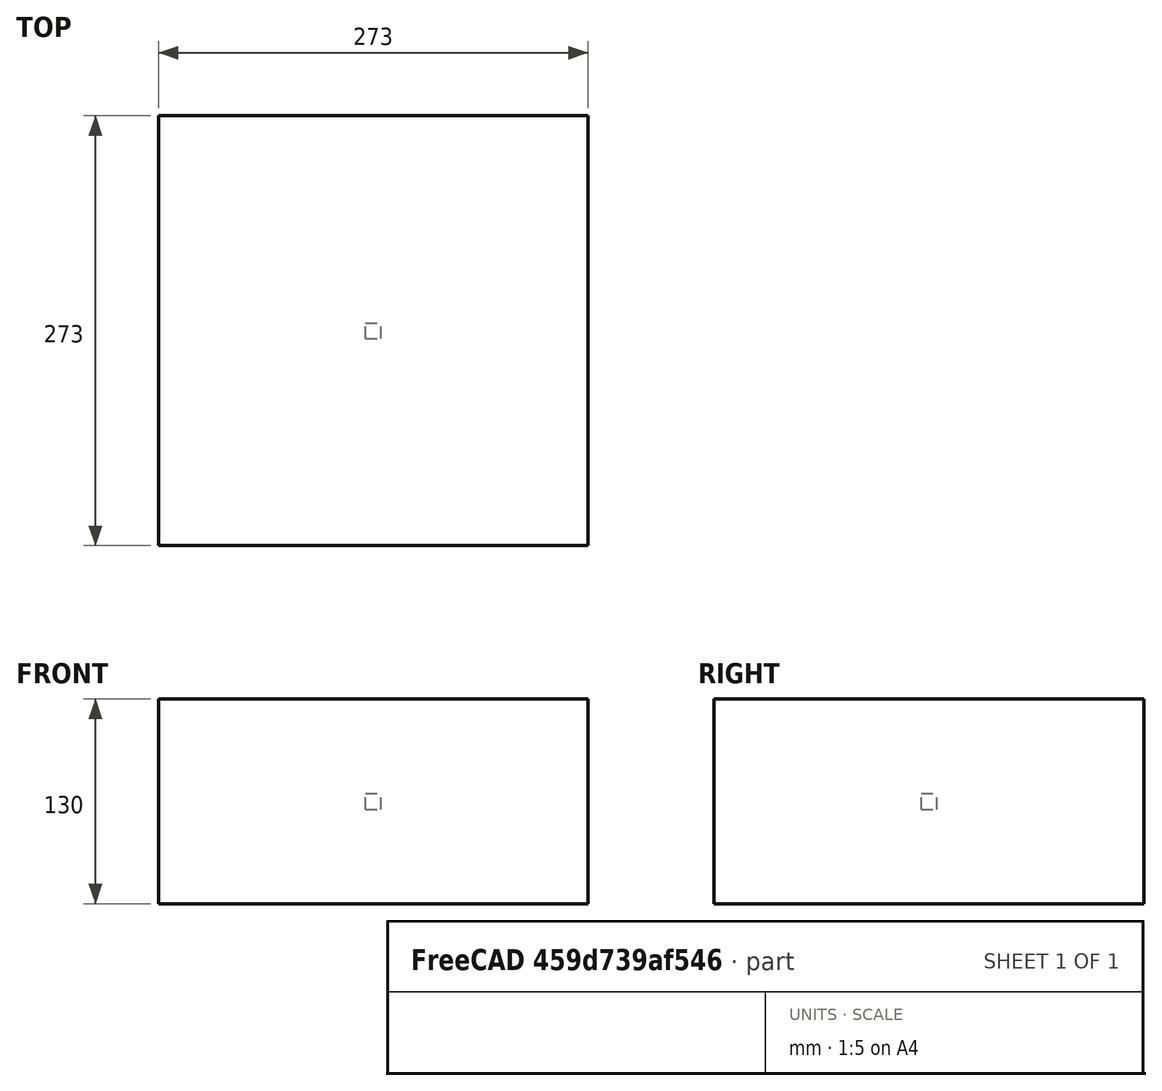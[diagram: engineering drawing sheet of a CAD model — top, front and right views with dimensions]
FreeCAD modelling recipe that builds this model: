
FCSTD DOCUMENT  (FreeCAD 0.20RUnknown)
Label: polarArray-2
License: All rights reserved
LicenseURL: http://en.wikipedia.org/wiki/All_rights_reserved
objects: App::DocumentObjectGroupPython×1251, Part::FeaturePython×3, App::Part×3
note: 2 computed .brp shape members not serialized (recipe doc carries the construction recipe); baked Part::Feature solids carry a one-line shape summary decoded from their .brp

FEATURE [App::DocumentObjectGroupPython] HALFPI  # scripted group (container) (typed FeaturePython)
  name = HALFPI
  value = pi/2.
FEATURE [App::DocumentObjectGroupPython] PI  # scripted group (container) (typed FeaturePython)
  name = PI
  value = 1.*pi
FEATURE [App::DocumentObjectGroupPython] TWOPI  # scripted group (container) (typed FeaturePython)
  name = TWOPI
  value = 2.*pi
FEATURE [App::DocumentObjectGroupPython] Constants  # scripted group (container) (typed FeaturePython)
  Group = -> [HALFPI,PI,TWOPI]
FEATURE [App::DocumentObjectGroupPython] Variables  # scripted group (container) (typed FeaturePython)
FEATURE [App::DocumentObjectGroupPython] Quantities  # scripted group (container) (typed FeaturePython)
FEATURE [App::DocumentObjectGroupPython] Isotopes  # scripted group (container) (typed FeaturePython)
FEATURE [App::DocumentObjectGroupPython] Elements  # scripted group (container) (typed FeaturePython)
FEATURE [App::DocumentObjectGroupPython] Matrix  # scripted group (container) (typed FeaturePython)
FEATURE [App::DocumentObjectGroupPython] Surfaces  # scripted group (container) (typed FeaturePython)
FEATURE [App::DocumentObjectGroupPython] Opticals  # scripted group (container) (typed FeaturePython)
  Group = -> [Matrix,Surfaces]
FEATURE [App::DocumentObjectGroupPython] G4Isotopes  # scripted group (container) (typed FeaturePython)
FEATURE [App::DocumentObjectGroupPython] H_element  # scripted group (container) (typed FeaturePython)
  Z = 1
  atom_value = 1.008
  formula = H
  name = H_element
FEATURE [App::DocumentObjectGroupPython] He_element  # scripted group (container) (typed FeaturePython)
  Z = 2
  atom_value = 4.0026
  formula = He
  name = He_element
FEATURE [App::DocumentObjectGroupPython] Li_element  # scripted group (container) (typed FeaturePython)
  Z = 3
  atom_value = 6.94
  formula = Li
  name = Li_element
FEATURE [App::DocumentObjectGroupPython] Be_element  # scripted group (container) (typed FeaturePython)
  Z = 4
  atom_value = 9.01218
  formula = Be
  name = Be_element
FEATURE [App::DocumentObjectGroupPython] B_element  # scripted group (container) (typed FeaturePython)
  Z = 5
  atom_value = 10.81
  formula = B
  name = B_element
FEATURE [App::DocumentObjectGroupPython] C_element  # scripted group (container) (typed FeaturePython)
  Z = 6
  atom_value = 12.011
  formula = C
  name = C_element
FEATURE [App::DocumentObjectGroupPython] N_element  # scripted group (container) (typed FeaturePython)
  Z = 7
  atom_value = 14.007
  formula = N
  name = N_element
FEATURE [App::DocumentObjectGroupPython] O_element  # scripted group (container) (typed FeaturePython)
  Z = 8
  atom_value = 15.999
  formula = O
  name = O_element
FEATURE [App::DocumentObjectGroupPython] F_element  # scripted group (container) (typed FeaturePython)
  Z = 9
  atom_value = 18.9984
  formula = F
  name = F_element
FEATURE [App::DocumentObjectGroupPython] Ne_element  # scripted group (container) (typed FeaturePython)
  Z = 10
  atom_value = 20.1797
  formula = Ne
  name = Ne_element
FEATURE [App::DocumentObjectGroupPython] Na_element  # scripted group (container) (typed FeaturePython)
  Z = 11
  atom_value = 22.9898
  formula = Na
  name = Na_element
FEATURE [App::DocumentObjectGroupPython] Mg_element  # scripted group (container) (typed FeaturePython)
  Z = 12
  atom_value = 24.305
  formula = Mg
  name = Mg_element
FEATURE [App::DocumentObjectGroupPython] Al_element  # scripted group (container) (typed FeaturePython)
  Z = 13
  atom_value = 26.9815
  formula = Al
  name = Al_element
FEATURE [App::DocumentObjectGroupPython] Si_element  # scripted group (container) (typed FeaturePython)
  Z = 14
  atom_value = 28.085
  formula = Si
  name = Si_element
FEATURE [App::DocumentObjectGroupPython] P_element  # scripted group (container) (typed FeaturePython)
  Z = 15
  atom_value = 30.9738
  formula = P
  name = P_element
FEATURE [App::DocumentObjectGroupPython] S_element  # scripted group (container) (typed FeaturePython)
  Z = 16
  atom_value = 32.06
  formula = S
  name = S_element
FEATURE [App::DocumentObjectGroupPython] Cl_element  # scripted group (container) (typed FeaturePython)
  Z = 17
  atom_value = 35.45
  formula = Cl
  name = Cl_element
FEATURE [App::DocumentObjectGroupPython] Ar_element  # scripted group (container) (typed FeaturePython)
  Z = 18
  atom_value = 39.95
  formula = Ar
  name = Ar_element
FEATURE [App::DocumentObjectGroupPython] K_element  # scripted group (container) (typed FeaturePython)
  Z = 19
  atom_value = 39.0983
  formula = K
  name = K_element
FEATURE [App::DocumentObjectGroupPython] Ca_element  # scripted group (container) (typed FeaturePython)
  Z = 20
  atom_value = 40.078
  formula = Ca
  name = Ca_element
FEATURE [App::DocumentObjectGroupPython] Sc_element  # scripted group (container) (typed FeaturePython)
  Z = 21
  atom_value = 44.9559
  formula = Sc
  name = Sc_element
FEATURE [App::DocumentObjectGroupPython] Ti_element  # scripted group (container) (typed FeaturePython)
  Z = 22
  atom_value = 47.867
  formula = Ti
  name = Ti_element
FEATURE [App::DocumentObjectGroupPython] V_element  # scripted group (container) (typed FeaturePython)
  Z = 23
  atom_value = 50.9415
  formula = V
  name = V_element
FEATURE [App::DocumentObjectGroupPython] Cr_element  # scripted group (container) (typed FeaturePython)
  Z = 24
  atom_value = 51.9961
  formula = Cr
  name = Cr_element
FEATURE [App::DocumentObjectGroupPython] Mn_element  # scripted group (container) (typed FeaturePython)
  Z = 25
  atom_value = 54.938
  formula = Mn
  name = Mn_element
FEATURE [App::DocumentObjectGroupPython] Fe_element  # scripted group (container) (typed FeaturePython)
  Z = 26
  atom_value = 55.845
  formula = Fe
  name = Fe_element
FEATURE [App::DocumentObjectGroupPython] Co_element  # scripted group (container) (typed FeaturePython)
  Z = 27
  atom_value = 58.9332
  formula = Co
  name = Co_element
FEATURE [App::DocumentObjectGroupPython] Ni_element  # scripted group (container) (typed FeaturePython)
  Z = 28
  atom_value = 58.6934
  formula = Ni
  name = Ni_element
FEATURE [App::DocumentObjectGroupPython] Cu_element  # scripted group (container) (typed FeaturePython)
  Z = 29
  atom_value = 63.546
  formula = Cu
  name = Cu_element
FEATURE [App::DocumentObjectGroupPython] Zn_element  # scripted group (container) (typed FeaturePython)
  Z = 30
  atom_value = 65.38
  formula = Zn
  name = Zn_element
FEATURE [App::DocumentObjectGroupPython] Ga_element  # scripted group (container) (typed FeaturePython)
  Z = 31
  atom_value = 69.723
  formula = Ga
  name = Ga_element
FEATURE [App::DocumentObjectGroupPython] Ge_element  # scripted group (container) (typed FeaturePython)
  Z = 32
  atom_value = 72.63
  formula = Ge
  name = Ge_element
FEATURE [App::DocumentObjectGroupPython] As_element  # scripted group (container) (typed FeaturePython)
  Z = 33
  atom_value = 74.9216
  formula = As
  name = As_element
FEATURE [App::DocumentObjectGroupPython] Se_element  # scripted group (container) (typed FeaturePython)
  Z = 34
  atom_value = 78.971
  formula = Se
  name = Se_element
FEATURE [App::DocumentObjectGroupPython] Br_element  # scripted group (container) (typed FeaturePython)
  Z = 35
  atom_value = 79.904
  formula = Br
  name = Br_element
FEATURE [App::DocumentObjectGroupPython] Kr_element  # scripted group (container) (typed FeaturePython)
  Z = 36
  atom_value = 83.798
  formula = Kr
  name = Kr_element
FEATURE [App::DocumentObjectGroupPython] Rb_element  # scripted group (container) (typed FeaturePython)
  Z = 37
  atom_value = 85.4678
  formula = Rb
  name = Rb_element
FEATURE [App::DocumentObjectGroupPython] Sr_element  # scripted group (container) (typed FeaturePython)
  Z = 38
  atom_value = 87.62
  formula = Sr
  name = Sr_element
FEATURE [App::DocumentObjectGroupPython] Y_element  # scripted group (container) (typed FeaturePython)
  Z = 39
  atom_value = 88.9058
  formula = Y
  name = Y_element
FEATURE [App::DocumentObjectGroupPython] Zr_element  # scripted group (container) (typed FeaturePython)
  Z = 40
  atom_value = 91.224
  formula = Zr
  name = Zr_element
FEATURE [App::DocumentObjectGroupPython] Nb_element  # scripted group (container) (typed FeaturePython)
  Z = 41
  atom_value = 92.9064
  formula = Nb
  name = Nb_element
FEATURE [App::DocumentObjectGroupPython] Mo_element  # scripted group (container) (typed FeaturePython)
  Z = 42
  atom_value = 95.95
  formula = Mo
  name = Mo_element
FEATURE [App::DocumentObjectGroupPython] Tc_element  # scripted group (container) (typed FeaturePython)
  Z = 43
  atom_value = 97
  formula = Tc
  name = Tc_element
FEATURE [App::DocumentObjectGroupPython] Ru_element  # scripted group (container) (typed FeaturePython)
  Z = 44
  atom_value = 101.07
  formula = Ru
  name = Ru_element
FEATURE [App::DocumentObjectGroupPython] Rh_element  # scripted group (container) (typed FeaturePython)
  Z = 45
  atom_value = 102.905
  formula = Rh
  name = Rh_element
FEATURE [App::DocumentObjectGroupPython] Pd_element  # scripted group (container) (typed FeaturePython)
  Z = 46
  atom_value = 106.42
  formula = Pd
  name = Pd_element
FEATURE [App::DocumentObjectGroupPython] Ag_element  # scripted group (container) (typed FeaturePython)
  Z = 47
  atom_value = 107.868
  formula = Ag
  name = Ag_element
FEATURE [App::DocumentObjectGroupPython] Cd_element  # scripted group (container) (typed FeaturePython)
  Z = 48
  atom_value = 112.414
  formula = Cd
  name = Cd_element
FEATURE [App::DocumentObjectGroupPython] In_element  # scripted group (container) (typed FeaturePython)
  Z = 49
  atom_value = 114.818
  formula = In
  name = In_element
FEATURE [App::DocumentObjectGroupPython] Sn_element  # scripted group (container) (typed FeaturePython)
  Z = 50
  atom_value = 118.71
  formula = Sn
  name = Sn_element
FEATURE [App::DocumentObjectGroupPython] Sb_element  # scripted group (container) (typed FeaturePython)
  Z = 51
  atom_value = 121.76
  formula = Sb
  name = Sb_element
FEATURE [App::DocumentObjectGroupPython] Te_element  # scripted group (container) (typed FeaturePython)
  Z = 52
  atom_value = 127.6
  formula = Te
  name = Te_element
FEATURE [App::DocumentObjectGroupPython] I_element  # scripted group (container) (typed FeaturePython)
  Z = 53
  atom_value = 126.904
  formula = I
  name = I_element
FEATURE [App::DocumentObjectGroupPython] Xe_element  # scripted group (container) (typed FeaturePython)
  Z = 54
  atom_value = 131.293
  formula = Xe
  name = Xe_element
FEATURE [App::DocumentObjectGroupPython] Cs_element  # scripted group (container) (typed FeaturePython)
  Z = 55
  atom_value = 132.905
  formula = Cs
  name = Cs_element
FEATURE [App::DocumentObjectGroupPython] Ba_element  # scripted group (container) (typed FeaturePython)
  Z = 56
  atom_value = 137.327
  formula = Ba
  name = Ba_element
FEATURE [App::DocumentObjectGroupPython] La_element  # scripted group (container) (typed FeaturePython)
  Z = 57
  atom_value = 138.905
  formula = La
  name = La_element
FEATURE [App::DocumentObjectGroupPython] Ce_element  # scripted group (container) (typed FeaturePython)
  Z = 58
  atom_value = 140.116
  formula = Ce
  name = Ce_element
FEATURE [App::DocumentObjectGroupPython] Pr_element  # scripted group (container) (typed FeaturePython)
  Z = 59
  atom_value = 140.908
  formula = Pr
  name = Pr_element
FEATURE [App::DocumentObjectGroupPython] Nd_element  # scripted group (container) (typed FeaturePython)
  Z = 60
  atom_value = 144.242
  formula = Nd
  name = Nd_element
FEATURE [App::DocumentObjectGroupPython] Pm_element  # scripted group (container) (typed FeaturePython)
  Z = 61
  atom_value = 145
  formula = Pm
  name = Pm_element
FEATURE [App::DocumentObjectGroupPython] Sm_element  # scripted group (container) (typed FeaturePython)
  Z = 62
  atom_value = 150.36
  formula = Sm
  name = Sm_element
FEATURE [App::DocumentObjectGroupPython] Eu_element  # scripted group (container) (typed FeaturePython)
  Z = 63
  atom_value = 151.964
  formula = Eu
  name = Eu_element
FEATURE [App::DocumentObjectGroupPython] Gd_element  # scripted group (container) (typed FeaturePython)
  Z = 64
  atom_value = 157.25
  formula = Gd
  name = Gd_element
FEATURE [App::DocumentObjectGroupPython] Tb_element  # scripted group (container) (typed FeaturePython)
  Z = 65
  atom_value = 158.925
  formula = Tb
  name = Tb_element
FEATURE [App::DocumentObjectGroupPython] Dy_element  # scripted group (container) (typed FeaturePython)
  Z = 66
  atom_value = 162.5
  formula = Dy
  name = Dy_element
FEATURE [App::DocumentObjectGroupPython] Ho_element  # scripted group (container) (typed FeaturePython)
  Z = 67
  atom_value = 164.93
  formula = Ho
  name = Ho_element
FEATURE [App::DocumentObjectGroupPython] Er_element  # scripted group (container) (typed FeaturePython)
  Z = 68
  atom_value = 167.259
  formula = Er
  name = Er_element
FEATURE [App::DocumentObjectGroupPython] Tm_element  # scripted group (container) (typed FeaturePython)
  Z = 69
  atom_value = 168.934
  formula = Tm
  name = Tm_element
FEATURE [App::DocumentObjectGroupPython] Yb_element  # scripted group (container) (typed FeaturePython)
  Z = 70
  atom_value = 173.045
  formula = Yb
  name = Yb_element
FEATURE [App::DocumentObjectGroupPython] Lu_element  # scripted group (container) (typed FeaturePython)
  Z = 71
  atom_value = 174.967
  formula = Lu
  name = Lu_element
FEATURE [App::DocumentObjectGroupPython] Hf_element  # scripted group (container) (typed FeaturePython)
  Z = 72
  atom_value = 178.49
  formula = Hf
  name = Hf_element
FEATURE [App::DocumentObjectGroupPython] Ta_element  # scripted group (container) (typed FeaturePython)
  Z = 73
  atom_value = 180.948
  formula = Ta
  name = Ta_element
FEATURE [App::DocumentObjectGroupPython] W_element  # scripted group (container) (typed FeaturePython)
  Z = 74
  atom_value = 183.84
  formula = W
  name = W_element
FEATURE [App::DocumentObjectGroupPython] Re_element  # scripted group (container) (typed FeaturePython)
  Z = 75
  atom_value = 186.207
  formula = Re
  name = Re_element
FEATURE [App::DocumentObjectGroupPython] Os_element  # scripted group (container) (typed FeaturePython)
  Z = 76
  atom_value = 190.23
  formula = Os
  name = Os_element
FEATURE [App::DocumentObjectGroupPython] Ir_element  # scripted group (container) (typed FeaturePython)
  Z = 77
  atom_value = 192.217
  formula = Ir
  name = Ir_element
FEATURE [App::DocumentObjectGroupPython] Pt_element  # scripted group (container) (typed FeaturePython)
  Z = 78
  atom_value = 195.084
  formula = Pt
  name = Pt_element
FEATURE [App::DocumentObjectGroupPython] Au_element  # scripted group (container) (typed FeaturePython)
  Z = 79
  atom_value = 196.967
  formula = Au
  name = Au_element
FEATURE [App::DocumentObjectGroupPython] Hg_element  # scripted group (container) (typed FeaturePython)
  Z = 80
  atom_value = 200.592
  formula = Hg
  name = Hg_element
FEATURE [App::DocumentObjectGroupPython] Tl_element  # scripted group (container) (typed FeaturePython)
  Z = 81
  atom_value = 204.38
  formula = Tl
  name = Tl_element
FEATURE [App::DocumentObjectGroupPython] Pb_element  # scripted group (container) (typed FeaturePython)
  Z = 82
  atom_value = 207.2
  formula = Pb
  name = Pb_element
FEATURE [App::DocumentObjectGroupPython] Bi_element  # scripted group (container) (typed FeaturePython)
  Z = 83
  atom_value = 208.98
  formula = Bi
  name = Bi_element
FEATURE [App::DocumentObjectGroupPython] Po_element  # scripted group (container) (typed FeaturePython)
  Z = 84
  atom_value = 209
  formula = Po
  name = Po_element
FEATURE [App::DocumentObjectGroupPython] At_element  # scripted group (container) (typed FeaturePython)
  Z = 85
  atom_value = 210
  formula = At
  name = At_element
FEATURE [App::DocumentObjectGroupPython] Rn_element  # scripted group (container) (typed FeaturePython)
  Z = 86
  atom_value = 222
  formula = Rn
  name = Rn_element
FEATURE [App::DocumentObjectGroupPython] Fr_element  # scripted group (container) (typed FeaturePython)
  Z = 87
  atom_value = 223
  formula = Fr
  name = Fr_element
FEATURE [App::DocumentObjectGroupPython] Ra_element  # scripted group (container) (typed FeaturePython)
  Z = 88
  atom_value = 226
  formula = Ra
  name = Ra_element
FEATURE [App::DocumentObjectGroupPython] Ac_element  # scripted group (container) (typed FeaturePython)
  Z = 89
  atom_value = 227
  formula = Ac
  name = Ac_element
FEATURE [App::DocumentObjectGroupPython] Th_element  # scripted group (container) (typed FeaturePython)
  Z = 90
  atom_value = 232.038
  formula = Th
  name = Th_element
FEATURE [App::DocumentObjectGroupPython] Pa_element  # scripted group (container) (typed FeaturePython)
  Z = 91
  atom_value = 231.036
  formula = Pa
  name = Pa_element
FEATURE [App::DocumentObjectGroupPython] U_element  # scripted group (container) (typed FeaturePython)
  Z = 92
  atom_value = 238.029
  formula = U
  name = U_element
FEATURE [App::DocumentObjectGroupPython] Np_element  # scripted group (container) (typed FeaturePython)
  Z = 93
  atom_value = 237
  formula = Np
  name = Np_element
FEATURE [App::DocumentObjectGroupPython] Pu_element  # scripted group (container) (typed FeaturePython)
  Z = 94
  atom_value = 244
  formula = Pu
  name = Pu_element
FEATURE [App::DocumentObjectGroupPython] Am_element  # scripted group (container) (typed FeaturePython)
  Z = 95
  atom_value = 243
  formula = Am
  name = Am_element
FEATURE [App::DocumentObjectGroupPython] Cm_element  # scripted group (container) (typed FeaturePython)
  Z = 96
  atom_value = 247
  formula = Cm
  name = Cm_element
FEATURE [App::DocumentObjectGroupPython] Bk_element  # scripted group (container) (typed FeaturePython)
  Z = 97
  atom_value = 247
  formula = Bk
  name = Bk_element
FEATURE [App::DocumentObjectGroupPython] Cf_element  # scripted group (container) (typed FeaturePython)
  Z = 98
  atom_value = 251
  formula = Cf
  name = Cf_element
FEATURE [App::DocumentObjectGroupPython] G4Elements  # scripted group (container) (typed FeaturePython)
  Group = -> [H_element,He_element,Li_element,Be_element,B_element,C_element,N_element,O_element,F_element,Ne_element,Na_element,Mg_element,Al_element,Si_element,P_element,S_element,Cl_element,Ar_element,K_element,Ca_element,Sc_element,Ti_element,V_element,Cr_element,Mn_element,Fe_element,Co_element,Ni_element,Cu_element,Zn_element,Ga_element,Ge_element,As_element,Se_element,Br_element,Kr_element,Rb_element,+61 more]
FEATURE [App::DocumentObjectGroupPython] H_element001  label="H_element : 0.101"  # scripted group (container) (typed FeaturePython)
  n = 0.101327
FEATURE [App::DocumentObjectGroupPython] C_element001  label="C_element : 0.775"  # scripted group (container) (typed FeaturePython)
  n = 0.7755
FEATURE [App::DocumentObjectGroupPython] N_element001  label="N_element : 0.035"  # scripted group (container) (typed FeaturePython)
  n = 0.035057
FEATURE [App::DocumentObjectGroupPython] O_element001  label="O_element : 0.052"  # scripted group (container) (typed FeaturePython)
  n = 0.0523159
FEATURE [App::DocumentObjectGroupPython] F_element001  label="F_element : 0.017"  # scripted group (container) (typed FeaturePython)
  n = 0.017422
FEATURE [App::DocumentObjectGroupPython] Ca_element001  label="Ca_element : 0.018"  # scripted group (container) (typed FeaturePython)
  n = 0.018378
FEATURE [App::DocumentObjectGroupPython] G4_A_150_TISSUE  label="G4_A-150_TISSUE"  # scripted group (container) (typed FeaturePython)
  Dunit = g/cm3
  Dvalue = 1.127
  Group = -> [H_element001,C_element001,N_element001,O_element001,F_element001,Ca_element001]
  conduct = 2
  density = 1
  expand = 3
  formula = G4_A-150_TISSUE
  name = G4_A-150_TISSUE
  specific = 4
FEATURE [App::DocumentObjectGroupPython] C_element002  label="C_element : 3"  # scripted group (container) (typed FeaturePython)
  n = 3
  ref = C_element
FEATURE [App::DocumentObjectGroupPython] H_element002  label="H_element : 6"  # scripted group (container) (typed FeaturePython)
  n = 6
  ref = H_element
FEATURE [App::DocumentObjectGroupPython] O_element002  label="O_element : 1"  # scripted group (container) (typed FeaturePython)
  n = 1
  ref = O_element
FEATURE [App::DocumentObjectGroupPython] G4_ACETONE  # scripted group (container) (typed FeaturePython)
  Dunit = g/cm3
  Dvalue = 0.7899
  Group = -> [C_element002,H_element002,O_element002]
  conduct = 2
  density = 1
  expand = 3
  formula = G4_ACETONE
  name = G4_ACETONE
  specific = 4
FEATURE [App::DocumentObjectGroupPython] C_element003  label="C_element : 2"  # scripted group (container) (typed FeaturePython)
  n = 2
  ref = C_element
FEATURE [App::DocumentObjectGroupPython] H_element003  label="H_element : 2"  # scripted group (container) (typed FeaturePython)
  n = 2
  ref = H_element
FEATURE [App::DocumentObjectGroupPython] G4_ACETYLENE  # scripted group (container) (typed FeaturePython)
  Dunit = g/cm3
  Dvalue = 0.0010967
  Group = -> [C_element003,H_element003]
  conduct = 2
  density = 1
  expand = 3
  formula = G4_ACETYLENE
  name = G4_ACETYLENE
  specific = 4
FEATURE [App::DocumentObjectGroupPython] C_element004  label="C_element : 5"  # scripted group (container) (typed FeaturePython)
  n = 5
  ref = C_element
FEATURE [App::DocumentObjectGroupPython] H_element004  label="H_element : 5"  # scripted group (container) (typed FeaturePython)
  n = 5
  ref = H_element
FEATURE [App::DocumentObjectGroupPython] N_element002  label="N_element : 5"  # scripted group (container) (typed FeaturePython)
  n = 5
  ref = N_element
FEATURE [App::DocumentObjectGroupPython] G4_ADENINE  # scripted group (container) (typed FeaturePython)
  Dunit = g/cm3
  Dvalue = 1.6
  Group = -> [C_element004,H_element004,N_element002]
  conduct = 2
  density = 1
  expand = 3
  formula = G4_ADENINE
  name = G4_ADENINE
  specific = 4
FEATURE [App::DocumentObjectGroupPython] H_element005  label="H_element : 0.114"  # scripted group (container) (typed FeaturePython)
  n = 0.114
FEATURE [App::DocumentObjectGroupPython] C_element005  label="C_element : 0.598"  # scripted group (container) (typed FeaturePython)
  n = 0.598
FEATURE [App::DocumentObjectGroupPython] N_element003  label="N_element : 0.007"  # scripted group (container) (typed FeaturePython)
  n = 0.007
FEATURE [App::DocumentObjectGroupPython] O_element003  label="O_element : 0.278"  # scripted group (container) (typed FeaturePython)
  n = 0.278
FEATURE [App::DocumentObjectGroupPython] Na_element001  label="Na_element : 0.001"  # scripted group (container) (typed FeaturePython)
  n = 0.001
FEATURE [App::DocumentObjectGroupPython] S_element001  label="S_element : 0.001"  # scripted group (container) (typed FeaturePython)
  n = 0.001
FEATURE [App::DocumentObjectGroupPython] Cl_element001  label="Cl_element : 0.001"  # scripted group (container) (typed FeaturePython)
  n = 0.001
FEATURE [App::DocumentObjectGroupPython] G4_ADIPOSE_TISSUE_ICRP  # scripted group (container) (typed FeaturePython)
  Dunit = g/cm3
  Dvalue = 0.95
  Group = -> [H_element005,C_element005,N_element003,O_element003,Na_element001,S_element001,Cl_element001]
  conduct = 2
  density = 1
  expand = 3
  formula = G4_ADIPOSE_TISSUE_ICRP
  name = G4_ADIPOSE_TISSUE_ICRP
  specific = 4
FEATURE [App::DocumentObjectGroupPython] C_element006  label="C_element : 0.000"  # scripted group (container) (typed FeaturePython)
  n = 0.000124
FEATURE [App::DocumentObjectGroupPython] N_element004  label="N_element : 0.755"  # scripted group (container) (typed FeaturePython)
  n = 0.755268
FEATURE [App::DocumentObjectGroupPython] O_element004  label="O_element : 0.232"  # scripted group (container) (typed FeaturePython)
  n = 0.231781
FEATURE [App::DocumentObjectGroupPython] Ar_element001  label="Ar_element : 0.013"  # scripted group (container) (typed FeaturePython)
  n = 0.012827
FEATURE [App::DocumentObjectGroupPython] G4_AIR  # scripted group (container) (typed FeaturePython)
  Dunit = g/cm3
  Dvalue = 0.00120479
  Group = -> [C_element006,N_element004,O_element004,Ar_element001]
  conduct = 2
  density = 1
  expand = 3
  formula = G4_AIR
  name = G4_AIR
  specific = 4
FEATURE [App::DocumentObjectGroupPython] C_element007  label="C_element : 006"  # scripted group (container) (typed FeaturePython)
  n = 3
  ref = C_element
FEATURE [App::DocumentObjectGroupPython] H_element006  label="H_element : 7"  # scripted group (container) (typed FeaturePython)
  n = 7
  ref = H_element
FEATURE [App::DocumentObjectGroupPython] N_element005  label="N_element : 1"  # scripted group (container) (typed FeaturePython)
  n = 1
  ref = N_element
FEATURE [App::DocumentObjectGroupPython] O_element005  label="O_element : 2"  # scripted group (container) (typed FeaturePython)
  n = 2
  ref = O_element
FEATURE [App::DocumentObjectGroupPython] G4_ALANINE  # scripted group (container) (typed FeaturePython)
  Dunit = g/cm3
  Dvalue = 1.42
  Group = -> [C_element007,H_element006,N_element005,O_element005]
  conduct = 2
  density = 1
  expand = 3
  formula = G4_ALANINE
  name = G4_ALANINE
  specific = 4
FEATURE [App::DocumentObjectGroupPython] Al_element001  label="Al_element : 2"  # scripted group (container) (typed FeaturePython)
  n = 2
  ref = Al_element
FEATURE [App::DocumentObjectGroupPython] O_element006  label="O_element : 3"  # scripted group (container) (typed FeaturePython)
  n = 3
  ref = O_element
FEATURE [App::DocumentObjectGroupPython] G4_ALUMINUM_OXIDE  # scripted group (container) (typed FeaturePython)
  Dunit = g/cm3
  Dvalue = 3.97
  Group = -> [Al_element001,O_element006]
  conduct = 2
  density = 1
  expand = 3
  formula = G4_ALUMINUM_OXIDE
  name = G4_ALUMINUM_OXIDE
  specific = 4
FEATURE [App::DocumentObjectGroupPython] H_element007  label="H_element : 0.106"  # scripted group (container) (typed FeaturePython)
  n = 0.10593
FEATURE [App::DocumentObjectGroupPython] C_element008  label="C_element : 0.789"  # scripted group (container) (typed FeaturePython)
  n = 0.788974
FEATURE [App::DocumentObjectGroupPython] O_element007  label="O_element : 0.105"  # scripted group (container) (typed FeaturePython)
  n = 0.105096
FEATURE [App::DocumentObjectGroupPython] G4_AMBER  # scripted group (container) (typed FeaturePython)
  Dunit = g/cm3
  Dvalue = 1.1
  Group = -> [H_element007,C_element008,O_element007]
  conduct = 2
  density = 1
  expand = 3
  formula = G4_AMBER
  name = G4_AMBER
  specific = 4
FEATURE [App::DocumentObjectGroupPython] N_element006  label="N_element : 006"  # scripted group (container) (typed FeaturePython)
  n = 1
  ref = N_element
FEATURE [App::DocumentObjectGroupPython] H_element008  label="H_element : 3"  # scripted group (container) (typed FeaturePython)
  n = 3
  ref = H_element
FEATURE [App::DocumentObjectGroupPython] G4_AMMONIA  # scripted group (container) (typed FeaturePython)
  Dunit = g/cm3
  Dvalue = 0.000826019
  Group = -> [N_element006,H_element008]
  conduct = 2
  density = 1
  expand = 3
  formula = G4_AMMONIA
  name = G4_AMMONIA
  specific = 4
FEATURE [App::DocumentObjectGroupPython] C_element009  label="C_element : 6"  # scripted group (container) (typed FeaturePython)
  n = 6
  ref = C_element
FEATURE [App::DocumentObjectGroupPython] H_element009  label="H_element : 008"  # scripted group (container) (typed FeaturePython)
  n = 7
  ref = H_element
FEATURE [App::DocumentObjectGroupPython] N_element007  label="N_element : 007"  # scripted group (container) (typed FeaturePython)
  n = 1
  ref = N_element
FEATURE [App::DocumentObjectGroupPython] G4_ANILINE  # scripted group (container) (typed FeaturePython)
  Dunit = g/cm3
  Dvalue = 1.0235
  Group = -> [C_element009,H_element009,N_element007]
  conduct = 2
  density = 1
  expand = 3
  formula = G4_ANILINE
  name = G4_ANILINE
  specific = 4
FEATURE [App::DocumentObjectGroupPython] C_element010  label="C_element : 14"  # scripted group (container) (typed FeaturePython)
  n = 14
  ref = C_element
FEATURE [App::DocumentObjectGroupPython] H_element010  label="H_element : 10"  # scripted group (container) (typed FeaturePython)
  n = 10
  ref = H_element
FEATURE [App::DocumentObjectGroupPython] G4_ANTHRACENE  # scripted group (container) (typed FeaturePython)
  Dunit = g/cm3
  Dvalue = 1.283
  Group = -> [C_element010,H_element010]
  conduct = 2
  density = 1
  expand = 3
  formula = G4_ANTHRACENE
  name = G4_ANTHRACENE
  specific = 4
FEATURE [App::DocumentObjectGroupPython] H_element011  label="H_element : 0.065"  # scripted group (container) (typed FeaturePython)
  n = 0.0654709
FEATURE [App::DocumentObjectGroupPython] C_element011  label="C_element : 0.537"  # scripted group (container) (typed FeaturePython)
  n = 0.536944
FEATURE [App::DocumentObjectGroupPython] N_element008  label="N_element : 0.021"  # scripted group (container) (typed FeaturePython)
  n = 0.0215
FEATURE [App::DocumentObjectGroupPython] O_element008  label="O_element : 0.032"  # scripted group (container) (typed FeaturePython)
  n = 0.032085
FEATURE [App::DocumentObjectGroupPython] F_element002  label="F_element : 0.167"  # scripted group (container) (typed FeaturePython)
  n = 0.167411
FEATURE [App::DocumentObjectGroupPython] Ca_element002  label="Ca_element : 0.177"  # scripted group (container) (typed FeaturePython)
  n = 0.176589
FEATURE [App::DocumentObjectGroupPython] G4_B_100_BONE  label="G4_B-100_BONE"  # scripted group (container) (typed FeaturePython)
  Dunit = g/cm3
  Dvalue = 1.45
  Group = -> [H_element011,C_element011,N_element008,O_element008,F_element002,Ca_element002]
  conduct = 2
  density = 1
  expand = 3
  formula = G4_B-100_BONE
  name = G4_B-100_BONE
  specific = 4
FEATURE [App::DocumentObjectGroupPython] H_element012  label="H_element : 0.057"  # scripted group (container) (typed FeaturePython)
  n = 0.057441
FEATURE [App::DocumentObjectGroupPython] C_element012  label="C_element : 0.790"  # scripted group (container) (typed FeaturePython)
  n = 0.774591
FEATURE [App::DocumentObjectGroupPython] O_element009  label="O_element : 0.168"  # scripted group (container) (typed FeaturePython)
  n = 0.167968
FEATURE [App::DocumentObjectGroupPython] G4_BAKELITE  # scripted group (container) (typed FeaturePython)
  Dunit = g/cm3
  Dvalue = 1.25
  Group = -> [H_element012,C_element012,O_element009]
  conduct = 2
  density = 1
  expand = 3
  formula = G4_BAKELITE
  name = G4_BAKELITE
  specific = 4
FEATURE [App::DocumentObjectGroupPython] Ba_element001  label="Ba_element : 1"  # scripted group (container) (typed FeaturePython)
  n = 1
  ref = Ba_element
FEATURE [App::DocumentObjectGroupPython] F_element003  label="F_element : 2"  # scripted group (container) (typed FeaturePython)
  n = 2
  ref = F_element
FEATURE [App::DocumentObjectGroupPython] G4_BARIUM_FLUORIDE  # scripted group (container) (typed FeaturePython)
  Dunit = g/cm3
  Dvalue = 4.89
  Group = -> [Ba_element001,F_element003]
  conduct = 2
  density = 1
  expand = 3
  formula = G4_BARIUM_FLUORIDE
  name = G4_BARIUM_FLUORIDE
  specific = 4
FEATURE [App::DocumentObjectGroupPython] Ba_element002  label="Ba_element : 002"  # scripted group (container) (typed FeaturePython)
  n = 1
  ref = Ba_element
FEATURE [App::DocumentObjectGroupPython] S_element002  label="S_element : 1"  # scripted group (container) (typed FeaturePython)
  n = 1
  ref = S_element
FEATURE [App::DocumentObjectGroupPython] O_element010  label="O_element : 4"  # scripted group (container) (typed FeaturePython)
  n = 4
  ref = O_element
FEATURE [App::DocumentObjectGroupPython] G4_BARIUM_SULFATE  # scripted group (container) (typed FeaturePython)
  Dunit = g/cm3
  Dvalue = 4.5
  Group = -> [Ba_element002,S_element002,O_element010]
  conduct = 2
  density = 1
  expand = 3
  formula = G4_BARIUM_SULFATE
  name = G4_BARIUM_SULFATE
  specific = 4
FEATURE [App::DocumentObjectGroupPython] C_element013  label="C_element : 007"  # scripted group (container) (typed FeaturePython)
  n = 6
  ref = C_element
FEATURE [App::DocumentObjectGroupPython] H_element013  label="H_element : 009"  # scripted group (container) (typed FeaturePython)
  n = 6
  ref = H_element
FEATURE [App::DocumentObjectGroupPython] G4_BENZENE  # scripted group (container) (typed FeaturePython)
  Dunit = g/cm3
  Dvalue = 0.87865
  Group = -> [C_element013,H_element013]
  conduct = 2
  density = 1
  expand = 3
  formula = G4_BENZENE
  name = G4_BENZENE
  specific = 4
FEATURE [App::DocumentObjectGroupPython] Be_element001  label="Be_element : 1"  # scripted group (container) (typed FeaturePython)
  n = 1
  ref = Be_element
FEATURE [App::DocumentObjectGroupPython] O_element011  label="O_element : 005"  # scripted group (container) (typed FeaturePython)
  n = 1
  ref = O_element
FEATURE [App::DocumentObjectGroupPython] G4_BERYLLIUM_OXIDE  # scripted group (container) (typed FeaturePython)
  Dunit = g/cm3
  Dvalue = 3.01
  Group = -> [Be_element001,O_element011]
  conduct = 2
  density = 1
  expand = 3
  formula = G4_BERYLLIUM_OXIDE
  name = G4_BERYLLIUM_OXIDE
  specific = 4
FEATURE [App::DocumentObjectGroupPython] Bi_element001  label="Bi_element : 4"  # scripted group (container) (typed FeaturePython)
  n = 4
  ref = Bi_element
FEATURE [App::DocumentObjectGroupPython] Ge_element001  label="Ge_element : 3"  # scripted group (container) (typed FeaturePython)
  n = 3
  ref = Ge_element
FEATURE [App::DocumentObjectGroupPython] O_element012  label="O_element : 12"  # scripted group (container) (typed FeaturePython)
  n = 12
  ref = O_element
FEATURE [App::DocumentObjectGroupPython] G4_BGO  # scripted group (container) (typed FeaturePython)
  Dunit = g/cm3
  Dvalue = 7.13
  Group = -> [Bi_element001,Ge_element001,O_element012]
  conduct = 2
  density = 1
  expand = 3
  formula = G4_BGO
  name = G4_BGO
  specific = 4
FEATURE [App::DocumentObjectGroupPython] H_element014  label="H_element : 0.102"  # scripted group (container) (typed FeaturePython)
  n = 0.102
FEATURE [App::DocumentObjectGroupPython] C_element014  label="C_element : 0.110"  # scripted group (container) (typed FeaturePython)
  n = 0.11
FEATURE [App::DocumentObjectGroupPython] N_element009  label="N_element : 0.033"  # scripted group (container) (typed FeaturePython)
  n = 0.033
FEATURE [App::DocumentObjectGroupPython] O_element013  label="O_element : 0.745"  # scripted group (container) (typed FeaturePython)
  n = 0.745
FEATURE [App::DocumentObjectGroupPython] Na_element002  label="Na_element : 0.002"  # scripted group (container) (typed FeaturePython)
  n = 0.001
FEATURE [App::DocumentObjectGroupPython] P_element001  label="P_element : 0.001"  # scripted group (container) (typed FeaturePython)
  n = 0.001
FEATURE [App::DocumentObjectGroupPython] S_element003  label="S_element : 0.002"  # scripted group (container) (typed FeaturePython)
  n = 0.002
FEATURE [App::DocumentObjectGroupPython] Cl_element002  label="Cl_element : 0.003"  # scripted group (container) (typed FeaturePython)
  n = 0.003
FEATURE [App::DocumentObjectGroupPython] K_element001  label="K_element : 0.002"  # scripted group (container) (typed FeaturePython)
  n = 0.002
FEATURE [App::DocumentObjectGroupPython] Fe_element001  label="Fe_element : 0.001"  # scripted group (container) (typed FeaturePython)
  n = 0.001
FEATURE [App::DocumentObjectGroupPython] G4_BLOOD_ICRP  # scripted group (container) (typed FeaturePython)
  Dunit = g/cm3
  Dvalue = 1.06
  Group = -> [H_element014,C_element014,N_element009,O_element013,Na_element002,P_element001,S_element003,Cl_element002,K_element001,Fe_element001]
  conduct = 2
  density = 1
  expand = 3
  formula = G4_BLOOD_ICRP
  name = G4_BLOOD_ICRP
  specific = 4
FEATURE [App::DocumentObjectGroupPython] H_element015  label="H_element : 0.064"  # scripted group (container) (typed FeaturePython)
  n = 0.064
FEATURE [App::DocumentObjectGroupPython] C_element015  label="C_element : 0.278"  # scripted group (container) (typed FeaturePython)
  n = 0.278
FEATURE [App::DocumentObjectGroupPython] N_element010  label="N_element : 0.027"  # scripted group (container) (typed FeaturePython)
  n = 0.027
FEATURE [App::DocumentObjectGroupPython] O_element014  label="O_element : 0.410"  # scripted group (container) (typed FeaturePython)
  n = 0.41
FEATURE [App::DocumentObjectGroupPython] Mg_element001  label="Mg_element : 0.002"  # scripted group (container) (typed FeaturePython)
  n = 0.002
FEATURE [App::DocumentObjectGroupPython] P_element002  label="P_element : 0.070"  # scripted group (container) (typed FeaturePython)
  n = 0.07
FEATURE [App::DocumentObjectGroupPython] S_element004  label="S_element : 0.003"  # scripted group (container) (typed FeaturePython)
  n = 0.002
FEATURE [App::DocumentObjectGroupPython] Ca_element003  label="Ca_element : 0.147"  # scripted group (container) (typed FeaturePython)
  n = 0.147
FEATURE [App::DocumentObjectGroupPython] G4_BONE_COMPACT_ICRU  # scripted group (container) (typed FeaturePython)
  Dunit = g/cm3
  Dvalue = 1.85
  Group = -> [H_element015,C_element015,N_element010,O_element014,Mg_element001,P_element002,S_element004,Ca_element003]
  conduct = 2
  density = 1
  expand = 3
  formula = G4_BONE_COMPACT_ICRU
  name = G4_BONE_COMPACT_ICRU
  specific = 4
FEATURE [App::DocumentObjectGroupPython] H_element016  label="H_element : 0.034"  # scripted group (container) (typed FeaturePython)
  n = 0.034
FEATURE [App::DocumentObjectGroupPython] C_element016  label="C_element : 0.155"  # scripted group (container) (typed FeaturePython)
  n = 0.155
FEATURE [App::DocumentObjectGroupPython] N_element011  label="N_element : 0.042"  # scripted group (container) (typed FeaturePython)
  n = 0.042
FEATURE [App::DocumentObjectGroupPython] O_element015  label="O_element : 0.435"  # scripted group (container) (typed FeaturePython)
  n = 0.435
FEATURE [App::DocumentObjectGroupPython] Na_element003  label="Na_element : 0.003"  # scripted group (container) (typed FeaturePython)
  n = 0.001
FEATURE [App::DocumentObjectGroupPython] Mg_element002  label="Mg_element : 0.003"  # scripted group (container) (typed FeaturePython)
  n = 0.002
FEATURE [App::DocumentObjectGroupPython] P_element003  label="P_element : 0.103"  # scripted group (container) (typed FeaturePython)
  n = 0.103
FEATURE [App::DocumentObjectGroupPython] S_element005  label="S_element : 0.004"  # scripted group (container) (typed FeaturePython)
  n = 0.003
FEATURE [App::DocumentObjectGroupPython] Ca_element004  label="Ca_element : 0.225"  # scripted group (container) (typed FeaturePython)
  n = 0.225
FEATURE [App::DocumentObjectGroupPython] G4_BONE_CORTICAL_ICRP  # scripted group (container) (typed FeaturePython)
  Dunit = g/cm3
  Dvalue = 1.92
  Group = -> [H_element016,C_element016,N_element011,O_element015,Na_element003,Mg_element002,P_element003,S_element005,Ca_element004]
  conduct = 2
  density = 1
  expand = 3
  formula = G4_BONE_CORTICAL_ICRP
  name = G4_BONE_CORTICAL_ICRP
  specific = 4
FEATURE [App::DocumentObjectGroupPython] B_element001  label="B_element : 4"  # scripted group (container) (typed FeaturePython)
  n = 4
  ref = B_element
FEATURE [App::DocumentObjectGroupPython] C_element017  label="C_element : 1"  # scripted group (container) (typed FeaturePython)
  n = 1
  ref = C_element
FEATURE [App::DocumentObjectGroupPython] G4_BORON_CARBIDE  # scripted group (container) (typed FeaturePython)
  Dunit = g/cm3
  Dvalue = 2.52
  Group = -> [B_element001,C_element017]
  conduct = 2
  density = 1
  expand = 3
  formula = G4_BORON_CARBIDE
  name = G4_BORON_CARBIDE
  specific = 4
FEATURE [App::DocumentObjectGroupPython] B_element002  label="B_element : 2"  # scripted group (container) (typed FeaturePython)
  n = 2
  ref = B_element
FEATURE [App::DocumentObjectGroupPython] O_element016  label="O_element : 006"  # scripted group (container) (typed FeaturePython)
  n = 3
  ref = O_element
FEATURE [App::DocumentObjectGroupPython] G4_BORON_OXIDE  # scripted group (container) (typed FeaturePython)
  Dunit = g/cm3
  Dvalue = 1.812
  Group = -> [B_element002,O_element016]
  conduct = 2
  density = 1
  expand = 3
  formula = G4_BORON_OXIDE
  name = G4_BORON_OXIDE
  specific = 4
FEATURE [App::DocumentObjectGroupPython] H_element017  label="H_element : 0.107"  # scripted group (container) (typed FeaturePython)
  n = 0.107
FEATURE [App::DocumentObjectGroupPython] C_element018  label="C_element : 0.145"  # scripted group (container) (typed FeaturePython)
  n = 0.145
FEATURE [App::DocumentObjectGroupPython] N_element012  label="N_element : 0.022"  # scripted group (container) (typed FeaturePython)
  n = 0.022
FEATURE [App::DocumentObjectGroupPython] O_element017  label="O_element : 0.712"  # scripted group (container) (typed FeaturePython)
  n = 0.712
FEATURE [App::DocumentObjectGroupPython] Na_element004  label="Na_element : 0.004"  # scripted group (container) (typed FeaturePython)
  n = 0.002
FEATURE [App::DocumentObjectGroupPython] P_element004  label="P_element : 0.004"  # scripted group (container) (typed FeaturePython)
  n = 0.004
FEATURE [App::DocumentObjectGroupPython] S_element006  label="S_element : 0.005"  # scripted group (container) (typed FeaturePython)
  n = 0.002
FEATURE [App::DocumentObjectGroupPython] Cl_element003  label="Cl_element : 0.004"  # scripted group (container) (typed FeaturePython)
  n = 0.003
FEATURE [App::DocumentObjectGroupPython] K_element002  label="K_element : 0.003"  # scripted group (container) (typed FeaturePython)
  n = 0.003
FEATURE [App::DocumentObjectGroupPython] G4_BRAIN_ICRP  # scripted group (container) (typed FeaturePython)
  Dunit = g/cm3
  Dvalue = 1.04
  Group = -> [H_element017,C_element018,N_element012,O_element017,Na_element004,P_element004,S_element006,Cl_element003,K_element002]
  conduct = 2
  density = 1
  expand = 3
  formula = G4_BRAIN_ICRP
  name = G4_BRAIN_ICRP
  specific = 4
FEATURE [App::DocumentObjectGroupPython] C_element019  label="C_element : 4"  # scripted group (container) (typed FeaturePython)
  n = 4
  ref = C_element
FEATURE [App::DocumentObjectGroupPython] H_element018  label="H_element : 010"  # scripted group (container) (typed FeaturePython)
  n = 10
  ref = H_element
FEATURE [App::DocumentObjectGroupPython] G4_BUTANE  # scripted group (container) (typed FeaturePython)
  Dunit = g/cm3
  Dvalue = 0.00249343
  Group = -> [C_element019,H_element018]
  conduct = 2
  density = 1
  expand = 3
  formula = G4_BUTANE
  name = G4_BUTANE
  specific = 4
FEATURE [App::DocumentObjectGroupPython] C_element020  label="C_element : 008"  # scripted group (container) (typed FeaturePython)
  n = 4
  ref = C_element
FEATURE [App::DocumentObjectGroupPython] H_element019  label="H_element : 011"  # scripted group (container) (typed FeaturePython)
  n = 10
  ref = H_element
FEATURE [App::DocumentObjectGroupPython] O_element018  label="O_element : 007"  # scripted group (container) (typed FeaturePython)
  n = 1
  ref = O_element
FEATURE [App::DocumentObjectGroupPython] G4_N_BUTYL_ALCOHOL  label="G4_N-BUTYL_ALCOHOL"  # scripted group (container) (typed FeaturePython)
  Dunit = g/cm3
  Dvalue = 0.8098
  Group = -> [C_element020,H_element019,O_element018]
  conduct = 2
  density = 1
  expand = 3
  formula = G4_N-BUTYL_ALCOHOL
  name = G4_N-BUTYL_ALCOHOL
  specific = 4
FEATURE [App::DocumentObjectGroupPython] H_element020  label="H_element : 0.025"  # scripted group (container) (typed FeaturePython)
  n = 0.02468
FEATURE [App::DocumentObjectGroupPython] C_element021  label="C_element : 0.502"  # scripted group (container) (typed FeaturePython)
  n = 0.501611
FEATURE [App::DocumentObjectGroupPython] O_element019  label="O_element : 0.005"  # scripted group (container) (typed FeaturePython)
  n = 0.004527
FEATURE [App::DocumentObjectGroupPython] F_element004  label="F_element : 0.465"  # scripted group (container) (typed FeaturePython)
  n = 0.465209
FEATURE [App::DocumentObjectGroupPython] Si_element001  label="Si_element : 0.004"  # scripted group (container) (typed FeaturePython)
  n = 0.003973
FEATURE [App::DocumentObjectGroupPython] G4_C_552  label="G4_C-552"  # scripted group (container) (typed FeaturePython)
  Dunit = g/cm3
  Dvalue = 1.76
  Group = -> [H_element020,C_element021,O_element019,F_element004,Si_element001]
  conduct = 2
  density = 1
  expand = 3
  formula = G4_C-552
  name = G4_C-552
  specific = 4
FEATURE [App::DocumentObjectGroupPython] Cd_element001  label="Cd_element : 1"  # scripted group (container) (typed FeaturePython)
  n = 1
  ref = Cd_element
FEATURE [App::DocumentObjectGroupPython] Te_element001  label="Te_element : 1"  # scripted group (container) (typed FeaturePython)
  n = 1
  ref = Te_element
FEATURE [App::DocumentObjectGroupPython] G4_CADMIUM_TELLURIDE  # scripted group (container) (typed FeaturePython)
  Dunit = g/cm3
  Dvalue = 6.2
  Group = -> [Cd_element001,Te_element001]
  conduct = 2
  density = 1
  expand = 3
  formula = G4_CADMIUM_TELLURIDE
  name = G4_CADMIUM_TELLURIDE
  specific = 4
FEATURE [App::DocumentObjectGroupPython] Cd_element002  label="Cd_element : 002"  # scripted group (container) (typed FeaturePython)
  n = 1
  ref = Cd_element
FEATURE [App::DocumentObjectGroupPython] W_element001  label="W_element : 1"  # scripted group (container) (typed FeaturePython)
  n = 1
  ref = W_element
FEATURE [App::DocumentObjectGroupPython] O_element020  label="O_element : 008"  # scripted group (container) (typed FeaturePython)
  n = 4
  ref = O_element
FEATURE [App::DocumentObjectGroupPython] G4_CADMIUM_TUNGSTATE  # scripted group (container) (typed FeaturePython)
  Dunit = g/cm3
  Dvalue = 7.9
  Group = -> [Cd_element002,W_element001,O_element020]
  conduct = 2
  density = 1
  expand = 3
  formula = G4_CADMIUM_TUNGSTATE
  name = G4_CADMIUM_TUNGSTATE
  specific = 4
FEATURE [App::DocumentObjectGroupPython] Ca_element005  label="Ca_element : 1"  # scripted group (container) (typed FeaturePython)
  n = 1
  ref = Ca_element
FEATURE [App::DocumentObjectGroupPython] C_element022  label="C_element : 009"  # scripted group (container) (typed FeaturePython)
  n = 1
  ref = C_element
FEATURE [App::DocumentObjectGroupPython] O_element021  label="O_element : 009"  # scripted group (container) (typed FeaturePython)
  n = 3
  ref = O_element
FEATURE [App::DocumentObjectGroupPython] G4_CALCIUM_CARBONATE  # scripted group (container) (typed FeaturePython)
  Dunit = g/cm3
  Dvalue = 2.8
  Group = -> [Ca_element005,C_element022,O_element021]
  conduct = 2
  density = 1
  expand = 3
  formula = G4_CALCIUM_CARBONATE
  name = G4_CALCIUM_CARBONATE
  specific = 4
FEATURE [App::DocumentObjectGroupPython] Ca_element006  label="Ca_element : 002"  # scripted group (container) (typed FeaturePython)
  n = 1
  ref = Ca_element
FEATURE [App::DocumentObjectGroupPython] F_element005  label="F_element : 003"  # scripted group (container) (typed FeaturePython)
  n = 2
  ref = F_element
FEATURE [App::DocumentObjectGroupPython] G4_CALCIUM_FLUORIDE  # scripted group (container) (typed FeaturePython)
  Dunit = g/cm3
  Dvalue = 3.18
  Group = -> [Ca_element006,F_element005]
  conduct = 2
  density = 1
  expand = 3
  formula = G4_CALCIUM_FLUORIDE
  name = G4_CALCIUM_FLUORIDE
  specific = 4
FEATURE [App::DocumentObjectGroupPython] Ca_element007  label="Ca_element : 003"  # scripted group (container) (typed FeaturePython)
  n = 1
  ref = Ca_element
FEATURE [App::DocumentObjectGroupPython] O_element022  label="O_element : 010"  # scripted group (container) (typed FeaturePython)
  n = 1
  ref = O_element
FEATURE [App::DocumentObjectGroupPython] G4_CALCIUM_OXIDE  # scripted group (container) (typed FeaturePython)
  Dunit = g/cm3
  Dvalue = 3.3
  Group = -> [Ca_element007,O_element022]
  conduct = 2
  density = 1
  expand = 3
  formula = G4_CALCIUM_OXIDE
  name = G4_CALCIUM_OXIDE
  specific = 4
FEATURE [App::DocumentObjectGroupPython] Ca_element008  label="Ca_element : 004"  # scripted group (container) (typed FeaturePython)
  n = 1
  ref = Ca_element
FEATURE [App::DocumentObjectGroupPython] S_element007  label="S_element : 002"  # scripted group (container) (typed FeaturePython)
  n = 1
  ref = S_element
FEATURE [App::DocumentObjectGroupPython] O_element023  label="O_element : 011"  # scripted group (container) (typed FeaturePython)
  n = 4
  ref = O_element
FEATURE [App::DocumentObjectGroupPython] G4_CALCIUM_SULFATE  # scripted group (container) (typed FeaturePython)
  Dunit = g/cm3
  Dvalue = 2.96
  Group = -> [Ca_element008,S_element007,O_element023]
  conduct = 2
  density = 1
  expand = 3
  formula = G4_CALCIUM_SULFATE
  name = G4_CALCIUM_SULFATE
  specific = 4
FEATURE [App::DocumentObjectGroupPython] Ca_element009  label="Ca_element : 005"  # scripted group (container) (typed FeaturePython)
  n = 1
  ref = Ca_element
FEATURE [App::DocumentObjectGroupPython] W_element002  label="W_element : 002"  # scripted group (container) (typed FeaturePython)
  n = 1
  ref = W_element
FEATURE [App::DocumentObjectGroupPython] O_element024  label="O_element : 012"  # scripted group (container) (typed FeaturePython)
  n = 4
  ref = O_element
FEATURE [App::DocumentObjectGroupPython] G4_CALCIUM_TUNGSTATE  # scripted group (container) (typed FeaturePython)
  Dunit = g/cm3
  Dvalue = 6.062
  Group = -> [Ca_element009,W_element002,O_element024]
  conduct = 2
  density = 1
  expand = 3
  formula = G4_CALCIUM_TUNGSTATE
  name = G4_CALCIUM_TUNGSTATE
  specific = 4
FEATURE [App::DocumentObjectGroupPython] C_element023  label="C_element : 010"  # scripted group (container) (typed FeaturePython)
  n = 1
  ref = C_element
FEATURE [App::DocumentObjectGroupPython] O_element025  label="O_element : 013"  # scripted group (container) (typed FeaturePython)
  n = 2
  ref = O_element
FEATURE [App::DocumentObjectGroupPython] G4_CARBON_DIOXIDE  # scripted group (container) (typed FeaturePython)
  Dunit = g/cm3
  Dvalue = 0.00184212
  Group = -> [C_element023,O_element025]
  conduct = 2
  density = 1
  expand = 3
  formula = G4_CARBON_DIOXIDE
  name = G4_CARBON_DIOXIDE
  specific = 4
FEATURE [App::DocumentObjectGroupPython] C_element024  label="C_element : 011"  # scripted group (container) (typed FeaturePython)
  n = 1
  ref = C_element
FEATURE [App::DocumentObjectGroupPython] Cl_element004  label="Cl_element : 4"  # scripted group (container) (typed FeaturePython)
  n = 4
  ref = Cl_element
FEATURE [App::DocumentObjectGroupPython] G4_CARBON_TETRACHLORIDE  # scripted group (container) (typed FeaturePython)
  Dunit = g/cm3
  Dvalue = 1.594
  Group = -> [C_element024,Cl_element004]
  conduct = 2
  density = 1
  expand = 3
  formula = G4_CARBON_TETRACHLORIDE
  name = G4_CARBON_TETRACHLORIDE
  specific = 4
FEATURE [App::DocumentObjectGroupPython] C_element025  label="C_element : 012"  # scripted group (container) (typed FeaturePython)
  n = 6
  ref = C_element
FEATURE [App::DocumentObjectGroupPython] H_element021  label="H_element : 012"  # scripted group (container) (typed FeaturePython)
  n = 10
  ref = H_element
FEATURE [App::DocumentObjectGroupPython] O_element026  label="O_element : 5"  # scripted group (container) (typed FeaturePython)
  n = 5
  ref = O_element
FEATURE [App::DocumentObjectGroupPython] G4_CELLULOSE_CELLOPHANE  # scripted group (container) (typed FeaturePython)
  Dunit = g/cm3
  Dvalue = 1.42
  Group = -> [C_element025,H_element021,O_element026]
  conduct = 2
  density = 1
  expand = 3
  formula = G4_CELLULOSE_CELLOPHANE
  name = G4_CELLULOSE_CELLOPHANE
  specific = 4
FEATURE [App::DocumentObjectGroupPython] H_element022  label="H_element : 0.067"  # scripted group (container) (typed FeaturePython)
  n = 0.067125
FEATURE [App::DocumentObjectGroupPython] C_element026  label="C_element : 0.545"  # scripted group (container) (typed FeaturePython)
  n = 0.545403
FEATURE [App::DocumentObjectGroupPython] O_element027  label="O_element : 0.387"  # scripted group (container) (typed FeaturePython)
  n = 0.387472
FEATURE [App::DocumentObjectGroupPython] G4_CELLULOSE_BUTYRATE  # scripted group (container) (typed FeaturePython)
  Dunit = g/cm3
  Dvalue = 1.2
  Group = -> [H_element022,C_element026,O_element027]
  conduct = 2
  density = 1
  expand = 3
  formula = G4_CELLULOSE_BUTYRATE
  name = G4_CELLULOSE_BUTYRATE
  specific = 4
FEATURE [App::DocumentObjectGroupPython] H_element023  label="H_element : 0.029"  # scripted group (container) (typed FeaturePython)
  n = 0.029216
FEATURE [App::DocumentObjectGroupPython] C_element027  label="C_element : 0.271"  # scripted group (container) (typed FeaturePython)
  n = 0.271296
FEATURE [App::DocumentObjectGroupPython] N_element013  label="N_element : 0.121"  # scripted group (container) (typed FeaturePython)
  n = 0.121276
FEATURE [App::DocumentObjectGroupPython] O_element028  label="O_element : 0.578"  # scripted group (container) (typed FeaturePython)
  n = 0.578212
FEATURE [App::DocumentObjectGroupPython] G4_CELLULOSE_NITRATE  # scripted group (container) (typed FeaturePython)
  Dunit = g/cm3
  Dvalue = 1.49
  Group = -> [H_element023,C_element027,N_element013,O_element028]
  conduct = 2
  density = 1
  expand = 3
  formula = G4_CELLULOSE_NITRATE
  name = G4_CELLULOSE_NITRATE
  specific = 4
FEATURE [App::DocumentObjectGroupPython] H_element024  label="H_element : 0.108"  # scripted group (container) (typed FeaturePython)
  n = 0.107596
FEATURE [App::DocumentObjectGroupPython] N_element014  label="N_element : 0.001"  # scripted group (container) (typed FeaturePython)
  n = 0.0008
FEATURE [App::DocumentObjectGroupPython] O_element029  label="O_element : 0.875"  # scripted group (container) (typed FeaturePython)
  n = 0.874976
FEATURE [App::DocumentObjectGroupPython] S_element008  label="S_element : 0.015"  # scripted group (container) (typed FeaturePython)
  n = 0.014627
FEATURE [App::DocumentObjectGroupPython] Ce_element001  label="Ce_element : 0.002"  # scripted group (container) (typed FeaturePython)
  n = 0.002001
FEATURE [App::DocumentObjectGroupPython] G4_CERIC_SULFATE  # scripted group (container) (typed FeaturePython)
  Dunit = g/cm3
  Dvalue = 1.03
  Group = -> [H_element024,N_element014,O_element029,S_element008,Ce_element001]
  conduct = 2
  density = 1
  expand = 3
  formula = G4_CERIC_SULFATE
  name = G4_CERIC_SULFATE
  specific = 4
FEATURE [App::DocumentObjectGroupPython] Cs_element001  label="Cs_element : 1"  # scripted group (container) (typed FeaturePython)
  n = 1
  ref = Cs_element
FEATURE [App::DocumentObjectGroupPython] F_element006  label="F_element : 1"  # scripted group (container) (typed FeaturePython)
  n = 1
  ref = F_element
FEATURE [App::DocumentObjectGroupPython] G4_CESIUM_FLUORIDE  # scripted group (container) (typed FeaturePython)
  Dunit = g/cm3
  Dvalue = 4.115
  Group = -> [Cs_element001,F_element006]
  conduct = 2
  density = 1
  expand = 3
  formula = G4_CESIUM_FLUORIDE
  name = G4_CESIUM_FLUORIDE
  specific = 4
FEATURE [App::DocumentObjectGroupPython] Cs_element002  label="Cs_element : 002"  # scripted group (container) (typed FeaturePython)
  n = 1
  ref = Cs_element
FEATURE [App::DocumentObjectGroupPython] I_element001  label="I_element : 1"  # scripted group (container) (typed FeaturePython)
  n = 1
  ref = I_element
FEATURE [App::DocumentObjectGroupPython] G4_CESIUM_IODIDE  # scripted group (container) (typed FeaturePython)
  Dunit = g/cm3
  Dvalue = 4.51
  Group = -> [Cs_element002,I_element001]
  conduct = 2
  density = 1
  expand = 3
  formula = G4_CESIUM_IODIDE
  name = G4_CESIUM_IODIDE
  specific = 4
FEATURE [App::DocumentObjectGroupPython] C_element028  label="C_element : 013"  # scripted group (container) (typed FeaturePython)
  n = 6
  ref = C_element
FEATURE [App::DocumentObjectGroupPython] H_element025  label="H_element : 013"  # scripted group (container) (typed FeaturePython)
  n = 5
  ref = H_element
FEATURE [App::DocumentObjectGroupPython] Cl_element005  label="Cl_element : 1"  # scripted group (container) (typed FeaturePython)
  n = 1
  ref = Cl_element
FEATURE [App::DocumentObjectGroupPython] G4_CHLOROBENZENE  # scripted group (container) (typed FeaturePython)
  Dunit = g/cm3
  Dvalue = 1.1058
  Group = -> [C_element028,H_element025,Cl_element005]
  conduct = 2
  density = 1
  expand = 3
  formula = G4_CHLOROBENZENE
  name = G4_CHLOROBENZENE
  specific = 4
FEATURE [App::DocumentObjectGroupPython] C_element029  label="C_element : 014"  # scripted group (container) (typed FeaturePython)
  n = 1
  ref = C_element
FEATURE [App::DocumentObjectGroupPython] H_element026  label="H_element : 1"  # scripted group (container) (typed FeaturePython)
  n = 1
  ref = H_element
FEATURE [App::DocumentObjectGroupPython] Cl_element006  label="Cl_element : 3"  # scripted group (container) (typed FeaturePython)
  n = 3
  ref = Cl_element
FEATURE [App::DocumentObjectGroupPython] G4_CHLOROFORM  # scripted group (container) (typed FeaturePython)
  Dunit = g/cm3
  Dvalue = 1.4832
  Group = -> [C_element029,H_element026,Cl_element006]
  conduct = 2
  density = 1
  expand = 3
  formula = G4_CHLOROFORM
  name = G4_CHLOROFORM
  specific = 4
FEATURE [App::DocumentObjectGroupPython] H_element027  label="H_element : 0.010"  # scripted group (container) (typed FeaturePython)
  n = 0.01
FEATURE [App::DocumentObjectGroupPython] C_element030  label="C_element : 0.001"  # scripted group (container) (typed FeaturePython)
  n = 0.001
FEATURE [App::DocumentObjectGroupPython] O_element030  label="O_element : 0.529"  # scripted group (container) (typed FeaturePython)
  n = 0.529107
FEATURE [App::DocumentObjectGroupPython] Na_element005  label="Na_element : 0.016"  # scripted group (container) (typed FeaturePython)
  n = 0.016
FEATURE [App::DocumentObjectGroupPython] Mg_element003  label="Mg_element : 0.004"  # scripted group (container) (typed FeaturePython)
  n = 0.002
FEATURE [App::DocumentObjectGroupPython] Al_element002  label="Al_element : 0.034"  # scripted group (container) (typed FeaturePython)
  n = 0.033872
FEATURE [App::DocumentObjectGroupPython] Si_element002  label="Si_element : 0.337"  # scripted group (container) (typed FeaturePython)
  n = 0.337021
FEATURE [App::DocumentObjectGroupPython] K_element003  label="K_element : 0.013"  # scripted group (container) (typed FeaturePython)
  n = 0.013
FEATURE [App::DocumentObjectGroupPython] Ca_element010  label="Ca_element : 0.044"  # scripted group (container) (typed FeaturePython)
  n = 0.044
FEATURE [App::DocumentObjectGroupPython] Fe_element002  label="Fe_element : 0.014"  # scripted group (container) (typed FeaturePython)
  n = 0.014
FEATURE [App::DocumentObjectGroupPython] G4_CONCRETE  # scripted group (container) (typed FeaturePython)
  Dunit = g/cm3
  Dvalue = 2.3
  Group = -> [H_element027,C_element030,O_element030,Na_element005,Mg_element003,Al_element002,Si_element002,K_element003,Ca_element010,Fe_element002]
  conduct = 2
  density = 1
  expand = 3
  formula = G4_CONCRETE
  name = G4_CONCRETE
  specific = 4
FEATURE [App::DocumentObjectGroupPython] C_element031  label="C_element : 015"  # scripted group (container) (typed FeaturePython)
  n = 6
  ref = C_element
FEATURE [App::DocumentObjectGroupPython] H_element028  label="H_element : 12"  # scripted group (container) (typed FeaturePython)
  n = 12
  ref = H_element
FEATURE [App::DocumentObjectGroupPython] G4_CYCLOHEXANE  # scripted group (container) (typed FeaturePython)
  Dunit = g/cm3
  Dvalue = 0.779
  Group = -> [C_element031,H_element028]
  conduct = 2
  density = 1
  expand = 3
  formula = G4_CYCLOHEXANE
  name = G4_CYCLOHEXANE
  specific = 4
FEATURE [App::DocumentObjectGroupPython] C_element032  label="C_element : 016"  # scripted group (container) (typed FeaturePython)
  n = 6
  ref = C_element
FEATURE [App::DocumentObjectGroupPython] H_element029  label="H_element : 4"  # scripted group (container) (typed FeaturePython)
  n = 4
  ref = H_element
FEATURE [App::DocumentObjectGroupPython] Cl_element007  label="Cl_element : 2"  # scripted group (container) (typed FeaturePython)
  n = 2
  ref = Cl_element
FEATURE [App::DocumentObjectGroupPython] G4_1_2_DICHLOROBENZENE  label="G4_1.2-DICHLOROBENZENE"  # scripted group (container) (typed FeaturePython)
  Dunit = g/cm3
  Dvalue = 1.3048
  Group = -> [C_element032,H_element029,Cl_element007]
  conduct = 2
  density = 1
  expand = 3
  formula = G4_1.2-DICHLOROBENZENE
  name = G4_1.2-DICHLOROBENZENE
  specific = 4
FEATURE [App::DocumentObjectGroupPython] C_element033  label="C_element : 017"  # scripted group (container) (typed FeaturePython)
  n = 4
  ref = C_element
FEATURE [App::DocumentObjectGroupPython] H_element030  label="H_element : 8"  # scripted group (container) (typed FeaturePython)
  n = 8
  ref = H_element
FEATURE [App::DocumentObjectGroupPython] O_element031  label="O_element : 014"  # scripted group (container) (typed FeaturePython)
  n = 1
  ref = O_element
FEATURE [App::DocumentObjectGroupPython] Cl_element008  label="Cl_element : 005"  # scripted group (container) (typed FeaturePython)
  n = 2
  ref = Cl_element
FEATURE [App::DocumentObjectGroupPython] G4_DICHLORODIETHYL_ETHER  # scripted group (container) (typed FeaturePython)
  Dunit = g/cm3
  Dvalue = 1.2199
  Group = -> [C_element033,H_element030,O_element031,Cl_element008]
  conduct = 2
  density = 1
  expand = 3
  formula = G4_DICHLORODIETHYL_ETHER
  name = G4_DICHLORODIETHYL_ETHER
  specific = 4
FEATURE [App::DocumentObjectGroupPython] C_element034  label="C_element : 018"  # scripted group (container) (typed FeaturePython)
  n = 2
  ref = C_element
FEATURE [App::DocumentObjectGroupPython] H_element031  label="H_element : 014"  # scripted group (container) (typed FeaturePython)
  n = 4
  ref = H_element
FEATURE [App::DocumentObjectGroupPython] Cl_element009  label="Cl_element : 006"  # scripted group (container) (typed FeaturePython)
  n = 2
  ref = Cl_element
FEATURE [App::DocumentObjectGroupPython] G4_1_2_DICHLOROETHANE  label="G4_1.2-DICHLOROETHANE"  # scripted group (container) (typed FeaturePython)
  Dunit = g/cm3
  Dvalue = 1.2351
  Group = -> [C_element034,H_element031,Cl_element009]
  conduct = 2
  density = 1
  expand = 3
  formula = G4_1.2-DICHLOROETHANE
  name = G4_1.2-DICHLOROETHANE
  specific = 4
FEATURE [App::DocumentObjectGroupPython] C_element035  label="C_element : 019"  # scripted group (container) (typed FeaturePython)
  n = 4
  ref = C_element
FEATURE [App::DocumentObjectGroupPython] H_element032  label="H_element : 015"  # scripted group (container) (typed FeaturePython)
  n = 10
  ref = H_element
FEATURE [App::DocumentObjectGroupPython] O_element032  label="O_element : 015"  # scripted group (container) (typed FeaturePython)
  n = 1
  ref = O_element
FEATURE [App::DocumentObjectGroupPython] G4_DIETHYL_ETHER  # scripted group (container) (typed FeaturePython)
  Dunit = g/cm3
  Dvalue = 0.71378
  Group = -> [C_element035,H_element032,O_element032]
  conduct = 2
  density = 1
  expand = 3
  formula = G4_DIETHYL_ETHER
  name = G4_DIETHYL_ETHER
  specific = 4
FEATURE [App::DocumentObjectGroupPython] C_element036  label="C_element : 020"  # scripted group (container) (typed FeaturePython)
  n = 3
  ref = C_element
FEATURE [App::DocumentObjectGroupPython] H_element033  label="H_element : 016"  # scripted group (container) (typed FeaturePython)
  n = 7
  ref = H_element
FEATURE [App::DocumentObjectGroupPython] N_element015  label="N_element : 008"  # scripted group (container) (typed FeaturePython)
  n = 1
  ref = N_element
FEATURE [App::DocumentObjectGroupPython] O_element033  label="O_element : 016"  # scripted group (container) (typed FeaturePython)
  n = 1
  ref = O_element
FEATURE [App::DocumentObjectGroupPython] G4_N_N_DIMETHYL_FORMAMIDE  label="G4_N.N-DIMETHYL_FORMAMIDE"  # scripted group (container) (typed FeaturePython)
  Dunit = g/cm3
  Dvalue = 0.9487
  Group = -> [C_element036,H_element033,N_element015,O_element033]
  conduct = 2
  density = 1
  expand = 3
  formula = G4_N.N-DIMETHYL_FORMAMIDE
  name = G4_N.N-DIMETHYL_FORMAMIDE
  specific = 4
FEATURE [App::DocumentObjectGroupPython] C_element037  label="C_element : 021"  # scripted group (container) (typed FeaturePython)
  n = 2
  ref = C_element
FEATURE [App::DocumentObjectGroupPython] H_element034  label="H_element : 017"  # scripted group (container) (typed FeaturePython)
  n = 6
  ref = H_element
FEATURE [App::DocumentObjectGroupPython] O_element034  label="O_element : 017"  # scripted group (container) (typed FeaturePython)
  n = 1
  ref = O_element
FEATURE [App::DocumentObjectGroupPython] S_element009  label="S_element : 003"  # scripted group (container) (typed FeaturePython)
  n = 1
  ref = S_element
FEATURE [App::DocumentObjectGroupPython] G4_DIMETHYL_SULFOXIDE  # scripted group (container) (typed FeaturePython)
  Dunit = g/cm3
  Dvalue = 1.1014
  Group = -> [C_element037,H_element034,O_element034,S_element009]
  conduct = 2
  density = 1
  expand = 3
  formula = G4_DIMETHYL_SULFOXIDE
  name = G4_DIMETHYL_SULFOXIDE
  specific = 4
FEATURE [App::DocumentObjectGroupPython] C_element038  label="C_element : 022"  # scripted group (container) (typed FeaturePython)
  n = 2
  ref = C_element
FEATURE [App::DocumentObjectGroupPython] H_element035  label="H_element : 018"  # scripted group (container) (typed FeaturePython)
  n = 6
  ref = H_element
FEATURE [App::DocumentObjectGroupPython] G4_ETHANE  # scripted group (container) (typed FeaturePython)
  Dunit = g/cm3
  Dvalue = 0.00125324
  Group = -> [C_element038,H_element035]
  conduct = 2
  density = 1
  expand = 3
  formula = G4_ETHANE
  name = G4_ETHANE
  specific = 4
FEATURE [App::DocumentObjectGroupPython] C_element039  label="C_element : 023"  # scripted group (container) (typed FeaturePython)
  n = 2
  ref = C_element
FEATURE [App::DocumentObjectGroupPython] H_element036  label="H_element : 019"  # scripted group (container) (typed FeaturePython)
  n = 6
  ref = H_element
FEATURE [App::DocumentObjectGroupPython] O_element035  label="O_element : 018"  # scripted group (container) (typed FeaturePython)
  n = 1
  ref = O_element
FEATURE [App::DocumentObjectGroupPython] G4_ETHYL_ALCOHOL  # scripted group (container) (typed FeaturePython)
  Dunit = g/cm3
  Dvalue = 0.7893
  Group = -> [C_element039,H_element036,O_element035]
  conduct = 2
  density = 1
  expand = 3
  formula = G4_ETHYL_ALCOHOL
  name = G4_ETHYL_ALCOHOL
  specific = 4
FEATURE [App::DocumentObjectGroupPython] H_element037  label="H_element : 0.090"  # scripted group (container) (typed FeaturePython)
  n = 0.090027
FEATURE [App::DocumentObjectGroupPython] C_element040  label="C_element : 0.585"  # scripted group (container) (typed FeaturePython)
  n = 0.585182
FEATURE [App::DocumentObjectGroupPython] O_element036  label="O_element : 0.325"  # scripted group (container) (typed FeaturePython)
  n = 0.324791
FEATURE [App::DocumentObjectGroupPython] G4_ETHYL_CELLULOSE  # scripted group (container) (typed FeaturePython)
  Dunit = g/cm3
  Dvalue = 1.13
  Group = -> [H_element037,C_element040,O_element036]
  conduct = 2
  density = 1
  expand = 3
  formula = G4_ETHYL_CELLULOSE
  name = G4_ETHYL_CELLULOSE
  specific = 4
FEATURE [App::DocumentObjectGroupPython] C_element041  label="C_element : 024"  # scripted group (container) (typed FeaturePython)
  n = 2
  ref = C_element
FEATURE [App::DocumentObjectGroupPython] H_element038  label="H_element : 020"  # scripted group (container) (typed FeaturePython)
  n = 4
  ref = H_element
FEATURE [App::DocumentObjectGroupPython] G4_ETHYLENE  # scripted group (container) (typed FeaturePython)
  Dunit = g/cm3
  Dvalue = 0.00117497
  Group = -> [C_element041,H_element038]
  conduct = 2
  density = 1
  expand = 3
  formula = G4_ETHYLENE
  name = G4_ETHYLENE
  specific = 4
FEATURE [App::DocumentObjectGroupPython] H_element039  label="H_element : 0.096"  # scripted group (container) (typed FeaturePython)
  n = 0.096
FEATURE [App::DocumentObjectGroupPython] C_element042  label="C_element : 0.195"  # scripted group (container) (typed FeaturePython)
  n = 0.195
FEATURE [App::DocumentObjectGroupPython] N_element016  label="N_element : 0.057"  # scripted group (container) (typed FeaturePython)
  n = 0.057
FEATURE [App::DocumentObjectGroupPython] O_element037  label="O_element : 0.646"  # scripted group (container) (typed FeaturePython)
  n = 0.646
FEATURE [App::DocumentObjectGroupPython] Na_element006  label="Na_element : 0.017"  # scripted group (container) (typed FeaturePython)
  n = 0.001
FEATURE [App::DocumentObjectGroupPython] P_element005  label="P_element : 0.104"  # scripted group (container) (typed FeaturePython)
  n = 0.001
FEATURE [App::DocumentObjectGroupPython] S_element010  label="S_element : 0.016"  # scripted group (container) (typed FeaturePython)
  n = 0.003
FEATURE [App::DocumentObjectGroupPython] Cl_element010  label="Cl_element : 0.005"  # scripted group (container) (typed FeaturePython)
  n = 0.001
FEATURE [App::DocumentObjectGroupPython] G4_EYE_LENS_ICRP  # scripted group (container) (typed FeaturePython)
  Dunit = g/cm3
  Dvalue = 1.07
  Group = -> [H_element039,C_element042,N_element016,O_element037,Na_element006,P_element005,S_element010,Cl_element010]
  conduct = 2
  density = 1
  expand = 3
  formula = G4_EYE_LENS_ICRP
  name = G4_EYE_LENS_ICRP
  specific = 4
FEATURE [App::DocumentObjectGroupPython] Fe_element003  label="Fe_element : 2"  # scripted group (container) (typed FeaturePython)
  n = 2
  ref = Fe_element
FEATURE [App::DocumentObjectGroupPython] O_element038  label="O_element : 019"  # scripted group (container) (typed FeaturePython)
  n = 3
  ref = O_element
FEATURE [App::DocumentObjectGroupPython] G4_FERRIC_OXIDE  # scripted group (container) (typed FeaturePython)
  Dunit = g/cm3
  Dvalue = 5.2
  Group = -> [Fe_element003,O_element038]
  conduct = 2
  density = 1
  expand = 3
  formula = G4_FERRIC_OXIDE
  name = G4_FERRIC_OXIDE
  specific = 4
FEATURE [App::DocumentObjectGroupPython] Fe_element004  label="Fe_element : 1"  # scripted group (container) (typed FeaturePython)
  n = 1
  ref = Fe_element
FEATURE [App::DocumentObjectGroupPython] B_element003  label="B_element : 1"  # scripted group (container) (typed FeaturePython)
  n = 1
  ref = B_element
FEATURE [App::DocumentObjectGroupPython] G4_FERROBORIDE  # scripted group (container) (typed FeaturePython)
  Dunit = g/cm3
  Dvalue = 7.15
  Group = -> [Fe_element004,B_element003]
  conduct = 2
  density = 1
  expand = 3
  formula = G4_FERROBORIDE
  name = G4_FERROBORIDE
  specific = 4
FEATURE [App::DocumentObjectGroupPython] Fe_element005  label="Fe_element : 003"  # scripted group (container) (typed FeaturePython)
  n = 1
  ref = Fe_element
FEATURE [App::DocumentObjectGroupPython] O_element039  label="O_element : 020"  # scripted group (container) (typed FeaturePython)
  n = 1
  ref = O_element
FEATURE [App::DocumentObjectGroupPython] G4_FERROUS_OXIDE  # scripted group (container) (typed FeaturePython)
  Dunit = g/cm3
  Dvalue = 5.7
  Group = -> [Fe_element005,O_element039]
  conduct = 2
  density = 1
  expand = 3
  formula = G4_FERROUS_OXIDE
  name = G4_FERROUS_OXIDE
  specific = 4
FEATURE [App::DocumentObjectGroupPython] H_element040  label="H_element : 0.115"  # scripted group (container) (typed FeaturePython)
  n = 0.108259
FEATURE [App::DocumentObjectGroupPython] N_element017  label="N_element : 0.000"  # scripted group (container) (typed FeaturePython)
  n = 2.7e-05
FEATURE [App::DocumentObjectGroupPython] O_element040  label="O_element : 0.879"  # scripted group (container) (typed FeaturePython)
  n = 0.878636
FEATURE [App::DocumentObjectGroupPython] Na_element007  label="Na_element : 0.000"  # scripted group (container) (typed FeaturePython)
  n = 2.2e-05
FEATURE [App::DocumentObjectGroupPython] S_element011  label="S_element : 0.013"  # scripted group (container) (typed FeaturePython)
  n = 0.012968
FEATURE [App::DocumentObjectGroupPython] Cl_element011  label="Cl_element : 0.000"  # scripted group (container) (typed FeaturePython)
  n = 3.4e-05
FEATURE [App::DocumentObjectGroupPython] Fe_element006  label="Fe_element : 0.000"  # scripted group (container) (typed FeaturePython)
  n = 5.4e-05
FEATURE [App::DocumentObjectGroupPython] G4_FERROUS_SULFATE  # scripted group (container) (typed FeaturePython)
  Dunit = g/cm3
  Dvalue = 1.024
  Group = -> [H_element040,N_element017,O_element040,Na_element007,S_element011,Cl_element011,Fe_element006]
  conduct = 2
  density = 1
  expand = 3
  formula = G4_FERROUS_SULFATE
  name = G4_FERROUS_SULFATE
  specific = 4
FEATURE [App::DocumentObjectGroupPython] C_element043  label="C_element : 0.099"  # scripted group (container) (typed FeaturePython)
  n = 0.099335
FEATURE [App::DocumentObjectGroupPython] F_element007  label="F_element : 0.314"  # scripted group (container) (typed FeaturePython)
  n = 0.314247
FEATURE [App::DocumentObjectGroupPython] Cl_element012  label="Cl_element : 0.586"  # scripted group (container) (typed FeaturePython)
  n = 0.586418
FEATURE [App::DocumentObjectGroupPython] G4_FREON_12  label="G4_FREON-12"  # scripted group (container) (typed FeaturePython)
  Dunit = g/cm3
  Dvalue = 1.12
  Group = -> [C_element043,F_element007,Cl_element012]
  conduct = 2
  density = 1
  expand = 3
  formula = G4_FREON-12
  name = G4_FREON-12
  specific = 4
FEATURE [App::DocumentObjectGroupPython] C_element044  label="C_element : 0.057"  # scripted group (container) (typed FeaturePython)
  n = 0.057245
FEATURE [App::DocumentObjectGroupPython] F_element008  label="F_element : 0.181"  # scripted group (container) (typed FeaturePython)
  n = 0.181096
FEATURE [App::DocumentObjectGroupPython] Br_element001  label="Br_element : 0.762"  # scripted group (container) (typed FeaturePython)
  n = 0.761659
FEATURE [App::DocumentObjectGroupPython] G4_FREON_12B2  label="G4_FREON-12B2"  # scripted group (container) (typed FeaturePython)
  Dunit = g/cm3
  Dvalue = 1.8
  Group = -> [C_element044,F_element008,Br_element001]
  conduct = 2
  density = 1
  expand = 3
  formula = G4_FREON-12B2
  name = G4_FREON-12B2
  specific = 4
FEATURE [App::DocumentObjectGroupPython] C_element045  label="C_element : 0.115"  # scripted group (container) (typed FeaturePython)
  n = 0.114983
FEATURE [App::DocumentObjectGroupPython] F_element009  label="F_element : 0.546"  # scripted group (container) (typed FeaturePython)
  n = 0.545621
FEATURE [App::DocumentObjectGroupPython] Cl_element013  label="Cl_element : 0.339"  # scripted group (container) (typed FeaturePython)
  n = 0.339396
FEATURE [App::DocumentObjectGroupPython] G4_FREON_13  label="G4_FREON-13"  # scripted group (container) (typed FeaturePython)
  Dunit = g/cm3
  Dvalue = 0.95
  Group = -> [C_element045,F_element009,Cl_element013]
  conduct = 2
  density = 1
  expand = 3
  formula = G4_FREON-13
  name = G4_FREON-13
  specific = 4
FEATURE [App::DocumentObjectGroupPython] C_element046  label="C_element : 025"  # scripted group (container) (typed FeaturePython)
  n = 1
  ref = C_element
FEATURE [App::DocumentObjectGroupPython] F_element010  label="F_element : 3"  # scripted group (container) (typed FeaturePython)
  n = 3
  ref = F_element
FEATURE [App::DocumentObjectGroupPython] Br_element002  label="Br_element : 1"  # scripted group (container) (typed FeaturePython)
  n = 1
  ref = Br_element
FEATURE [App::DocumentObjectGroupPython] G4_FREON_13B1  label="G4_FREON-13B1"  # scripted group (container) (typed FeaturePython)
  Dunit = g/cm3
  Dvalue = 1.5
  Group = -> [C_element046,F_element010,Br_element002]
  conduct = 2
  density = 1
  expand = 3
  formula = G4_FREON-13B1
  name = G4_FREON-13B1
  specific = 4
FEATURE [App::DocumentObjectGroupPython] C_element047  label="C_element : 0.061"  # scripted group (container) (typed FeaturePython)
  n = 0.061309
FEATURE [App::DocumentObjectGroupPython] F_element011  label="F_element : 0.291"  # scripted group (container) (typed FeaturePython)
  n = 0.290924
FEATURE [App::DocumentObjectGroupPython] I_element002  label="I_element : 0.648"  # scripted group (container) (typed FeaturePython)
  n = 0.647767
FEATURE [App::DocumentObjectGroupPython] G4_FREON_13I1  label="G4_FREON-13I1"  # scripted group (container) (typed FeaturePython)
  Dunit = g/cm3
  Dvalue = 1.8
  Group = -> [C_element047,F_element011,I_element002]
  conduct = 2
  density = 1
  expand = 3
  formula = G4_FREON-13I1
  name = G4_FREON-13I1
  specific = 4
FEATURE [App::DocumentObjectGroupPython] Gd_element001  label="Gd_element : 2"  # scripted group (container) (typed FeaturePython)
  n = 2
  ref = Gd_element
FEATURE [App::DocumentObjectGroupPython] O_element041  label="O_element : 021"  # scripted group (container) (typed FeaturePython)
  n = 2
  ref = O_element
FEATURE [App::DocumentObjectGroupPython] S_element012  label="S_element : 004"  # scripted group (container) (typed FeaturePython)
  n = 1
  ref = S_element
FEATURE [App::DocumentObjectGroupPython] G4_GADOLINIUM_OXYSULFIDE  # scripted group (container) (typed FeaturePython)
  Dunit = g/cm3
  Dvalue = 7.44
  Group = -> [Gd_element001,O_element041,S_element012]
  conduct = 2
  density = 1
  expand = 3
  formula = G4_GADOLINIUM_OXYSULFIDE
  name = G4_GADOLINIUM_OXYSULFIDE
  specific = 4
FEATURE [App::DocumentObjectGroupPython] Ga_element001  label="Ga_element : 1"  # scripted group (container) (typed FeaturePython)
  n = 1
  ref = Ga_element
FEATURE [App::DocumentObjectGroupPython] As_element001  label="As_element : 1"  # scripted group (container) (typed FeaturePython)
  n = 1
  ref = As_element
FEATURE [App::DocumentObjectGroupPython] G4_GALLIUM_ARSENIDE  # scripted group (container) (typed FeaturePython)
  Dunit = g/cm3
  Dvalue = 5.31
  Group = -> [Ga_element001,As_element001]
  conduct = 2
  density = 1
  expand = 3
  formula = G4_GALLIUM_ARSENIDE
  name = G4_GALLIUM_ARSENIDE
  specific = 4
FEATURE [App::DocumentObjectGroupPython] H_element041  label="H_element : 0.081"  # scripted group (container) (typed FeaturePython)
  n = 0.08118
FEATURE [App::DocumentObjectGroupPython] C_element048  label="C_element : 0.416"  # scripted group (container) (typed FeaturePython)
  n = 0.41606
FEATURE [App::DocumentObjectGroupPython] N_element018  label="N_element : 0.111"  # scripted group (container) (typed FeaturePython)
  n = 0.11124
FEATURE [App::DocumentObjectGroupPython] O_element042  label="O_element : 0.381"  # scripted group (container) (typed FeaturePython)
  n = 0.38064
FEATURE [App::DocumentObjectGroupPython] S_element013  label="S_element : 0.011"  # scripted group (container) (typed FeaturePython)
  n = 0.01088
FEATURE [App::DocumentObjectGroupPython] G4_GEL_PHOTO_EMULSION  # scripted group (container) (typed FeaturePython)
  Dunit = g/cm3
  Dvalue = 1.2914
  Group = -> [H_element041,C_element048,N_element018,O_element042,S_element013]
  conduct = 2
  density = 1
  expand = 3
  formula = G4_GEL_PHOTO_EMULSION
  name = G4_GEL_PHOTO_EMULSION
  specific = 4
FEATURE [App::DocumentObjectGroupPython] B_element004  label="B_element : 0.040"  # scripted group (container) (typed FeaturePython)
  n = 0.0400639
FEATURE [App::DocumentObjectGroupPython] O_element043  label="O_element : 0.540"  # scripted group (container) (typed FeaturePython)
  n = 0.539561
FEATURE [App::DocumentObjectGroupPython] Na_element008  label="Na_element : 0.028"  # scripted group (container) (typed FeaturePython)
  n = 0.0281909
FEATURE [App::DocumentObjectGroupPython] Al_element003  label="Al_element : 0.012"  # scripted group (container) (typed FeaturePython)
  n = 0.011644
FEATURE [App::DocumentObjectGroupPython] Si_element003  label="Si_element : 0.377"  # scripted group (container) (typed FeaturePython)
  n = 0.377219
FEATURE [App::DocumentObjectGroupPython] K_element004  label="K_element : 0.014"  # scripted group (container) (typed FeaturePython)
  n = 0.00332099
FEATURE [App::DocumentObjectGroupPython] G4_Pyrex_Glass  # scripted group (container) (typed FeaturePython)
  Dunit = g/cm3
  Dvalue = 2.23
  Group = -> [B_element004,O_element043,Na_element008,Al_element003,Si_element003,K_element004]
  conduct = 2
  density = 1
  expand = 3
  formula = G4_Pyrex_Glass
  name = G4_Pyrex_Glass
  specific = 4
FEATURE [App::DocumentObjectGroupPython] O_element044  label="O_element : 0.156"  # scripted group (container) (typed FeaturePython)
  n = 0.156453
FEATURE [App::DocumentObjectGroupPython] Si_element004  label="Si_element : 0.081"  # scripted group (container) (typed FeaturePython)
  n = 0.080866
FEATURE [App::DocumentObjectGroupPython] Ti_element001  label="Ti_element : 0.008"  # scripted group (container) (typed FeaturePython)
  n = 0.008092
FEATURE [App::DocumentObjectGroupPython] As_element002  label="As_element : 0.003"  # scripted group (container) (typed FeaturePython)
  n = 0.002651
FEATURE [App::DocumentObjectGroupPython] Pb_element001  label="Pb_element : 0.752"  # scripted group (container) (typed FeaturePython)
  n = 0.751938
FEATURE [App::DocumentObjectGroupPython] G4_GLASS_LEAD  # scripted group (container) (typed FeaturePython)
  Dunit = g/cm3
  Dvalue = 6.22
  Group = -> [O_element044,Si_element004,Ti_element001,As_element002,Pb_element001]
  conduct = 2
  density = 1
  expand = 3
  formula = G4_GLASS_LEAD
  name = G4_GLASS_LEAD
  specific = 4
FEATURE [App::DocumentObjectGroupPython] O_element045  label="O_element : 0.460"  # scripted group (container) (typed FeaturePython)
  n = 0.4598
FEATURE [App::DocumentObjectGroupPython] Na_element009  label="Na_element : 0.096"  # scripted group (container) (typed FeaturePython)
  n = 0.0964411
FEATURE [App::DocumentObjectGroupPython] Si_element005  label="Si_element : 0.378"  # scripted group (container) (typed FeaturePython)
  n = 0.336553
FEATURE [App::DocumentObjectGroupPython] Ca_element011  label="Ca_element : 0.107"  # scripted group (container) (typed FeaturePython)
  n = 0.107205
FEATURE [App::DocumentObjectGroupPython] G4_GLASS_PLATE  # scripted group (container) (typed FeaturePython)
  Dunit = g/cm3
  Dvalue = 2.4
  Group = -> [O_element045,Na_element009,Si_element005,Ca_element011]
  conduct = 2
  density = 1
  expand = 3
  formula = G4_GLASS_PLATE
  name = G4_GLASS_PLATE
  specific = 4
FEATURE [App::DocumentObjectGroupPython] C_element049  label="C_element : 026"  # scripted group (container) (typed FeaturePython)
  n = 5
  ref = C_element
FEATURE [App::DocumentObjectGroupPython] H_element042  label="H_element : 021"  # scripted group (container) (typed FeaturePython)
  n = 10
  ref = H_element
FEATURE [App::DocumentObjectGroupPython] N_element019  label="N_element : 2"  # scripted group (container) (typed FeaturePython)
  n = 2
  ref = N_element
FEATURE [App::DocumentObjectGroupPython] O_element046  label="O_element : 022"  # scripted group (container) (typed FeaturePython)
  n = 3
  ref = O_element
FEATURE [App::DocumentObjectGroupPython] G4_GLUTAMINE  # scripted group (container) (typed FeaturePython)
  Dunit = g/cm3
  Dvalue = 1.46
  Group = -> [C_element049,H_element042,N_element019,O_element046]
  conduct = 2
  density = 1
  expand = 3
  formula = G4_GLUTAMINE
  name = G4_GLUTAMINE
  specific = 4
FEATURE [App::DocumentObjectGroupPython] C_element050  label="C_element : 027"  # scripted group (container) (typed FeaturePython)
  n = 3
  ref = C_element
FEATURE [App::DocumentObjectGroupPython] H_element043  label="H_element : 022"  # scripted group (container) (typed FeaturePython)
  n = 8
  ref = H_element
FEATURE [App::DocumentObjectGroupPython] O_element047  label="O_element : 023"  # scripted group (container) (typed FeaturePython)
  n = 3
  ref = O_element
FEATURE [App::DocumentObjectGroupPython] G4_GLYCEROL  # scripted group (container) (typed FeaturePython)
  Dunit = g/cm3
  Dvalue = 1.2613
  Group = -> [C_element050,H_element043,O_element047]
  conduct = 2
  density = 1
  expand = 3
  formula = G4_GLYCEROL
  name = G4_GLYCEROL
  specific = 4
FEATURE [App::DocumentObjectGroupPython] C_element051  label="C_element : 028"  # scripted group (container) (typed FeaturePython)
  n = 5
  ref = C_element
FEATURE [App::DocumentObjectGroupPython] H_element044  label="H_element : 023"  # scripted group (container) (typed FeaturePython)
  n = 5
  ref = H_element
FEATURE [App::DocumentObjectGroupPython] N_element020  label="N_element : 009"  # scripted group (container) (typed FeaturePython)
  n = 5
  ref = N_element
FEATURE [App::DocumentObjectGroupPython] O_element048  label="O_element : 024"  # scripted group (container) (typed FeaturePython)
  n = 1
  ref = O_element
FEATURE [App::DocumentObjectGroupPython] G4_GUANINE  # scripted group (container) (typed FeaturePython)
  Dunit = g/cm3
  Dvalue = 2.2
  Group = -> [C_element051,H_element044,N_element020,O_element048]
  conduct = 2
  density = 1
  expand = 3
  formula = G4_GUANINE
  name = G4_GUANINE
  specific = 4
FEATURE [App::DocumentObjectGroupPython] Ca_element012  label="Ca_element : 006"  # scripted group (container) (typed FeaturePython)
  n = 1
  ref = Ca_element
FEATURE [App::DocumentObjectGroupPython] S_element014  label="S_element : 005"  # scripted group (container) (typed FeaturePython)
  n = 1
  ref = S_element
FEATURE [App::DocumentObjectGroupPython] O_element049  label="O_element : 6"  # scripted group (container) (typed FeaturePython)
  n = 6
  ref = O_element
FEATURE [App::DocumentObjectGroupPython] H_element045  label="H_element : 024"  # scripted group (container) (typed FeaturePython)
  n = 4
  ref = H_element
FEATURE [App::DocumentObjectGroupPython] G4_GYPSUM  # scripted group (container) (typed FeaturePython)
  Dunit = g/cm3
  Dvalue = 2.32
  Group = -> [Ca_element012,S_element014,O_element049,H_element045]
  conduct = 2
  density = 1
  expand = 3
  formula = G4_GYPSUM
  name = G4_GYPSUM
  specific = 4
FEATURE [App::DocumentObjectGroupPython] C_element052  label="C_element : 7"  # scripted group (container) (typed FeaturePython)
  n = 7
  ref = C_element
FEATURE [App::DocumentObjectGroupPython] H_element046  label="H_element : 16"  # scripted group (container) (typed FeaturePython)
  n = 16
  ref = H_element
FEATURE [App::DocumentObjectGroupPython] G4_N_HEPTANE  label="G4_N-HEPTANE"  # scripted group (container) (typed FeaturePython)
  Dunit = g/cm3
  Dvalue = 0.68376
  Group = -> [C_element052,H_element046]
  conduct = 2
  density = 1
  expand = 3
  formula = G4_N-HEPTANE
  name = G4_N-HEPTANE
  specific = 4
FEATURE [App::DocumentObjectGroupPython] C_element053  label="C_element : 029"  # scripted group (container) (typed FeaturePython)
  n = 6
  ref = C_element
FEATURE [App::DocumentObjectGroupPython] H_element047  label="H_element : 14"  # scripted group (container) (typed FeaturePython)
  n = 14
  ref = H_element
FEATURE [App::DocumentObjectGroupPython] G4_N_HEXANE  label="G4_N-HEXANE"  # scripted group (container) (typed FeaturePython)
  Dunit = g/cm3
  Dvalue = 0.6603
  Group = -> [C_element053,H_element047]
  conduct = 2
  density = 1
  expand = 3
  formula = G4_N-HEXANE
  name = G4_N-HEXANE
  specific = 4
FEATURE [App::DocumentObjectGroupPython] C_element054  label="C_element : 22"  # scripted group (container) (typed FeaturePython)
  n = 22
  ref = C_element
FEATURE [App::DocumentObjectGroupPython] H_element048  label="H_element : 025"  # scripted group (container) (typed FeaturePython)
  n = 10
  ref = H_element
FEATURE [App::DocumentObjectGroupPython] N_element021  label="N_element : 010"  # scripted group (container) (typed FeaturePython)
  n = 2
  ref = N_element
FEATURE [App::DocumentObjectGroupPython] O_element050  label="O_element : 025"  # scripted group (container) (typed FeaturePython)
  n = 5
  ref = O_element
FEATURE [App::DocumentObjectGroupPython] G4_KAPTON  # scripted group (container) (typed FeaturePython)
  Dunit = g/cm3
  Dvalue = 1.42
  Group = -> [C_element054,H_element048,N_element021,O_element050]
  conduct = 2
  density = 1
  expand = 3
  formula = G4_KAPTON
  name = G4_KAPTON
  specific = 4
FEATURE [App::DocumentObjectGroupPython] La_element001  label="La_element : 1"  # scripted group (container) (typed FeaturePython)
  n = 1
  ref = La_element
FEATURE [App::DocumentObjectGroupPython] Br_element003  label="Br_element : 002"  # scripted group (container) (typed FeaturePython)
  n = 1
  ref = Br_element
FEATURE [App::DocumentObjectGroupPython] O_element051  label="O_element : 026"  # scripted group (container) (typed FeaturePython)
  n = 1
  ref = O_element
FEATURE [App::DocumentObjectGroupPython] G4_LANTHANUM_OXYBROMIDE  # scripted group (container) (typed FeaturePython)
  Dunit = g/cm3
  Dvalue = 6.28
  Group = -> [La_element001,Br_element003,O_element051]
  conduct = 2
  density = 1
  expand = 3
  formula = G4_LANTHANUM_OXYBROMIDE
  name = G4_LANTHANUM_OXYBROMIDE
  specific = 4
FEATURE [App::DocumentObjectGroupPython] La_element002  label="La_element : 2"  # scripted group (container) (typed FeaturePython)
  n = 2
  ref = La_element
FEATURE [App::DocumentObjectGroupPython] O_element052  label="O_element : 027"  # scripted group (container) (typed FeaturePython)
  n = 2
  ref = O_element
FEATURE [App::DocumentObjectGroupPython] S_element015  label="S_element : 006"  # scripted group (container) (typed FeaturePython)
  n = 1
  ref = S_element
FEATURE [App::DocumentObjectGroupPython] G4_LANTHANUM_OXYSULFIDE  # scripted group (container) (typed FeaturePython)
  Dunit = g/cm3
  Dvalue = 5.86
  Group = -> [La_element002,O_element052,S_element015]
  conduct = 2
  density = 1
  expand = 3
  formula = G4_LANTHANUM_OXYSULFIDE
  name = G4_LANTHANUM_OXYSULFIDE
  specific = 4
FEATURE [App::DocumentObjectGroupPython] O_element053  label="O_element : 0.072"  # scripted group (container) (typed FeaturePython)
  n = 0.071682
FEATURE [App::DocumentObjectGroupPython] Pb_element002  label="Pb_element : 0.928"  # scripted group (container) (typed FeaturePython)
  n = 0.928318
FEATURE [App::DocumentObjectGroupPython] G4_LEAD_OXIDE  # scripted group (container) (typed FeaturePython)
  Dunit = g/cm3
  Dvalue = 9.53
  Group = -> [O_element053,Pb_element002]
  conduct = 2
  density = 1
  expand = 3
  formula = G4_LEAD_OXIDE
  name = G4_LEAD_OXIDE
  specific = 4
FEATURE [App::DocumentObjectGroupPython] Li_element001  label="Li_element : 1"  # scripted group (container) (typed FeaturePython)
  n = 1
  ref = Li_element
FEATURE [App::DocumentObjectGroupPython] N_element022  label="N_element : 011"  # scripted group (container) (typed FeaturePython)
  n = 1
  ref = N_element
FEATURE [App::DocumentObjectGroupPython] H_element049  label="H_element : 026"  # scripted group (container) (typed FeaturePython)
  n = 2
  ref = H_element
FEATURE [App::DocumentObjectGroupPython] G4_LITHIUM_AMIDE  # scripted group (container) (typed FeaturePython)
  Dunit = g/cm3
  Dvalue = 1.178
  Group = -> [Li_element001,N_element022,H_element049]
  conduct = 2
  density = 1
  expand = 3
  formula = G4_LITHIUM_AMIDE
  name = G4_LITHIUM_AMIDE
  specific = 4
FEATURE [App::DocumentObjectGroupPython] Li_element002  label="Li_element : 2"  # scripted group (container) (typed FeaturePython)
  n = 2
  ref = Li_element
FEATURE [App::DocumentObjectGroupPython] C_element055  label="C_element : 030"  # scripted group (container) (typed FeaturePython)
  n = 1
  ref = C_element
FEATURE [App::DocumentObjectGroupPython] O_element054  label="O_element : 028"  # scripted group (container) (typed FeaturePython)
  n = 3
  ref = O_element
FEATURE [App::DocumentObjectGroupPython] G4_LITHIUM_CARBONATE  # scripted group (container) (typed FeaturePython)
  Dunit = g/cm3
  Dvalue = 2.11
  Group = -> [Li_element002,C_element055,O_element054]
  conduct = 2
  density = 1
  expand = 3
  formula = G4_LITHIUM_CARBONATE
  name = G4_LITHIUM_CARBONATE
  specific = 4
FEATURE [App::DocumentObjectGroupPython] Li_element003  label="Li_element : 003"  # scripted group (container) (typed FeaturePython)
  n = 1
  ref = Li_element
FEATURE [App::DocumentObjectGroupPython] F_element012  label="F_element : 004"  # scripted group (container) (typed FeaturePython)
  n = 1
  ref = F_element
FEATURE [App::DocumentObjectGroupPython] G4_LITHIUM_FLUORIDE  # scripted group (container) (typed FeaturePython)
  Dunit = g/cm3
  Dvalue = 2.635
  Group = -> [Li_element003,F_element012]
  conduct = 2
  density = 1
  expand = 3
  formula = G4_LITHIUM_FLUORIDE
  name = G4_LITHIUM_FLUORIDE
  specific = 4
FEATURE [App::DocumentObjectGroupPython] Li_element004  label="Li_element : 004"  # scripted group (container) (typed FeaturePython)
  n = 1
  ref = Li_element
FEATURE [App::DocumentObjectGroupPython] H_element050  label="H_element : 027"  # scripted group (container) (typed FeaturePython)
  n = 1
  ref = H_element
FEATURE [App::DocumentObjectGroupPython] G4_LITHIUM_HYDRIDE  # scripted group (container) (typed FeaturePython)
  Dunit = g/cm3
  Dvalue = 0.82
  Group = -> [Li_element004,H_element050]
  conduct = 2
  density = 1
  expand = 3
  formula = G4_LITHIUM_HYDRIDE
  name = G4_LITHIUM_HYDRIDE
  specific = 4
FEATURE [App::DocumentObjectGroupPython] Li_element005  label="Li_element : 005"  # scripted group (container) (typed FeaturePython)
  n = 1
  ref = Li_element
FEATURE [App::DocumentObjectGroupPython] I_element003  label="I_element : 002"  # scripted group (container) (typed FeaturePython)
  n = 1
  ref = I_element
FEATURE [App::DocumentObjectGroupPython] G4_LITHIUM_IODIDE  # scripted group (container) (typed FeaturePython)
  Dunit = g/cm3
  Dvalue = 3.494
  Group = -> [Li_element005,I_element003]
  conduct = 2
  density = 1
  expand = 3
  formula = G4_LITHIUM_IODIDE
  name = G4_LITHIUM_IODIDE
  specific = 4
FEATURE [App::DocumentObjectGroupPython] Li_element006  label="Li_element : 006"  # scripted group (container) (typed FeaturePython)
  n = 2
  ref = Li_element
FEATURE [App::DocumentObjectGroupPython] O_element055  label="O_element : 029"  # scripted group (container) (typed FeaturePython)
  n = 1
  ref = O_element
FEATURE [App::DocumentObjectGroupPython] G4_LITHIUM_OXIDE  # scripted group (container) (typed FeaturePython)
  Dunit = g/cm3
  Dvalue = 2.013
  Group = -> [Li_element006,O_element055]
  conduct = 2
  density = 1
  expand = 3
  formula = G4_LITHIUM_OXIDE
  name = G4_LITHIUM_OXIDE
  specific = 4
FEATURE [App::DocumentObjectGroupPython] Li_element007  label="Li_element : 007"  # scripted group (container) (typed FeaturePython)
  n = 2
  ref = Li_element
FEATURE [App::DocumentObjectGroupPython] B_element005  label="B_element : 005"  # scripted group (container) (typed FeaturePython)
  n = 4
  ref = B_element
FEATURE [App::DocumentObjectGroupPython] O_element056  label="O_element : 7"  # scripted group (container) (typed FeaturePython)
  n = 7
  ref = O_element
FEATURE [App::DocumentObjectGroupPython] G4_LITHIUM_TETRABORATE  # scripted group (container) (typed FeaturePython)
  Dunit = g/cm3
  Dvalue = 2.44
  Group = -> [Li_element007,B_element005,O_element056]
  conduct = 2
  density = 1
  expand = 3
  formula = G4_LITHIUM_TETRABORATE
  name = G4_LITHIUM_TETRABORATE
  specific = 4
FEATURE [App::DocumentObjectGroupPython] H_element051  label="H_element : 0.105"  # scripted group (container) (typed FeaturePython)
  n = 0.105
FEATURE [App::DocumentObjectGroupPython] C_element056  label="C_element : 0.083"  # scripted group (container) (typed FeaturePython)
  n = 0.083
FEATURE [App::DocumentObjectGroupPython] N_element023  label="N_element : 0.023"  # scripted group (container) (typed FeaturePython)
  n = 0.023
FEATURE [App::DocumentObjectGroupPython] O_element057  label="O_element : 0.779"  # scripted group (container) (typed FeaturePython)
  n = 0.779
FEATURE [App::DocumentObjectGroupPython] Na_element010  label="Na_element : 0.097"  # scripted group (container) (typed FeaturePython)
  n = 0.002
FEATURE [App::DocumentObjectGroupPython] P_element006  label="P_element : 0.105"  # scripted group (container) (typed FeaturePython)
  n = 0.001
FEATURE [App::DocumentObjectGroupPython] S_element016  label="S_element : 0.017"  # scripted group (container) (typed FeaturePython)
  n = 0.002
FEATURE [App::DocumentObjectGroupPython] Cl_element014  label="Cl_element : 0.587"  # scripted group (container) (typed FeaturePython)
  n = 0.003
FEATURE [App::DocumentObjectGroupPython] K_element005  label="K_element : 0.015"  # scripted group (container) (typed FeaturePython)
  n = 0.002
FEATURE [App::DocumentObjectGroupPython] G4_LUNG_ICRP  # scripted group (container) (typed FeaturePython)
  Dunit = g/cm3
  Dvalue = 1.04
  Group = -> [H_element051,C_element056,N_element023,O_element057,Na_element010,P_element006,S_element016,Cl_element014,K_element005]
  conduct = 2
  density = 1
  expand = 3
  formula = G4_LUNG_ICRP
  name = G4_LUNG_ICRP
  specific = 4
FEATURE [App::DocumentObjectGroupPython] H_element052  label="H_element : 0.116"  # scripted group (container) (typed FeaturePython)
  n = 0.114318
FEATURE [App::DocumentObjectGroupPython] C_element057  label="C_element : 0.656"  # scripted group (container) (typed FeaturePython)
  n = 0.655824
FEATURE [App::DocumentObjectGroupPython] O_element058  label="O_element : 0.092"  # scripted group (container) (typed FeaturePython)
  n = 0.0921831
FEATURE [App::DocumentObjectGroupPython] Mg_element004  label="Mg_element : 0.135"  # scripted group (container) (typed FeaturePython)
  n = 0.134792
FEATURE [App::DocumentObjectGroupPython] Ca_element013  label="Ca_element : 0.003"  # scripted group (container) (typed FeaturePython)
  n = 0.002883
FEATURE [App::DocumentObjectGroupPython] G4_M3_WAX  # scripted group (container) (typed FeaturePython)
  Dunit = g/cm3
  Dvalue = 1.05
  Group = -> [H_element052,C_element057,O_element058,Mg_element004,Ca_element013]
  conduct = 2
  density = 1
  expand = 3
  formula = G4_M3_WAX
  name = G4_M3_WAX
  specific = 4
FEATURE [App::DocumentObjectGroupPython] Mg_element005  label="Mg_element : 1"  # scripted group (container) (typed FeaturePython)
  n = 1
  ref = Mg_element
FEATURE [App::DocumentObjectGroupPython] C_element058  label="C_element : 031"  # scripted group (container) (typed FeaturePython)
  n = 1
  ref = C_element
FEATURE [App::DocumentObjectGroupPython] O_element059  label="O_element : 030"  # scripted group (container) (typed FeaturePython)
  n = 3
  ref = O_element
FEATURE [App::DocumentObjectGroupPython] G4_MAGNESIUM_CARBONATE  # scripted group (container) (typed FeaturePython)
  Dunit = g/cm3
  Dvalue = 2.958
  Group = -> [Mg_element005,C_element058,O_element059]
  conduct = 2
  density = 1
  expand = 3
  formula = G4_MAGNESIUM_CARBONATE
  name = G4_MAGNESIUM_CARBONATE
  specific = 4
FEATURE [App::DocumentObjectGroupPython] Mg_element006  label="Mg_element : 002"  # scripted group (container) (typed FeaturePython)
  n = 1
  ref = Mg_element
FEATURE [App::DocumentObjectGroupPython] F_element013  label="F_element : 005"  # scripted group (container) (typed FeaturePython)
  n = 2
  ref = F_element
FEATURE [App::DocumentObjectGroupPython] G4_MAGNESIUM_FLUORIDE  # scripted group (container) (typed FeaturePython)
  Dunit = g/cm3
  Dvalue = 3
  Group = -> [Mg_element006,F_element013]
  conduct = 2
  density = 1
  expand = 3
  formula = G4_MAGNESIUM_FLUORIDE
  name = G4_MAGNESIUM_FLUORIDE
  specific = 4
FEATURE [App::DocumentObjectGroupPython] Mg_element007  label="Mg_element : 003"  # scripted group (container) (typed FeaturePython)
  n = 1
  ref = Mg_element
FEATURE [App::DocumentObjectGroupPython] O_element060  label="O_element : 031"  # scripted group (container) (typed FeaturePython)
  n = 1
  ref = O_element
FEATURE [App::DocumentObjectGroupPython] G4_MAGNESIUM_OXIDE  # scripted group (container) (typed FeaturePython)
  Dunit = g/cm3
  Dvalue = 3.58
  Group = -> [Mg_element007,O_element060]
  conduct = 2
  density = 1
  expand = 3
  formula = G4_MAGNESIUM_OXIDE
  name = G4_MAGNESIUM_OXIDE
  specific = 4
FEATURE [App::DocumentObjectGroupPython] Mg_element008  label="Mg_element : 004"  # scripted group (container) (typed FeaturePython)
  n = 1
  ref = Mg_element
FEATURE [App::DocumentObjectGroupPython] B_element006  label="B_element : 006"  # scripted group (container) (typed FeaturePython)
  n = 4
  ref = B_element
FEATURE [App::DocumentObjectGroupPython] O_element061  label="O_element : 032"  # scripted group (container) (typed FeaturePython)
  n = 7
  ref = O_element
FEATURE [App::DocumentObjectGroupPython] G4_MAGNESIUM_TETRABORATE  # scripted group (container) (typed FeaturePython)
  Dunit = g/cm3
  Dvalue = 2.53
  Group = -> [Mg_element008,B_element006,O_element061]
  conduct = 2
  density = 1
  expand = 3
  formula = G4_MAGNESIUM_TETRABORATE
  name = G4_MAGNESIUM_TETRABORATE
  specific = 4
FEATURE [App::DocumentObjectGroupPython] Hg_element001  label="Hg_element : 1"  # scripted group (container) (typed FeaturePython)
  n = 1
  ref = Hg_element
FEATURE [App::DocumentObjectGroupPython] I_element004  label="I_element : 2"  # scripted group (container) (typed FeaturePython)
  n = 2
  ref = I_element
FEATURE [App::DocumentObjectGroupPython] G4_MERCURIC_IODIDE  # scripted group (container) (typed FeaturePython)
  Dunit = g/cm3
  Dvalue = 6.36
  Group = -> [Hg_element001,I_element004]
  conduct = 2
  density = 1
  expand = 3
  formula = G4_MERCURIC_IODIDE
  name = G4_MERCURIC_IODIDE
  specific = 4
FEATURE [App::DocumentObjectGroupPython] C_element059  label="C_element : 032"  # scripted group (container) (typed FeaturePython)
  n = 1
  ref = C_element
FEATURE [App::DocumentObjectGroupPython] H_element053  label="H_element : 028"  # scripted group (container) (typed FeaturePython)
  n = 4
  ref = H_element
FEATURE [App::DocumentObjectGroupPython] G4_METHANE  # scripted group (container) (typed FeaturePython)
  Dunit = g/cm3
  Dvalue = 0.000667151
  Group = -> [C_element059,H_element053]
  conduct = 2
  density = 1
  expand = 3
  formula = G4_METHANE
  name = G4_METHANE
  specific = 4
FEATURE [App::DocumentObjectGroupPython] C_element060  label="C_element : 033"  # scripted group (container) (typed FeaturePython)
  n = 1
  ref = C_element
FEATURE [App::DocumentObjectGroupPython] H_element054  label="H_element : 029"  # scripted group (container) (typed FeaturePython)
  n = 4
  ref = H_element
FEATURE [App::DocumentObjectGroupPython] O_element062  label="O_element : 033"  # scripted group (container) (typed FeaturePython)
  n = 1
  ref = O_element
FEATURE [App::DocumentObjectGroupPython] G4_METHANOL  # scripted group (container) (typed FeaturePython)
  Dunit = g/cm3
  Dvalue = 0.7914
  Group = -> [C_element060,H_element054,O_element062]
  conduct = 2
  density = 1
  expand = 3
  formula = G4_METHANOL
  name = G4_METHANOL
  specific = 4
FEATURE [App::DocumentObjectGroupPython] H_element055  label="H_element : 0.134"  # scripted group (container) (typed FeaturePython)
  n = 0.13404
FEATURE [App::DocumentObjectGroupPython] C_element061  label="C_element : 0.778"  # scripted group (container) (typed FeaturePython)
  n = 0.77796
FEATURE [App::DocumentObjectGroupPython] O_element063  label="O_element : 0.035"  # scripted group (container) (typed FeaturePython)
  n = 0.03502
FEATURE [App::DocumentObjectGroupPython] Mg_element009  label="Mg_element : 0.039"  # scripted group (container) (typed FeaturePython)
  n = 0.038594
FEATURE [App::DocumentObjectGroupPython] Ti_element002  label="Ti_element : 0.014"  # scripted group (container) (typed FeaturePython)
  n = 0.014386
FEATURE [App::DocumentObjectGroupPython] G4_MIX_D_WAX  # scripted group (container) (typed FeaturePython)
  Dunit = g/cm3
  Dvalue = 0.99
  Group = -> [H_element055,C_element061,O_element063,Mg_element009,Ti_element002]
  conduct = 2
  density = 1
  expand = 3
  formula = G4_MIX_D_WAX
  name = G4_MIX_D_WAX
  specific = 4
FEATURE [App::DocumentObjectGroupPython] H_element056  label="H_element : 0.135"  # scripted group (container) (typed FeaturePython)
  n = 0.081192
FEATURE [App::DocumentObjectGroupPython] C_element062  label="C_element : 0.583"  # scripted group (container) (typed FeaturePython)
  n = 0.583442
FEATURE [App::DocumentObjectGroupPython] N_element024  label="N_element : 0.018"  # scripted group (container) (typed FeaturePython)
  n = 0.017798
FEATURE [App::DocumentObjectGroupPython] O_element064  label="O_element : 0.186"  # scripted group (container) (typed FeaturePython)
  n = 0.186381
FEATURE [App::DocumentObjectGroupPython] Mg_element010  label="Mg_element : 0.130"  # scripted group (container) (typed FeaturePython)
  n = 0.130287
FEATURE [App::DocumentObjectGroupPython] Cl_element015  label="Cl_element : 0.588"  # scripted group (container) (typed FeaturePython)
  n = 0.0009
FEATURE [App::DocumentObjectGroupPython] G4_MS20_TISSUE  # scripted group (container) (typed FeaturePython)
  Dunit = g/cm3
  Dvalue = 1
  Group = -> [H_element056,C_element062,N_element024,O_element064,Mg_element010,Cl_element015]
  conduct = 2
  density = 1
  expand = 3
  formula = G4_MS20_TISSUE
  name = G4_MS20_TISSUE
  specific = 4
FEATURE [App::DocumentObjectGroupPython] H_element057  label="H_element : 0.136"  # scripted group (container) (typed FeaturePython)
  n = 0.102
FEATURE [App::DocumentObjectGroupPython] C_element063  label="C_element : 0.143"  # scripted group (container) (typed FeaturePython)
  n = 0.143
FEATURE [App::DocumentObjectGroupPython] N_element025  label="N_element : 0.034"  # scripted group (container) (typed FeaturePython)
  n = 0.034
FEATURE [App::DocumentObjectGroupPython] O_element065  label="O_element : 0.710"  # scripted group (container) (typed FeaturePython)
  n = 0.71
FEATURE [App::DocumentObjectGroupPython] Na_element011  label="Na_element : 0.098"  # scripted group (container) (typed FeaturePython)
  n = 0.001
FEATURE [App::DocumentObjectGroupPython] P_element007  label="P_element : 0.002"  # scripted group (container) (typed FeaturePython)
  n = 0.002
FEATURE [App::DocumentObjectGroupPython] S_element017  label="S_element : 0.018"  # scripted group (container) (typed FeaturePython)
  n = 0.003
FEATURE [App::DocumentObjectGroupPython] Cl_element016  label="Cl_element : 0.589"  # scripted group (container) (typed FeaturePython)
  n = 0.001
FEATURE [App::DocumentObjectGroupPython] K_element006  label="K_element : 0.004"  # scripted group (container) (typed FeaturePython)
  n = 0.004
FEATURE [App::DocumentObjectGroupPython] G4_MUSCLE_SKELETAL_ICRP  # scripted group (container) (typed FeaturePython)
  Dunit = g/cm3
  Dvalue = 1.05
  Group = -> [H_element057,C_element063,N_element025,O_element065,Na_element011,P_element007,S_element017,Cl_element016,K_element006]
  conduct = 2
  density = 1
  expand = 3
  formula = G4_MUSCLE_SKELETAL_ICRP
  name = G4_MUSCLE_SKELETAL_ICRP
  specific = 4
FEATURE [App::DocumentObjectGroupPython] H_element058  label="H_element : 0.137"  # scripted group (container) (typed FeaturePython)
  n = 0.102102
FEATURE [App::DocumentObjectGroupPython] C_element064  label="C_element : 0.123"  # scripted group (container) (typed FeaturePython)
  n = 0.123123
FEATURE [App::DocumentObjectGroupPython] N_element026  label="N_element : 0.756"  # scripted group (container) (typed FeaturePython)
  n = 0.035035
FEATURE [App::DocumentObjectGroupPython] O_element066  label="O_element : 0.730"  # scripted group (container) (typed FeaturePython)
  n = 0.72973
FEATURE [App::DocumentObjectGroupPython] Na_element012  label="Na_element : 0.099"  # scripted group (container) (typed FeaturePython)
  n = 0.001001
FEATURE [App::DocumentObjectGroupPython] P_element008  label="P_element : 0.106"  # scripted group (container) (typed FeaturePython)
  n = 0.002002
FEATURE [App::DocumentObjectGroupPython] S_element018  label="S_element : 0.019"  # scripted group (container) (typed FeaturePython)
  n = 0.004004
FEATURE [App::DocumentObjectGroupPython] K_element007  label="K_element : 0.016"  # scripted group (container) (typed FeaturePython)
  n = 0.003003
FEATURE [App::DocumentObjectGroupPython] G4_MUSCLE_STRIATED_ICRU  # scripted group (container) (typed FeaturePython)
  Dunit = g/cm3
  Dvalue = 1.04
  Group = -> [H_element058,C_element064,N_element026,O_element066,Na_element012,P_element008,S_element018,K_element007]
  conduct = 2
  density = 1
  expand = 3
  formula = G4_MUSCLE_STRIATED_ICRU
  name = G4_MUSCLE_STRIATED_ICRU
  specific = 4
FEATURE [App::DocumentObjectGroupPython] H_element059  label="H_element : 0.098"  # scripted group (container) (typed FeaturePython)
  n = 0.0982341
FEATURE [App::DocumentObjectGroupPython] C_element065  label="C_element : 0.156"  # scripted group (container) (typed FeaturePython)
  n = 0.156214
FEATURE [App::DocumentObjectGroupPython] N_element027  label="N_element : 0.757"  # scripted group (container) (typed FeaturePython)
  n = 0.035451
FEATURE [App::DocumentObjectGroupPython] O_element067  label="O_element : 0.880"  # scripted group (container) (typed FeaturePython)
  n = 0.710101
FEATURE [App::DocumentObjectGroupPython] G4_MUSCLE_WITH_SUCROSE  # scripted group (container) (typed FeaturePython)
  Dunit = g/cm3
  Dvalue = 1.11
  Group = -> [H_element059,C_element065,N_element027,O_element067]
  conduct = 2
  density = 1
  expand = 3
  formula = G4_MUSCLE_WITH_SUCROSE
  name = G4_MUSCLE_WITH_SUCROSE
  specific = 4
FEATURE [App::DocumentObjectGroupPython] H_element060  label="H_element : 0.138"  # scripted group (container) (typed FeaturePython)
  n = 0.101969
FEATURE [App::DocumentObjectGroupPython] C_element066  label="C_element : 0.120"  # scripted group (container) (typed FeaturePython)
  n = 0.120058
FEATURE [App::DocumentObjectGroupPython] N_element028  label="N_element : 0.758"  # scripted group (container) (typed FeaturePython)
  n = 0.035451
FEATURE [App::DocumentObjectGroupPython] O_element068  label="O_element : 0.743"  # scripted group (container) (typed FeaturePython)
  n = 0.742522
FEATURE [App::DocumentObjectGroupPython] G4_MUSCLE_WITHOUT_SUCROSE  # scripted group (container) (typed FeaturePython)
  Dunit = g/cm3
  Dvalue = 1.07
  Group = -> [H_element060,C_element066,N_element028,O_element068]
  conduct = 2
  density = 1
  expand = 3
  formula = G4_MUSCLE_WITHOUT_SUCROSE
  name = G4_MUSCLE_WITHOUT_SUCROSE
  specific = 4
FEATURE [App::DocumentObjectGroupPython] C_element067  label="C_element : 10"  # scripted group (container) (typed FeaturePython)
  n = 10
  ref = C_element
FEATURE [App::DocumentObjectGroupPython] H_element061  label="H_element : 030"  # scripted group (container) (typed FeaturePython)
  n = 8
  ref = H_element
FEATURE [App::DocumentObjectGroupPython] G4_NAPHTHALENE  # scripted group (container) (typed FeaturePython)
  Dunit = g/cm3
  Dvalue = 1.145
  Group = -> [C_element067,H_element061]
  conduct = 2
  density = 1
  expand = 3
  formula = G4_NAPHTHALENE
  name = G4_NAPHTHALENE
  specific = 4
FEATURE [App::DocumentObjectGroupPython] C_element068  label="C_element : 034"  # scripted group (container) (typed FeaturePython)
  n = 6
  ref = C_element
FEATURE [App::DocumentObjectGroupPython] H_element062  label="H_element : 031"  # scripted group (container) (typed FeaturePython)
  n = 5
  ref = H_element
FEATURE [App::DocumentObjectGroupPython] N_element029  label="N_element : 012"  # scripted group (container) (typed FeaturePython)
  n = 1
  ref = N_element
FEATURE [App::DocumentObjectGroupPython] O_element069  label="O_element : 034"  # scripted group (container) (typed FeaturePython)
  n = 2
  ref = O_element
FEATURE [App::DocumentObjectGroupPython] G4_NITROBENZENE  # scripted group (container) (typed FeaturePython)
  Dunit = g/cm3
  Dvalue = 1.19867
  Group = -> [C_element068,H_element062,N_element029,O_element069]
  conduct = 2
  density = 1
  expand = 3
  formula = G4_NITROBENZENE
  name = G4_NITROBENZENE
  specific = 4
FEATURE [App::DocumentObjectGroupPython] N_element030  label="N_element : 013"  # scripted group (container) (typed FeaturePython)
  n = 2
  ref = N_element
FEATURE [App::DocumentObjectGroupPython] O_element070  label="O_element : 035"  # scripted group (container) (typed FeaturePython)
  n = 1
  ref = O_element
FEATURE [App::DocumentObjectGroupPython] G4_NITROUS_OXIDE  # scripted group (container) (typed FeaturePython)
  Dunit = g/cm3
  Dvalue = 0.00183094
  Group = -> [N_element030,O_element070]
  conduct = 2
  density = 1
  expand = 3
  formula = G4_NITROUS_OXIDE
  name = G4_NITROUS_OXIDE
  specific = 4
FEATURE [App::DocumentObjectGroupPython] H_element063  label="H_element : 0.104"  # scripted group (container) (typed FeaturePython)
  n = 0.103509
FEATURE [App::DocumentObjectGroupPython] C_element069  label="C_element : 0.648"  # scripted group (container) (typed FeaturePython)
  n = 0.648416
FEATURE [App::DocumentObjectGroupPython] N_element031  label="N_element : 0.100"  # scripted group (container) (typed FeaturePython)
  n = 0.0995361
FEATURE [App::DocumentObjectGroupPython] O_element071  label="O_element : 0.149"  # scripted group (container) (typed FeaturePython)
  n = 0.148539
FEATURE [App::DocumentObjectGroupPython] G4_NYLON_8062  label="G4_NYLON-8062"  # scripted group (container) (typed FeaturePython)
  Dunit = g/cm3
  Dvalue = 1.08
  Group = -> [H_element063,C_element069,N_element031,O_element071]
  conduct = 2
  density = 1
  expand = 3
  formula = G4_NYLON-8062
  name = G4_NYLON-8062
  specific = 4
FEATURE [App::DocumentObjectGroupPython] C_element070  label="C_element : 035"  # scripted group (container) (typed FeaturePython)
  n = 6
  ref = C_element
FEATURE [App::DocumentObjectGroupPython] H_element064  label="H_element : 11"  # scripted group (container) (typed FeaturePython)
  n = 11
  ref = H_element
FEATURE [App::DocumentObjectGroupPython] N_element032  label="N_element : 014"  # scripted group (container) (typed FeaturePython)
  n = 1
  ref = N_element
FEATURE [App::DocumentObjectGroupPython] O_element072  label="O_element : 036"  # scripted group (container) (typed FeaturePython)
  n = 1
  ref = O_element
FEATURE [App::DocumentObjectGroupPython] G4_NYLON_6_6  label="G4_NYLON-6-6"  # scripted group (container) (typed FeaturePython)
  Dunit = g/cm3
  Dvalue = 1.14
  Group = -> [C_element070,H_element064,N_element032,O_element072]
  conduct = 2
  density = 1
  expand = 3
  formula = G4_NYLON-6-6
  name = G4_NYLON-6-6
  specific = 4
FEATURE [App::DocumentObjectGroupPython] H_element065  label="H_element : 0.139"  # scripted group (container) (typed FeaturePython)
  n = 0.107062
FEATURE [App::DocumentObjectGroupPython] C_element071  label="C_element : 0.680"  # scripted group (container) (typed FeaturePython)
  n = 0.680449
FEATURE [App::DocumentObjectGroupPython] N_element033  label="N_element : 0.099"  # scripted group (container) (typed FeaturePython)
  n = 0.099189
FEATURE [App::DocumentObjectGroupPython] O_element073  label="O_element : 0.113"  # scripted group (container) (typed FeaturePython)
  n = 0.1133
FEATURE [App::DocumentObjectGroupPython] G4_NYLON_6_10  label="G4_NYLON-6-10"  # scripted group (container) (typed FeaturePython)
  Dunit = g/cm3
  Dvalue = 1.14
  Group = -> [H_element065,C_element071,N_element033,O_element073]
  conduct = 2
  density = 1
  expand = 3
  formula = G4_NYLON-6-10
  name = G4_NYLON-6-10
  specific = 4
FEATURE [App::DocumentObjectGroupPython] H_element066  label="H_element : 0.140"  # scripted group (container) (typed FeaturePython)
  n = 0.115476
FEATURE [App::DocumentObjectGroupPython] C_element072  label="C_element : 0.721"  # scripted group (container) (typed FeaturePython)
  n = 0.720818
FEATURE [App::DocumentObjectGroupPython] N_element034  label="N_element : 0.076"  # scripted group (container) (typed FeaturePython)
  n = 0.0764169
FEATURE [App::DocumentObjectGroupPython] O_element074  label="O_element : 0.087"  # scripted group (container) (typed FeaturePython)
  n = 0.0872889
FEATURE [App::DocumentObjectGroupPython] G4_NYLON_11_RILSAN  label="G4_NYLON-11_RILSAN"  # scripted group (container) (typed FeaturePython)
  Dunit = g/cm3
  Dvalue = 1.425
  Group = -> [H_element066,C_element072,N_element034,O_element074]
  conduct = 2
  density = 1
  expand = 3
  formula = G4_NYLON-11_RILSAN
  name = G4_NYLON-11_RILSAN
  specific = 4
FEATURE [App::DocumentObjectGroupPython] C_element073  label="C_element : 8"  # scripted group (container) (typed FeaturePython)
  n = 8
  ref = C_element
FEATURE [App::DocumentObjectGroupPython] H_element067  label="H_element : 18"  # scripted group (container) (typed FeaturePython)
  n = 18
  ref = H_element
FEATURE [App::DocumentObjectGroupPython] G4_OCTANE  # scripted group (container) (typed FeaturePython)
  Dunit = g/cm3
  Dvalue = 0.7026
  Group = -> [C_element073,H_element067]
  conduct = 2
  density = 1
  expand = 3
  formula = G4_OCTANE
  name = G4_OCTANE
  specific = 4
FEATURE [App::DocumentObjectGroupPython] C_element074  label="C_element : 25"  # scripted group (container) (typed FeaturePython)
  n = 25
  ref = C_element
FEATURE [App::DocumentObjectGroupPython] H_element068  label="H_element : 52"  # scripted group (container) (typed FeaturePython)
  n = 52
  ref = H_element
FEATURE [App::DocumentObjectGroupPython] G4_PARAFFIN  # scripted group (container) (typed FeaturePython)
  Dunit = g/cm3
  Dvalue = 0.93
  Group = -> [C_element074,H_element068]
  conduct = 2
  density = 1
  expand = 3
  formula = G4_PARAFFIN
  name = G4_PARAFFIN
  specific = 4
FEATURE [App::DocumentObjectGroupPython] C_element075  label="C_element : 036"  # scripted group (container) (typed FeaturePython)
  n = 5
  ref = C_element
FEATURE [App::DocumentObjectGroupPython] H_element069  label="H_element : 032"  # scripted group (container) (typed FeaturePython)
  n = 12
  ref = H_element
FEATURE [App::DocumentObjectGroupPython] G4_N_PENTANE  label="G4_N-PENTANE"  # scripted group (container) (typed FeaturePython)
  Dunit = g/cm3
  Dvalue = 0.6262
  Group = -> [C_element075,H_element069]
  conduct = 2
  density = 1
  expand = 3
  formula = G4_N-PENTANE
  name = G4_N-PENTANE
  specific = 4
FEATURE [App::DocumentObjectGroupPython] H_element070  label="H_element : 0.014"  # scripted group (container) (typed FeaturePython)
  n = 0.0141
FEATURE [App::DocumentObjectGroupPython] C_element076  label="C_element : 0.072"  # scripted group (container) (typed FeaturePython)
  n = 0.072261
FEATURE [App::DocumentObjectGroupPython] N_element035  label="N_element : 0.019"  # scripted group (container) (typed FeaturePython)
  n = 0.01932
FEATURE [App::DocumentObjectGroupPython] O_element075  label="O_element : 0.066"  # scripted group (container) (typed FeaturePython)
  n = 0.066101
FEATURE [App::DocumentObjectGroupPython] S_element019  label="S_element : 0.020"  # scripted group (container) (typed FeaturePython)
  n = 0.00189
FEATURE [App::DocumentObjectGroupPython] Br_element004  label="Br_element : 0.349"  # scripted group (container) (typed FeaturePython)
  n = 0.349103
FEATURE [App::DocumentObjectGroupPython] Ag_element001  label="Ag_element : 0.474"  # scripted group (container) (typed FeaturePython)
  n = 0.474105
FEATURE [App::DocumentObjectGroupPython] I_element005  label="I_element : 0.003"  # scripted group (container) (typed FeaturePython)
  n = 0.00312
FEATURE [App::DocumentObjectGroupPython] G4_PHOTO_EMULSION  # scripted group (container) (typed FeaturePython)
  Dunit = g/cm3
  Dvalue = 3.815
  Group = -> [H_element070,C_element076,N_element035,O_element075,S_element019,Br_element004,Ag_element001,I_element005]
  conduct = 2
  density = 1
  expand = 3
  formula = G4_PHOTO_EMULSION
  name = G4_PHOTO_EMULSION
  specific = 4
FEATURE [App::DocumentObjectGroupPython] C_element077  label="C_element : 9"  # scripted group (container) (typed FeaturePython)
  n = 9
  ref = C_element
FEATURE [App::DocumentObjectGroupPython] H_element071  label="H_element : 033"  # scripted group (container) (typed FeaturePython)
  n = 10
  ref = H_element
FEATURE [App::DocumentObjectGroupPython] G4_PLASTIC_SC_VINYLTOLUENE  # scripted group (container) (typed FeaturePython)
  Dunit = g/cm3
  Dvalue = 1.032
  Group = -> [C_element077,H_element071]
  conduct = 2
  density = 1
  expand = 3
  formula = G4_PLASTIC_SC_VINYLTOLUENE
  name = G4_PLASTIC_SC_VINYLTOLUENE
  specific = 4
FEATURE [App::DocumentObjectGroupPython] Pu_element001  label="Pu_element : 1"  # scripted group (container) (typed FeaturePython)
  n = 1
  ref = Pu_element
FEATURE [App::DocumentObjectGroupPython] O_element076  label="O_element : 037"  # scripted group (container) (typed FeaturePython)
  n = 2
  ref = O_element
FEATURE [App::DocumentObjectGroupPython] G4_PLUTONIUM_DIOXIDE  # scripted group (container) (typed FeaturePython)
  Dunit = g/cm3
  Dvalue = 11.46
  Group = -> [Pu_element001,O_element076]
  conduct = 2
  density = 1
  expand = 3
  formula = G4_PLUTONIUM_DIOXIDE
  name = G4_PLUTONIUM_DIOXIDE
  specific = 4
FEATURE [App::DocumentObjectGroupPython] C_element078  label="C_element : 037"  # scripted group (container) (typed FeaturePython)
  n = 3
  ref = C_element
FEATURE [App::DocumentObjectGroupPython] H_element072  label="H_element : 034"  # scripted group (container) (typed FeaturePython)
  n = 3
  ref = H_element
FEATURE [App::DocumentObjectGroupPython] N_element036  label="N_element : 015"  # scripted group (container) (typed FeaturePython)
  n = 1
  ref = N_element
FEATURE [App::DocumentObjectGroupPython] G4_POLYACRYLONITRILE  # scripted group (container) (typed FeaturePython)
  Dunit = g/cm3
  Dvalue = 1.17
  Group = -> [C_element078,H_element072,N_element036]
  conduct = 2
  density = 1
  expand = 3
  formula = G4_POLYACRYLONITRILE
  name = G4_POLYACRYLONITRILE
  specific = 4
FEATURE [App::DocumentObjectGroupPython] C_element079  label="C_element : 16"  # scripted group (container) (typed FeaturePython)
  n = 16
  ref = C_element
FEATURE [App::DocumentObjectGroupPython] H_element073  label="H_element : 035"  # scripted group (container) (typed FeaturePython)
  n = 14
  ref = H_element
FEATURE [App::DocumentObjectGroupPython] O_element077  label="O_element : 038"  # scripted group (container) (typed FeaturePython)
  n = 3
  ref = O_element
FEATURE [App::DocumentObjectGroupPython] G4_POLYCARBONATE  # scripted group (container) (typed FeaturePython)
  Dunit = g/cm3
  Dvalue = 1.2
  Group = -> [C_element079,H_element073,O_element077]
  conduct = 2
  density = 1
  expand = 3
  formula = G4_POLYCARBONATE
  name = G4_POLYCARBONATE
  specific = 4
FEATURE [App::DocumentObjectGroupPython] C_element080  label="C_element : 038"  # scripted group (container) (typed FeaturePython)
  n = 8
  ref = C_element
FEATURE [App::DocumentObjectGroupPython] H_element074  label="H_element : 036"  # scripted group (container) (typed FeaturePython)
  n = 7
  ref = H_element
FEATURE [App::DocumentObjectGroupPython] Cl_element017  label="Cl_element : 007"  # scripted group (container) (typed FeaturePython)
  n = 1
  ref = Cl_element
FEATURE [App::DocumentObjectGroupPython] G4_POLYCHLOROSTYRENE  # scripted group (container) (typed FeaturePython)
  Dunit = g/cm3
  Dvalue = 1.3
  Group = -> [C_element080,H_element074,Cl_element017]
  conduct = 2
  density = 1
  expand = 3
  formula = G4_POLYCHLOROSTYRENE
  name = G4_POLYCHLOROSTYRENE
  specific = 4
FEATURE [App::DocumentObjectGroupPython] C_element081  label="C_element : 039"  # scripted group (container) (typed FeaturePython)
  n = 1
  ref = C_element
FEATURE [App::DocumentObjectGroupPython] H_element075  label="H_element : 037"  # scripted group (container) (typed FeaturePython)
  n = 2
  ref = H_element
FEATURE [App::DocumentObjectGroupPython] G4_POLYETHYLENE  # scripted group (container) (typed FeaturePython)
  Dunit = g/cm3
  Dvalue = 0.94
  Group = -> [C_element081,H_element075]
  conduct = 2
  density = 1
  expand = 3
  formula = G4_POLYETHYLENE
  name = G4_POLYETHYLENE
  specific = 4
FEATURE [App::DocumentObjectGroupPython] C_element082  label="C_element : 040"  # scripted group (container) (typed FeaturePython)
  n = 10
  ref = C_element
FEATURE [App::DocumentObjectGroupPython] H_element076  label="H_element : 038"  # scripted group (container) (typed FeaturePython)
  n = 8
  ref = H_element
FEATURE [App::DocumentObjectGroupPython] O_element078  label="O_element : 039"  # scripted group (container) (typed FeaturePython)
  n = 4
  ref = O_element
FEATURE [App::DocumentObjectGroupPython] G4_MYLAR  # scripted group (container) (typed FeaturePython)
  Dunit = g/cm3
  Dvalue = 1.4
  Group = -> [C_element082,H_element076,O_element078]
  conduct = 2
  density = 1
  expand = 3
  formula = G4_MYLAR
  name = G4_MYLAR
  specific = 4
FEATURE [App::DocumentObjectGroupPython] C_element083  label="C_element : 041"  # scripted group (container) (typed FeaturePython)
  n = 5
  ref = C_element
FEATURE [App::DocumentObjectGroupPython] H_element077  label="H_element : 039"  # scripted group (container) (typed FeaturePython)
  n = 8
  ref = H_element
FEATURE [App::DocumentObjectGroupPython] O_element079  label="O_element : 040"  # scripted group (container) (typed FeaturePython)
  n = 2
  ref = O_element
FEATURE [App::DocumentObjectGroupPython] G4_PLEXIGLASS  # scripted group (container) (typed FeaturePython)
  Dunit = g/cm3
  Dvalue = 1.19
  Group = -> [C_element083,H_element077,O_element079]
  conduct = 2
  density = 1
  expand = 3
  formula = G4_PLEXIGLASS
  name = G4_PLEXIGLASS
  specific = 4
FEATURE [App::DocumentObjectGroupPython] C_element084  label="C_element : 042"  # scripted group (container) (typed FeaturePython)
  n = 1
  ref = C_element
FEATURE [App::DocumentObjectGroupPython] H_element078  label="H_element : 040"  # scripted group (container) (typed FeaturePython)
  n = 2
  ref = H_element
FEATURE [App::DocumentObjectGroupPython] O_element080  label="O_element : 041"  # scripted group (container) (typed FeaturePython)
  n = 1
  ref = O_element
FEATURE [App::DocumentObjectGroupPython] G4_POLYOXYMETHYLENE  # scripted group (container) (typed FeaturePython)
  Dunit = g/cm3
  Dvalue = 1.425
  Group = -> [C_element084,H_element078,O_element080]
  conduct = 2
  density = 1
  expand = 3
  formula = G4_POLYOXYMETHYLENE
  name = G4_POLYOXYMETHYLENE
  specific = 4
FEATURE [App::DocumentObjectGroupPython] C_element085  label="C_element : 043"  # scripted group (container) (typed FeaturePython)
  n = 2
  ref = C_element
FEATURE [App::DocumentObjectGroupPython] H_element079  label="H_element : 041"  # scripted group (container) (typed FeaturePython)
  n = 4
  ref = H_element
FEATURE [App::DocumentObjectGroupPython] G4_POLYPROPYLENE  # scripted group (container) (typed FeaturePython)
  Dunit = g/cm3
  Dvalue = 0.9
  Group = -> [C_element085,H_element079]
  conduct = 2
  density = 1
  expand = 3
  formula = G4_POLYPROPYLENE
  name = G4_POLYPROPYLENE
  specific = 4
FEATURE [App::DocumentObjectGroupPython] C_element086  label="C_element : 044"  # scripted group (container) (typed FeaturePython)
  n = 8
  ref = C_element
FEATURE [App::DocumentObjectGroupPython] H_element080  label="H_element : 042"  # scripted group (container) (typed FeaturePython)
  n = 8
  ref = H_element
FEATURE [App::DocumentObjectGroupPython] G4_POLYSTYRENE  # scripted group (container) (typed FeaturePython)
  Dunit = g/cm3
  Dvalue = 1.06
  Group = -> [C_element086,H_element080]
  conduct = 2
  density = 1
  expand = 3
  formula = G4_POLYSTYRENE
  name = G4_POLYSTYRENE
  specific = 4
FEATURE [App::DocumentObjectGroupPython] C_element087  label="C_element : 045"  # scripted group (container) (typed FeaturePython)
  n = 2
  ref = C_element
FEATURE [App::DocumentObjectGroupPython] F_element014  label="F_element : 4"  # scripted group (container) (typed FeaturePython)
  n = 4
  ref = F_element
FEATURE [App::DocumentObjectGroupPython] G4_TEFLON  # scripted group (container) (typed FeaturePython)
  Dunit = g/cm3
  Dvalue = 2.2
  Group = -> [C_element087,F_element014]
  conduct = 2
  density = 1
  expand = 3
  formula = G4_TEFLON
  name = G4_TEFLON
  specific = 4
FEATURE [App::DocumentObjectGroupPython] C_element088  label="C_element : 046"  # scripted group (container) (typed FeaturePython)
  n = 2
  ref = C_element
FEATURE [App::DocumentObjectGroupPython] F_element015  label="F_element : 006"  # scripted group (container) (typed FeaturePython)
  n = 3
  ref = F_element
FEATURE [App::DocumentObjectGroupPython] Cl_element018  label="Cl_element : 008"  # scripted group (container) (typed FeaturePython)
  n = 1
  ref = Cl_element
FEATURE [App::DocumentObjectGroupPython] G4_POLYTRIFLUOROCHLOROETHYLENE  # scripted group (container) (typed FeaturePython)
  Dunit = g/cm3
  Dvalue = 2.1
  Group = -> [C_element088,F_element015,Cl_element018]
  conduct = 2
  density = 1
  expand = 3
  formula = G4_POLYTRIFLUOROCHLOROETHYLENE
  name = G4_POLYTRIFLUOROCHLOROETHYLENE
  specific = 4
FEATURE [App::DocumentObjectGroupPython] C_element089  label="C_element : 047"  # scripted group (container) (typed FeaturePython)
  n = 4
  ref = C_element
FEATURE [App::DocumentObjectGroupPython] H_element081  label="H_element : 043"  # scripted group (container) (typed FeaturePython)
  n = 6
  ref = H_element
FEATURE [App::DocumentObjectGroupPython] O_element081  label="O_element : 042"  # scripted group (container) (typed FeaturePython)
  n = 2
  ref = O_element
FEATURE [App::DocumentObjectGroupPython] G4_POLYVINYL_ACETATE  # scripted group (container) (typed FeaturePython)
  Dunit = g/cm3
  Dvalue = 1.19
  Group = -> [C_element089,H_element081,O_element081]
  conduct = 2
  density = 1
  expand = 3
  formula = G4_POLYVINYL_ACETATE
  name = G4_POLYVINYL_ACETATE
  specific = 4
FEATURE [App::DocumentObjectGroupPython] C_element090  label="C_element : 048"  # scripted group (container) (typed FeaturePython)
  n = 2
  ref = C_element
FEATURE [App::DocumentObjectGroupPython] H_element082  label="H_element : 044"  # scripted group (container) (typed FeaturePython)
  n = 4
  ref = H_element
FEATURE [App::DocumentObjectGroupPython] O_element082  label="O_element : 043"  # scripted group (container) (typed FeaturePython)
  n = 1
  ref = O_element
FEATURE [App::DocumentObjectGroupPython] G4_POLYVINYL_ALCOHOL  # scripted group (container) (typed FeaturePython)
  Dunit = g/cm3
  Dvalue = 1.3
  Group = -> [C_element090,H_element082,O_element082]
  conduct = 2
  density = 1
  expand = 3
  formula = G4_POLYVINYL_ALCOHOL
  name = G4_POLYVINYL_ALCOHOL
  specific = 4
FEATURE [App::DocumentObjectGroupPython] C_element091  label="C_element : 049"  # scripted group (container) (typed FeaturePython)
  n = 8
  ref = C_element
FEATURE [App::DocumentObjectGroupPython] H_element083  label="H_element : 045"  # scripted group (container) (typed FeaturePython)
  n = 14
  ref = H_element
FEATURE [App::DocumentObjectGroupPython] O_element083  label="O_element : 044"  # scripted group (container) (typed FeaturePython)
  n = 2
  ref = O_element
FEATURE [App::DocumentObjectGroupPython] G4_POLYVINYL_BUTYRAL  # scripted group (container) (typed FeaturePython)
  Dunit = g/cm3
  Dvalue = 1.12
  Group = -> [C_element091,H_element083,O_element083]
  conduct = 2
  density = 1
  expand = 3
  formula = G4_POLYVINYL_BUTYRAL
  name = G4_POLYVINYL_BUTYRAL
  specific = 4
FEATURE [App::DocumentObjectGroupPython] C_element092  label="C_element : 050"  # scripted group (container) (typed FeaturePython)
  n = 2
  ref = C_element
FEATURE [App::DocumentObjectGroupPython] H_element084  label="H_element : 046"  # scripted group (container) (typed FeaturePython)
  n = 3
  ref = H_element
FEATURE [App::DocumentObjectGroupPython] Cl_element019  label="Cl_element : 009"  # scripted group (container) (typed FeaturePython)
  n = 1
  ref = Cl_element
FEATURE [App::DocumentObjectGroupPython] G4_POLYVINYL_CHLORIDE  # scripted group (container) (typed FeaturePython)
  Dunit = g/cm3
  Dvalue = 1.3
  Group = -> [C_element092,H_element084,Cl_element019]
  conduct = 2
  density = 1
  expand = 3
  formula = G4_POLYVINYL_CHLORIDE
  name = G4_POLYVINYL_CHLORIDE
  specific = 4
FEATURE [App::DocumentObjectGroupPython] C_element093  label="C_element : 051"  # scripted group (container) (typed FeaturePython)
  n = 2
  ref = C_element
FEATURE [App::DocumentObjectGroupPython] H_element085  label="H_element : 047"  # scripted group (container) (typed FeaturePython)
  n = 2
  ref = H_element
FEATURE [App::DocumentObjectGroupPython] Cl_element020  label="Cl_element : 010"  # scripted group (container) (typed FeaturePython)
  n = 2
  ref = Cl_element
FEATURE [App::DocumentObjectGroupPython] G4_POLYVINYLIDENE_CHLORIDE  # scripted group (container) (typed FeaturePython)
  Dunit = g/cm3
  Dvalue = 1.7
  Group = -> [C_element093,H_element085,Cl_element020]
  conduct = 2
  density = 1
  expand = 3
  formula = G4_POLYVINYLIDENE_CHLORIDE
  name = G4_POLYVINYLIDENE_CHLORIDE
  specific = 4
FEATURE [App::DocumentObjectGroupPython] C_element094  label="C_element : 052"  # scripted group (container) (typed FeaturePython)
  n = 2
  ref = C_element
FEATURE [App::DocumentObjectGroupPython] H_element086  label="H_element : 048"  # scripted group (container) (typed FeaturePython)
  n = 2
  ref = H_element
FEATURE [App::DocumentObjectGroupPython] F_element016  label="F_element : 007"  # scripted group (container) (typed FeaturePython)
  n = 2
  ref = F_element
FEATURE [App::DocumentObjectGroupPython] G4_POLYVINYLIDENE_FLUORIDE  # scripted group (container) (typed FeaturePython)
  Dunit = g/cm3
  Dvalue = 1.76
  Group = -> [C_element094,H_element086,F_element016]
  conduct = 2
  density = 1
  expand = 3
  formula = G4_POLYVINYLIDENE_FLUORIDE
  name = G4_POLYVINYLIDENE_FLUORIDE
  specific = 4
FEATURE [App::DocumentObjectGroupPython] C_element095  label="C_element : 053"  # scripted group (container) (typed FeaturePython)
  n = 6
  ref = C_element
FEATURE [App::DocumentObjectGroupPython] H_element087  label="H_element : 9"  # scripted group (container) (typed FeaturePython)
  n = 9
  ref = H_element
FEATURE [App::DocumentObjectGroupPython] N_element037  label="N_element : 016"  # scripted group (container) (typed FeaturePython)
  n = 1
  ref = N_element
FEATURE [App::DocumentObjectGroupPython] O_element084  label="O_element : 045"  # scripted group (container) (typed FeaturePython)
  n = 1
  ref = O_element
FEATURE [App::DocumentObjectGroupPython] G4_POLYVINYL_PYRROLIDONE  # scripted group (container) (typed FeaturePython)
  Dunit = g/cm3
  Dvalue = 1.25
  Group = -> [C_element095,H_element087,N_element037,O_element084]
  conduct = 2
  density = 1
  expand = 3
  formula = G4_POLYVINYL_PYRROLIDONE
  name = G4_POLYVINYL_PYRROLIDONE
  specific = 4
FEATURE [App::DocumentObjectGroupPython] K_element008  label="K_element : 1"  # scripted group (container) (typed FeaturePython)
  n = 1
  ref = K_element
FEATURE [App::DocumentObjectGroupPython] I_element006  label="I_element : 003"  # scripted group (container) (typed FeaturePython)
  n = 1
  ref = I_element
FEATURE [App::DocumentObjectGroupPython] G4_POTASSIUM_IODIDE  # scripted group (container) (typed FeaturePython)
  Dunit = g/cm3
  Dvalue = 3.13
  Group = -> [K_element008,I_element006]
  conduct = 2
  density = 1
  expand = 3
  formula = G4_POTASSIUM_IODIDE
  name = G4_POTASSIUM_IODIDE
  specific = 4
FEATURE [App::DocumentObjectGroupPython] K_element009  label="K_element : 2"  # scripted group (container) (typed FeaturePython)
  n = 2
  ref = K_element
FEATURE [App::DocumentObjectGroupPython] O_element085  label="O_element : 046"  # scripted group (container) (typed FeaturePython)
  n = 1
  ref = O_element
FEATURE [App::DocumentObjectGroupPython] G4_POTASSIUM_OXIDE  # scripted group (container) (typed FeaturePython)
  Dunit = g/cm3
  Dvalue = 2.32
  Group = -> [K_element009,O_element085]
  conduct = 2
  density = 1
  expand = 3
  formula = G4_POTASSIUM_OXIDE
  name = G4_POTASSIUM_OXIDE
  specific = 4
FEATURE [App::DocumentObjectGroupPython] C_element096  label="C_element : 054"  # scripted group (container) (typed FeaturePython)
  n = 3
  ref = C_element
FEATURE [App::DocumentObjectGroupPython] H_element088  label="H_element : 049"  # scripted group (container) (typed FeaturePython)
  n = 8
  ref = H_element
FEATURE [App::DocumentObjectGroupPython] G4_PROPANE  # scripted group (container) (typed FeaturePython)
  Dunit = g/cm3
  Dvalue = 0.00187939
  Group = -> [C_element096,H_element088]
  conduct = 2
  density = 1
  expand = 3
  formula = G4_PROPANE
  name = G4_PROPANE
  specific = 4
FEATURE [App::DocumentObjectGroupPython] C_element097  label="C_element : 055"  # scripted group (container) (typed FeaturePython)
  n = 3
  ref = C_element
FEATURE [App::DocumentObjectGroupPython] H_element089  label="H_element : 050"  # scripted group (container) (typed FeaturePython)
  n = 8
  ref = H_element
FEATURE [App::DocumentObjectGroupPython] G4_lPROPANE  # scripted group (container) (typed FeaturePython)
  Dunit = g/cm3
  Dvalue = 0.43
  Group = -> [C_element097,H_element089]
  conduct = 2
  density = 1
  expand = 3
  formula = G4_lPROPANE
  name = G4_lPROPANE
  specific = 4
FEATURE [App::DocumentObjectGroupPython] C_element098  label="C_element : 056"  # scripted group (container) (typed FeaturePython)
  n = 3
  ref = C_element
FEATURE [App::DocumentObjectGroupPython] H_element090  label="H_element : 051"  # scripted group (container) (typed FeaturePython)
  n = 8
  ref = H_element
FEATURE [App::DocumentObjectGroupPython] O_element086  label="O_element : 047"  # scripted group (container) (typed FeaturePython)
  n = 1
  ref = O_element
FEATURE [App::DocumentObjectGroupPython] G4_N_PROPYL_ALCOHOL  label="G4_N-PROPYL_ALCOHOL"  # scripted group (container) (typed FeaturePython)
  Dunit = g/cm3
  Dvalue = 0.8035
  Group = -> [C_element098,H_element090,O_element086]
  conduct = 2
  density = 1
  expand = 3
  formula = G4_N-PROPYL_ALCOHOL
  name = G4_N-PROPYL_ALCOHOL
  specific = 4
FEATURE [App::DocumentObjectGroupPython] C_element099  label="C_element : 057"  # scripted group (container) (typed FeaturePython)
  n = 5
  ref = C_element
FEATURE [App::DocumentObjectGroupPython] H_element091  label="H_element : 052"  # scripted group (container) (typed FeaturePython)
  n = 5
  ref = H_element
FEATURE [App::DocumentObjectGroupPython] N_element038  label="N_element : 017"  # scripted group (container) (typed FeaturePython)
  n = 1
  ref = N_element
FEATURE [App::DocumentObjectGroupPython] G4_PYRIDINE  # scripted group (container) (typed FeaturePython)
  Dunit = g/cm3
  Dvalue = 0.9819
  Group = -> [C_element099,H_element091,N_element038]
  conduct = 2
  density = 1
  expand = 3
  formula = G4_PYRIDINE
  name = G4_PYRIDINE
  specific = 4
FEATURE [App::DocumentObjectGroupPython] H_element092  label="H_element : 0.144"  # scripted group (container) (typed FeaturePython)
  n = 0.143711
FEATURE [App::DocumentObjectGroupPython] C_element100  label="C_element : 0.856"  # scripted group (container) (typed FeaturePython)
  n = 0.856289
FEATURE [App::DocumentObjectGroupPython] G4_RUBBER_BUTYL  # scripted group (container) (typed FeaturePython)
  Dunit = g/cm3
  Dvalue = 0.92
  Group = -> [H_element092,C_element100]
  conduct = 2
  density = 1
  expand = 3
  formula = G4_RUBBER_BUTYL
  name = G4_RUBBER_BUTYL
  specific = 4
FEATURE [App::DocumentObjectGroupPython] H_element093  label="H_element : 0.118"  # scripted group (container) (typed FeaturePython)
  n = 0.118371
FEATURE [App::DocumentObjectGroupPython] C_element101  label="C_element : 0.882"  # scripted group (container) (typed FeaturePython)
  n = 0.881629
FEATURE [App::DocumentObjectGroupPython] G4_RUBBER_NATURAL  # scripted group (container) (typed FeaturePython)
  Dunit = g/cm3
  Dvalue = 0.92
  Group = -> [H_element093,C_element101]
  conduct = 2
  density = 1
  expand = 3
  formula = G4_RUBBER_NATURAL
  name = G4_RUBBER_NATURAL
  specific = 4
FEATURE [App::DocumentObjectGroupPython] H_element094  label="H_element : 0.145"  # scripted group (container) (typed FeaturePython)
  n = 0.05692
FEATURE [App::DocumentObjectGroupPython] C_element102  label="C_element : 0.543"  # scripted group (container) (typed FeaturePython)
  n = 0.542646
FEATURE [App::DocumentObjectGroupPython] Cl_element021  label="Cl_element : 0.400"  # scripted group (container) (typed FeaturePython)
  n = 0.400434
FEATURE [App::DocumentObjectGroupPython] G4_RUBBER_NEOPRENE  # scripted group (container) (typed FeaturePython)
  Dunit = g/cm3
  Dvalue = 1.23
  Group = -> [H_element094,C_element102,Cl_element021]
  conduct = 2
  density = 1
  expand = 3
  formula = G4_RUBBER_NEOPRENE
  name = G4_RUBBER_NEOPRENE
  specific = 4
FEATURE [App::DocumentObjectGroupPython] Si_element006  label="Si_element : 1"  # scripted group (container) (typed FeaturePython)
  n = 1
  ref = Si_element
FEATURE [App::DocumentObjectGroupPython] O_element087  label="O_element : 048"  # scripted group (container) (typed FeaturePython)
  n = 2
  ref = O_element
FEATURE [App::DocumentObjectGroupPython] G4_SILICON_DIOXIDE  # scripted group (container) (typed FeaturePython)
  Dunit = g/cm3
  Dvalue = 2.32
  Group = -> [Si_element006,O_element087]
  conduct = 2
  density = 1
  expand = 3
  formula = G4_SILICON_DIOXIDE
  name = G4_SILICON_DIOXIDE
  specific = 4
FEATURE [App::DocumentObjectGroupPython] Ag_element002  label="Ag_element : 1"  # scripted group (container) (typed FeaturePython)
  n = 1
  ref = Ag_element
FEATURE [App::DocumentObjectGroupPython] Br_element005  label="Br_element : 003"  # scripted group (container) (typed FeaturePython)
  n = 1
  ref = Br_element
FEATURE [App::DocumentObjectGroupPython] G4_SILVER_BROMIDE  # scripted group (container) (typed FeaturePython)
  Dunit = g/cm3
  Dvalue = 6.473
  Group = -> [Ag_element002,Br_element005]
  conduct = 2
  density = 1
  expand = 3
  formula = G4_SILVER_BROMIDE
  name = G4_SILVER_BROMIDE
  specific = 4
FEATURE [App::DocumentObjectGroupPython] Ag_element003  label="Ag_element : 002"  # scripted group (container) (typed FeaturePython)
  n = 1
  ref = Ag_element
FEATURE [App::DocumentObjectGroupPython] Cl_element022  label="Cl_element : 011"  # scripted group (container) (typed FeaturePython)
  n = 1
  ref = Cl_element
FEATURE [App::DocumentObjectGroupPython] G4_SILVER_CHLORIDE  # scripted group (container) (typed FeaturePython)
  Dunit = g/cm3
  Dvalue = 5.56
  Group = -> [Ag_element003,Cl_element022]
  conduct = 2
  density = 1
  expand = 3
  formula = G4_SILVER_CHLORIDE
  name = G4_SILVER_CHLORIDE
  specific = 4
FEATURE [App::DocumentObjectGroupPython] Br_element006  label="Br_element : 0.423"  # scripted group (container) (typed FeaturePython)
  n = 0.422895
FEATURE [App::DocumentObjectGroupPython] Ag_element004  label="Ag_element : 0.574"  # scripted group (container) (typed FeaturePython)
  n = 0.573748
FEATURE [App::DocumentObjectGroupPython] I_element007  label="I_element : 0.649"  # scripted group (container) (typed FeaturePython)
  n = 0.003357
FEATURE [App::DocumentObjectGroupPython] G4_SILVER_HALIDES  # scripted group (container) (typed FeaturePython)
  Dunit = g/cm3
  Dvalue = 6.47
  Group = -> [Br_element006,Ag_element004,I_element007]
  conduct = 2
  density = 1
  expand = 3
  formula = G4_SILVER_HALIDES
  name = G4_SILVER_HALIDES
  specific = 4
FEATURE [App::DocumentObjectGroupPython] Ag_element005  label="Ag_element : 003"  # scripted group (container) (typed FeaturePython)
  n = 1
  ref = Ag_element
FEATURE [App::DocumentObjectGroupPython] I_element008  label="I_element : 004"  # scripted group (container) (typed FeaturePython)
  n = 1
  ref = I_element
FEATURE [App::DocumentObjectGroupPython] G4_SILVER_IODIDE  # scripted group (container) (typed FeaturePython)
  Dunit = g/cm3
  Dvalue = 6.01
  Group = -> [Ag_element005,I_element008]
  conduct = 2
  density = 1
  expand = 3
  formula = G4_SILVER_IODIDE
  name = G4_SILVER_IODIDE
  specific = 4
FEATURE [App::DocumentObjectGroupPython] H_element095  label="H_element : 0.100"  # scripted group (container) (typed FeaturePython)
  n = 0.1
FEATURE [App::DocumentObjectGroupPython] C_element103  label="C_element : 0.204"  # scripted group (container) (typed FeaturePython)
  n = 0.204
FEATURE [App::DocumentObjectGroupPython] N_element039  label="N_element : 0.759"  # scripted group (container) (typed FeaturePython)
  n = 0.042
FEATURE [App::DocumentObjectGroupPython] O_element088  label="O_element : 0.645"  # scripted group (container) (typed FeaturePython)
  n = 0.645
FEATURE [App::DocumentObjectGroupPython] Na_element013  label="Na_element : 0.100"  # scripted group (container) (typed FeaturePython)
  n = 0.002
FEATURE [App::DocumentObjectGroupPython] P_element009  label="P_element : 0.107"  # scripted group (container) (typed FeaturePython)
  n = 0.001
FEATURE [App::DocumentObjectGroupPython] S_element020  label="S_element : 0.021"  # scripted group (container) (typed FeaturePython)
  n = 0.002
FEATURE [App::DocumentObjectGroupPython] Cl_element023  label="Cl_element : 0.590"  # scripted group (container) (typed FeaturePython)
  n = 0.003
FEATURE [App::DocumentObjectGroupPython] K_element010  label="K_element : 0.001"  # scripted group (container) (typed FeaturePython)
  n = 0.001
FEATURE [App::DocumentObjectGroupPython] G4_SKIN_ICRP  # scripted group (container) (typed FeaturePython)
  Dunit = g/cm3
  Dvalue = 1.09
  Group = -> [H_element095,C_element103,N_element039,O_element088,Na_element013,P_element009,S_element020,Cl_element023,K_element010]
  conduct = 2
  density = 1
  expand = 3
  formula = G4_SKIN_ICRP
  name = G4_SKIN_ICRP
  specific = 4
FEATURE [App::DocumentObjectGroupPython] Na_element014  label="Na_element : 2"  # scripted group (container) (typed FeaturePython)
  n = 2
  ref = Na_element
FEATURE [App::DocumentObjectGroupPython] C_element104  label="C_element : 058"  # scripted group (container) (typed FeaturePython)
  n = 1
  ref = C_element
FEATURE [App::DocumentObjectGroupPython] O_element089  label="O_element : 049"  # scripted group (container) (typed FeaturePython)
  n = 3
  ref = O_element
FEATURE [App::DocumentObjectGroupPython] G4_SODIUM_CARBONATE  # scripted group (container) (typed FeaturePython)
  Dunit = g/cm3
  Dvalue = 2.532
  Group = -> [Na_element014,C_element104,O_element089]
  conduct = 2
  density = 1
  expand = 3
  formula = G4_SODIUM_CARBONATE
  name = G4_SODIUM_CARBONATE
  specific = 4
FEATURE [App::DocumentObjectGroupPython] Na_element015  label="Na_element : 1"  # scripted group (container) (typed FeaturePython)
  n = 1
  ref = Na_element
FEATURE [App::DocumentObjectGroupPython] I_element009  label="I_element : 005"  # scripted group (container) (typed FeaturePython)
  n = 1
  ref = I_element
FEATURE [App::DocumentObjectGroupPython] G4_SODIUM_IODIDE  # scripted group (container) (typed FeaturePython)
  Dunit = g/cm3
  Dvalue = 3.667
  Group = -> [Na_element015,I_element009]
  conduct = 2
  density = 1
  expand = 3
  formula = G4_SODIUM_IODIDE
  name = G4_SODIUM_IODIDE
  specific = 4
FEATURE [App::DocumentObjectGroupPython] Na_element016  label="Na_element : 003"  # scripted group (container) (typed FeaturePython)
  n = 2
  ref = Na_element
FEATURE [App::DocumentObjectGroupPython] O_element090  label="O_element : 050"  # scripted group (container) (typed FeaturePython)
  n = 1
  ref = O_element
FEATURE [App::DocumentObjectGroupPython] G4_SODIUM_MONOXIDE  # scripted group (container) (typed FeaturePython)
  Dunit = g/cm3
  Dvalue = 2.27
  Group = -> [Na_element016,O_element090]
  conduct = 2
  density = 1
  expand = 3
  formula = G4_SODIUM_MONOXIDE
  name = G4_SODIUM_MONOXIDE
  specific = 4
FEATURE [App::DocumentObjectGroupPython] Na_element017  label="Na_element : 004"  # scripted group (container) (typed FeaturePython)
  n = 1
  ref = Na_element
FEATURE [App::DocumentObjectGroupPython] N_element040  label="N_element : 018"  # scripted group (container) (typed FeaturePython)
  n = 1
  ref = N_element
FEATURE [App::DocumentObjectGroupPython] O_element091  label="O_element : 051"  # scripted group (container) (typed FeaturePython)
  n = 3
  ref = O_element
FEATURE [App::DocumentObjectGroupPython] G4_SODIUM_NITRATE  # scripted group (container) (typed FeaturePython)
  Dunit = g/cm3
  Dvalue = 2.261
  Group = -> [Na_element017,N_element040,O_element091]
  conduct = 2
  density = 1
  expand = 3
  formula = G4_SODIUM_NITRATE
  name = G4_SODIUM_NITRATE
  specific = 4
FEATURE [App::DocumentObjectGroupPython] C_element105  label="C_element : 059"  # scripted group (container) (typed FeaturePython)
  n = 14
  ref = C_element
FEATURE [App::DocumentObjectGroupPython] H_element096  label="H_element : 053"  # scripted group (container) (typed FeaturePython)
  n = 12
  ref = H_element
FEATURE [App::DocumentObjectGroupPython] G4_STILBENE  # scripted group (container) (typed FeaturePython)
  Dunit = g/cm3
  Dvalue = 0.9707
  Group = -> [C_element105,H_element096]
  conduct = 2
  density = 1
  expand = 3
  formula = G4_STILBENE
  name = G4_STILBENE
  specific = 4
FEATURE [App::DocumentObjectGroupPython] C_element106  label="C_element : 12"  # scripted group (container) (typed FeaturePython)
  n = 12
  ref = C_element
FEATURE [App::DocumentObjectGroupPython] H_element097  label="H_element : 22"  # scripted group (container) (typed FeaturePython)
  n = 22
  ref = H_element
FEATURE [App::DocumentObjectGroupPython] O_element092  label="O_element : 11"  # scripted group (container) (typed FeaturePython)
  n = 11
  ref = O_element
FEATURE [App::DocumentObjectGroupPython] G4_SUCROSE  # scripted group (container) (typed FeaturePython)
  Dunit = g/cm3
  Dvalue = 1.5805
  Group = -> [C_element106,H_element097,O_element092]
  conduct = 2
  density = 1
  expand = 3
  formula = G4_SUCROSE
  name = G4_SUCROSE
  specific = 4
FEATURE [App::DocumentObjectGroupPython] C_element107  label="C_element : 18"  # scripted group (container) (typed FeaturePython)
  n = 18
  ref = C_element
FEATURE [App::DocumentObjectGroupPython] H_element098  label="H_element : 054"  # scripted group (container) (typed FeaturePython)
  n = 14
  ref = H_element
FEATURE [App::DocumentObjectGroupPython] G4_TERPHENYL  # scripted group (container) (typed FeaturePython)
  Dunit = g/cm3
  Dvalue = 1.24
  Group = -> [C_element107,H_element098]
  conduct = 2
  density = 1
  expand = 3
  formula = G4_TERPHENYL
  name = G4_TERPHENYL
  specific = 4
FEATURE [App::DocumentObjectGroupPython] H_element099  label="H_element : 0.146"  # scripted group (container) (typed FeaturePython)
  n = 0.106
FEATURE [App::DocumentObjectGroupPython] C_element108  label="C_element : 0.883"  # scripted group (container) (typed FeaturePython)
  n = 0.099
FEATURE [App::DocumentObjectGroupPython] N_element041  label="N_element : 0.020"  # scripted group (container) (typed FeaturePython)
  n = 0.02
FEATURE [App::DocumentObjectGroupPython] O_element093  label="O_element : 0.766"  # scripted group (container) (typed FeaturePython)
  n = 0.766
FEATURE [App::DocumentObjectGroupPython] Na_element018  label="Na_element : 0.101"  # scripted group (container) (typed FeaturePython)
  n = 0.002
FEATURE [App::DocumentObjectGroupPython] P_element010  label="P_element : 0.108"  # scripted group (container) (typed FeaturePython)
  n = 0.001
FEATURE [App::DocumentObjectGroupPython] S_element021  label="S_element : 0.022"  # scripted group (container) (typed FeaturePython)
  n = 0.002
FEATURE [App::DocumentObjectGroupPython] Cl_element024  label="Cl_element : 0.002"  # scripted group (container) (typed FeaturePython)
  n = 0.002
FEATURE [App::DocumentObjectGroupPython] K_element011  label="K_element : 0.017"  # scripted group (container) (typed FeaturePython)
  n = 0.002
FEATURE [App::DocumentObjectGroupPython] G4_TESTIS_ICRP  # scripted group (container) (typed FeaturePython)
  Dunit = g/cm3
  Dvalue = 1.04
  Group = -> [H_element099,C_element108,N_element041,O_element093,Na_element018,P_element010,S_element021,Cl_element024,K_element011]
  conduct = 2
  density = 1
  expand = 3
  formula = G4_TESTIS_ICRP
  name = G4_TESTIS_ICRP
  specific = 4
FEATURE [App::DocumentObjectGroupPython] C_element109  label="C_element : 060"  # scripted group (container) (typed FeaturePython)
  n = 2
  ref = C_element
FEATURE [App::DocumentObjectGroupPython] Cl_element025  label="Cl_element : 012"  # scripted group (container) (typed FeaturePython)
  n = 4
  ref = Cl_element
FEATURE [App::DocumentObjectGroupPython] G4_TETRACHLOROETHYLENE  # scripted group (container) (typed FeaturePython)
  Dunit = g/cm3
  Dvalue = 1.625
  Group = -> [C_element109,Cl_element025]
  conduct = 2
  density = 1
  expand = 3
  formula = G4_TETRACHLOROETHYLENE
  name = G4_TETRACHLOROETHYLENE
  specific = 4
FEATURE [App::DocumentObjectGroupPython] Tl_element001  label="Tl_element : 1"  # scripted group (container) (typed FeaturePython)
  n = 1
  ref = Tl_element
FEATURE [App::DocumentObjectGroupPython] Cl_element026  label="Cl_element : 013"  # scripted group (container) (typed FeaturePython)
  n = 1
  ref = Cl_element
FEATURE [App::DocumentObjectGroupPython] G4_THALLIUM_CHLORIDE  # scripted group (container) (typed FeaturePython)
  Dunit = g/cm3
  Dvalue = 7.004
  Group = -> [Tl_element001,Cl_element026]
  conduct = 2
  density = 1
  expand = 3
  formula = G4_THALLIUM_CHLORIDE
  name = G4_THALLIUM_CHLORIDE
  specific = 4
FEATURE [App::DocumentObjectGroupPython] H_element100  label="H_element : 0.147"  # scripted group (container) (typed FeaturePython)
  n = 0.105
FEATURE [App::DocumentObjectGroupPython] C_element110  label="C_element : 0.256"  # scripted group (container) (typed FeaturePython)
  n = 0.256
FEATURE [App::DocumentObjectGroupPython] N_element042  label="N_element : 0.760"  # scripted group (container) (typed FeaturePython)
  n = 0.027
FEATURE [App::DocumentObjectGroupPython] O_element094  label="O_element : 0.602"  # scripted group (container) (typed FeaturePython)
  n = 0.602
FEATURE [App::DocumentObjectGroupPython] Na_element019  label="Na_element : 0.102"  # scripted group (container) (typed FeaturePython)
  n = 0.001
FEATURE [App::DocumentObjectGroupPython] P_element011  label="P_element : 0.109"  # scripted group (container) (typed FeaturePython)
  n = 0.002
FEATURE [App::DocumentObjectGroupPython] S_element022  label="S_element : 0.023"  # scripted group (container) (typed FeaturePython)
  n = 0.003
FEATURE [App::DocumentObjectGroupPython] Cl_element027  label="Cl_element : 0.591"  # scripted group (container) (typed FeaturePython)
  n = 0.002
FEATURE [App::DocumentObjectGroupPython] K_element012  label="K_element : 0.018"  # scripted group (container) (typed FeaturePython)
  n = 0.002
FEATURE [App::DocumentObjectGroupPython] G4_TISSUE_SOFT_ICRP  # scripted group (container) (typed FeaturePython)
  Dunit = g/cm3
  Dvalue = 1.03
  Group = -> [H_element100,C_element110,N_element042,O_element094,Na_element019,P_element011,S_element022,Cl_element027,K_element012]
  conduct = 2
  density = 1
  expand = 3
  formula = G4_TISSUE_SOFT_ICRP
  name = G4_TISSUE_SOFT_ICRP
  specific = 4
FEATURE [App::DocumentObjectGroupPython] H_element101  label="H_element : 0.148"  # scripted group (container) (typed FeaturePython)
  n = 0.101
FEATURE [App::DocumentObjectGroupPython] C_element111  label="C_element : 0.111"  # scripted group (container) (typed FeaturePython)
  n = 0.111
FEATURE [App::DocumentObjectGroupPython] N_element043  label="N_element : 0.026"  # scripted group (container) (typed FeaturePython)
  n = 0.026
FEATURE [App::DocumentObjectGroupPython] O_element095  label="O_element : 0.762"  # scripted group (container) (typed FeaturePython)
  n = 0.762
FEATURE [App::DocumentObjectGroupPython] G4_TISSUE_SOFT_ICRU_4  label="G4_TISSUE_SOFT_ICRU-4"  # scripted group (container) (typed FeaturePython)
  Dunit = g/cm3
  Dvalue = 1
  Group = -> [H_element101,C_element111,N_element043,O_element095]
  conduct = 2
  density = 1
  expand = 3
  formula = G4_TISSUE_SOFT_ICRU-4
  name = G4_TISSUE_SOFT_ICRU-4
  specific = 4
FEATURE [App::DocumentObjectGroupPython] H_element102  label="H_element : 0.149"  # scripted group (container) (typed FeaturePython)
  n = 0.101869
FEATURE [App::DocumentObjectGroupPython] C_element112  label="C_element : 0.456"  # scripted group (container) (typed FeaturePython)
  n = 0.456179
FEATURE [App::DocumentObjectGroupPython] N_element044  label="N_element : 0.761"  # scripted group (container) (typed FeaturePython)
  n = 0.035172
FEATURE [App::DocumentObjectGroupPython] O_element096  label="O_element : 0.407"  # scripted group (container) (typed FeaturePython)
  n = 0.40678
FEATURE [App::DocumentObjectGroupPython] G4_TISSUE_METHANE  label="G4_TISSUE-METHANE"  # scripted group (container) (typed FeaturePython)
  Dunit = g/cm3
  Dvalue = 0.00106409
  Group = -> [H_element102,C_element112,N_element044,O_element096]
  conduct = 2
  density = 1
  expand = 3
  formula = G4_TISSUE-METHANE
  name = G4_TISSUE-METHANE
  specific = 4
FEATURE [App::DocumentObjectGroupPython] H_element103  label="H_element : 0.103"  # scripted group (container) (typed FeaturePython)
  n = 0.102672
FEATURE [App::DocumentObjectGroupPython] C_element113  label="C_element : 0.569"  # scripted group (container) (typed FeaturePython)
  n = 0.56894
FEATURE [App::DocumentObjectGroupPython] N_element045  label="N_element : 0.762"  # scripted group (container) (typed FeaturePython)
  n = 0.035022
FEATURE [App::DocumentObjectGroupPython] O_element097  label="O_element : 0.293"  # scripted group (container) (typed FeaturePython)
  n = 0.293366
FEATURE [App::DocumentObjectGroupPython] G4_TISSUE_PROPANE  label="G4_TISSUE-PROPANE"  # scripted group (container) (typed FeaturePython)
  Dunit = g/cm3
  Dvalue = 0.00182628
  Group = -> [H_element103,C_element113,N_element045,O_element097]
  conduct = 2
  density = 1
  expand = 3
  formula = G4_TISSUE-PROPANE
  name = G4_TISSUE-PROPANE
  specific = 4
FEATURE [App::DocumentObjectGroupPython] Ti_element003  label="Ti_element : 1"  # scripted group (container) (typed FeaturePython)
  n = 1
  ref = Ti_element
FEATURE [App::DocumentObjectGroupPython] O_element098  label="O_element : 052"  # scripted group (container) (typed FeaturePython)
  n = 2
  ref = O_element
FEATURE [App::DocumentObjectGroupPython] G4_TITANIUM_DIOXIDE  # scripted group (container) (typed FeaturePython)
  Dunit = g/cm3
  Dvalue = 4.26
  Group = -> [Ti_element003,O_element098]
  conduct = 2
  density = 1
  expand = 3
  formula = G4_TITANIUM_DIOXIDE
  name = G4_TITANIUM_DIOXIDE
  specific = 4
FEATURE [App::DocumentObjectGroupPython] C_element114  label="C_element : 061"  # scripted group (container) (typed FeaturePython)
  n = 7
  ref = C_element
FEATURE [App::DocumentObjectGroupPython] H_element104  label="H_element : 055"  # scripted group (container) (typed FeaturePython)
  n = 8
  ref = H_element
FEATURE [App::DocumentObjectGroupPython] G4_TOLUENE  # scripted group (container) (typed FeaturePython)
  Dunit = g/cm3
  Dvalue = 0.8669
  Group = -> [C_element114,H_element104]
  conduct = 2
  density = 1
  expand = 3
  formula = G4_TOLUENE
  name = G4_TOLUENE
  specific = 4
FEATURE [App::DocumentObjectGroupPython] C_element115  label="C_element : 062"  # scripted group (container) (typed FeaturePython)
  n = 2
  ref = C_element
FEATURE [App::DocumentObjectGroupPython] H_element105  label="H_element : 056"  # scripted group (container) (typed FeaturePython)
  n = 1
  ref = H_element
FEATURE [App::DocumentObjectGroupPython] Cl_element028  label="Cl_element : 014"  # scripted group (container) (typed FeaturePython)
  n = 3
  ref = Cl_element
FEATURE [App::DocumentObjectGroupPython] G4_TRICHLOROETHYLENE  # scripted group (container) (typed FeaturePython)
  Dunit = g/cm3
  Dvalue = 1.46
  Group = -> [C_element115,H_element105,Cl_element028]
  conduct = 2
  density = 1
  expand = 3
  formula = G4_TRICHLOROETHYLENE
  name = G4_TRICHLOROETHYLENE
  specific = 4
FEATURE [App::DocumentObjectGroupPython] C_element116  label="C_element : 063"  # scripted group (container) (typed FeaturePython)
  n = 6
  ref = C_element
FEATURE [App::DocumentObjectGroupPython] H_element106  label="H_element : 15"  # scripted group (container) (typed FeaturePython)
  n = 15
  ref = H_element
FEATURE [App::DocumentObjectGroupPython] O_element099  label="O_element : 053"  # scripted group (container) (typed FeaturePython)
  n = 4
  ref = O_element
FEATURE [App::DocumentObjectGroupPython] P_element012  label="P_element : 1"  # scripted group (container) (typed FeaturePython)
  n = 1
  ref = P_element
FEATURE [App::DocumentObjectGroupPython] G4_TRIETHYL_PHOSPHATE  # scripted group (container) (typed FeaturePython)
  Dunit = g/cm3
  Dvalue = 1.07
  Group = -> [C_element116,H_element106,O_element099,P_element012]
  conduct = 2
  density = 1
  expand = 3
  formula = G4_TRIETHYL_PHOSPHATE
  name = G4_TRIETHYL_PHOSPHATE
  specific = 4
FEATURE [App::DocumentObjectGroupPython] W_element003  label="W_element : 003"  # scripted group (container) (typed FeaturePython)
  n = 1
  ref = W_element
FEATURE [App::DocumentObjectGroupPython] F_element017  label="F_element : 6"  # scripted group (container) (typed FeaturePython)
  n = 6
  ref = F_element
FEATURE [App::DocumentObjectGroupPython] G4_TUNGSTEN_HEXAFLUORIDE  # scripted group (container) (typed FeaturePython)
  Dunit = g/cm3
  Dvalue = 2.4
  Group = -> [W_element003,F_element017]
  conduct = 2
  density = 1
  expand = 3
  formula = G4_TUNGSTEN_HEXAFLUORIDE
  name = G4_TUNGSTEN_HEXAFLUORIDE
  specific = 4
FEATURE [App::DocumentObjectGroupPython] U_element001  label="U_element : 1"  # scripted group (container) (typed FeaturePython)
  n = 1
  ref = U_element
FEATURE [App::DocumentObjectGroupPython] C_element117  label="C_element : 064"  # scripted group (container) (typed FeaturePython)
  n = 2
  ref = C_element
FEATURE [App::DocumentObjectGroupPython] G4_URANIUM_DICARBIDE  # scripted group (container) (typed FeaturePython)
  Dunit = g/cm3
  Dvalue = 11.28
  Group = -> [U_element001,C_element117]
  conduct = 2
  density = 1
  expand = 3
  formula = G4_URANIUM_DICARBIDE
  name = G4_URANIUM_DICARBIDE
  specific = 4
FEATURE [App::DocumentObjectGroupPython] U_element002  label="U_element : 002"  # scripted group (container) (typed FeaturePython)
  n = 1
  ref = U_element
FEATURE [App::DocumentObjectGroupPython] C_element118  label="C_element : 065"  # scripted group (container) (typed FeaturePython)
  n = 1
  ref = C_element
FEATURE [App::DocumentObjectGroupPython] G4_URANIUM_MONOCARBIDE  # scripted group (container) (typed FeaturePython)
  Dunit = g/cm3
  Dvalue = 13.63
  Group = -> [U_element002,C_element118]
  conduct = 2
  density = 1
  expand = 3
  formula = G4_URANIUM_MONOCARBIDE
  name = G4_URANIUM_MONOCARBIDE
  specific = 4
FEATURE [App::DocumentObjectGroupPython] U_element003  label="U_element : 003"  # scripted group (container) (typed FeaturePython)
  n = 1
  ref = U_element
FEATURE [App::DocumentObjectGroupPython] O_element100  label="O_element : 054"  # scripted group (container) (typed FeaturePython)
  n = 2
  ref = O_element
FEATURE [App::DocumentObjectGroupPython] G4_URANIUM_OXIDE  # scripted group (container) (typed FeaturePython)
  Dunit = g/cm3
  Dvalue = 10.96
  Group = -> [U_element003,O_element100]
  conduct = 2
  density = 1
  expand = 3
  formula = G4_URANIUM_OXIDE
  name = G4_URANIUM_OXIDE
  specific = 4
FEATURE [App::DocumentObjectGroupPython] C_element119  label="C_element : 066"  # scripted group (container) (typed FeaturePython)
  n = 1
  ref = C_element
FEATURE [App::DocumentObjectGroupPython] H_element107  label="H_element : 057"  # scripted group (container) (typed FeaturePython)
  n = 4
  ref = H_element
FEATURE [App::DocumentObjectGroupPython] N_element046  label="N_element : 019"  # scripted group (container) (typed FeaturePython)
  n = 2
  ref = N_element
FEATURE [App::DocumentObjectGroupPython] O_element101  label="O_element : 055"  # scripted group (container) (typed FeaturePython)
  n = 1
  ref = O_element
FEATURE [App::DocumentObjectGroupPython] G4_UREA  # scripted group (container) (typed FeaturePython)
  Dunit = g/cm3
  Dvalue = 1.323
  Group = -> [C_element119,H_element107,N_element046,O_element101]
  conduct = 2
  density = 1
  expand = 3
  formula = G4_UREA
  name = G4_UREA
  specific = 4
FEATURE [App::DocumentObjectGroupPython] C_element120  label="C_element : 067"  # scripted group (container) (typed FeaturePython)
  n = 5
  ref = C_element
FEATURE [App::DocumentObjectGroupPython] H_element108  label="H_element : 058"  # scripted group (container) (typed FeaturePython)
  n = 11
  ref = H_element
FEATURE [App::DocumentObjectGroupPython] N_element047  label="N_element : 020"  # scripted group (container) (typed FeaturePython)
  n = 1
  ref = N_element
FEATURE [App::DocumentObjectGroupPython] O_element102  label="O_element : 056"  # scripted group (container) (typed FeaturePython)
  n = 2
  ref = O_element
FEATURE [App::DocumentObjectGroupPython] G4_VALINE  # scripted group (container) (typed FeaturePython)
  Dunit = g/cm3
  Dvalue = 1.23
  Group = -> [C_element120,H_element108,N_element047,O_element102]
  conduct = 2
  density = 1
  expand = 3
  formula = G4_VALINE
  name = G4_VALINE
  specific = 4
FEATURE [App::DocumentObjectGroupPython] H_element109  label="H_element : 0.009"  # scripted group (container) (typed FeaturePython)
  n = 0.009417
FEATURE [App::DocumentObjectGroupPython] C_element121  label="C_element : 0.281"  # scripted group (container) (typed FeaturePython)
  n = 0.280555
FEATURE [App::DocumentObjectGroupPython] F_element018  label="F_element : 0.710"  # scripted group (container) (typed FeaturePython)
  n = 0.710028
FEATURE [App::DocumentObjectGroupPython] G4_VITON  # scripted group (container) (typed FeaturePython)
  Dunit = g/cm3
  Dvalue = 1.8
  Group = -> [H_element109,C_element121,F_element018]
  conduct = 2
  density = 1
  expand = 3
  formula = G4_VITON
  name = G4_VITON
  specific = 4
FEATURE [App::DocumentObjectGroupPython] H_element110  label="H_element : 059"  # scripted group (container) (typed FeaturePython)
  n = 2
  ref = H_element
FEATURE [App::DocumentObjectGroupPython] O_element103  label="O_element : 057"  # scripted group (container) (typed FeaturePython)
  n = 1
  ref = O_element
FEATURE [App::DocumentObjectGroupPython] G4_WATER  # scripted group (container) (typed FeaturePython)
  Dunit = g/cm3
  Dvalue = 1
  Group = -> [H_element110,O_element103]
  conduct = 2
  density = 1
  expand = 3
  formula = G4_WATER
  name = G4_WATER
  specific = 4
FEATURE [App::DocumentObjectGroupPython] H_element111  label="H_element : 060"  # scripted group (container) (typed FeaturePython)
  n = 2
  ref = H_element
FEATURE [App::DocumentObjectGroupPython] O_element104  label="O_element : 058"  # scripted group (container) (typed FeaturePython)
  n = 1
  ref = O_element
FEATURE [App::DocumentObjectGroupPython] G4_WATER_VAPOR  # scripted group (container) (typed FeaturePython)
  Dunit = g/cm3
  Dvalue = 0.000756182
  Group = -> [H_element111,O_element104]
  conduct = 2
  density = 1
  expand = 3
  formula = G4_WATER_VAPOR
  name = G4_WATER_VAPOR
  specific = 4
FEATURE [App::DocumentObjectGroupPython] C_element122  label="C_element : 068"  # scripted group (container) (typed FeaturePython)
  n = 8
  ref = C_element
FEATURE [App::DocumentObjectGroupPython] H_element112  label="H_element : 061"  # scripted group (container) (typed FeaturePython)
  n = 10
  ref = H_element
FEATURE [App::DocumentObjectGroupPython] G4_XYLENE  # scripted group (container) (typed FeaturePython)
  Dunit = g/cm3
  Dvalue = 0.87
  Group = -> [C_element122,H_element112]
  conduct = 2
  density = 1
  expand = 3
  formula = G4_XYLENE
  name = G4_XYLENE
  specific = 4
FEATURE [App::DocumentObjectGroupPython] C_element123  label="C_element : 069"  # scripted group (container) (typed FeaturePython)
  n = 1
  ref = C_element
FEATURE [App::DocumentObjectGroupPython] G4_GRAPHITE  # scripted group (container) (typed FeaturePython)
  Dunit = g/cm3
  Dvalue = 2.21
  Group = -> [C_element123]
  conduct = 2
  density = 1
  expand = 3
  formula = G4_GRAPHITE
  name = G4_GRAPHITE
  specific = 4
FEATURE [App::DocumentObjectGroupPython] NIST  # scripted group (container) (typed FeaturePython)
  Group = -> [G4_A_150_TISSUE,G4_ACETONE,G4_ACETYLENE,G4_ADENINE,G4_ADIPOSE_TISSUE_ICRP,G4_AIR,G4_ALANINE,G4_ALUMINUM_OXIDE,G4_AMBER,G4_AMMONIA,G4_ANILINE,G4_ANTHRACENE,G4_B_100_BONE,G4_BAKELITE,G4_BARIUM_FLUORIDE,G4_BARIUM_SULFATE,G4_BENZENE,G4_BERYLLIUM_OXIDE,G4_BGO,G4_BLOOD_ICRP,G4_BONE_COMPACT_ICRU,G4_BONE_CORTICAL_ICRP,G4_BORON_CARBIDE,G4_BORON_OXIDE,G4_BRAIN_ICRP,G4_BUTANE,G4_N_BUTYL_ALCOHOL,G4_C_552,+152 more]
FEATURE [App::DocumentObjectGroupPython] H_element113  label="H_element : 062"  # scripted group (container) (typed FeaturePython)
  n = 1
  ref = H_element
FEATURE [App::DocumentObjectGroupPython] G4_H  # scripted group (container) (typed FeaturePython)
  Dunit = g/cm3
  Dvalue = 8.3748e-05
  Group = -> [H_element113]
  conduct = 2
  density = 1
  expand = 3
  formula = H
  name = G4_H
  specific = 4
FEATURE [App::DocumentObjectGroupPython] He_element001  label="He_element : 1"  # scripted group (container) (typed FeaturePython)
  n = 1
  ref = He_element
FEATURE [App::DocumentObjectGroupPython] G4_He  # scripted group (container) (typed FeaturePython)
  Dunit = g/cm3
  Dvalue = 0.000166322
  Group = -> [He_element001]
  conduct = 2
  density = 1
  expand = 3
  formula = He
  name = G4_He
  specific = 4
FEATURE [App::DocumentObjectGroupPython] Li_element008  label="Li_element : 008"  # scripted group (container) (typed FeaturePython)
  n = 1
  ref = Li_element
FEATURE [App::DocumentObjectGroupPython] G4_Li  # scripted group (container) (typed FeaturePython)
  Dunit = g/cm3
  Dvalue = 0.534
  Group = -> [Li_element008]
  conduct = 2
  density = 1
  expand = 3
  formula = Li
  name = G4_Li
  specific = 4
FEATURE [App::DocumentObjectGroupPython] Be_element002  label="Be_element : 002"  # scripted group (container) (typed FeaturePython)
  n = 1
  ref = Be_element
FEATURE [App::DocumentObjectGroupPython] G4_Be  # scripted group (container) (typed FeaturePython)
  Dunit = g/cm3
  Dvalue = 1.848
  Group = -> [Be_element002]
  conduct = 2
  density = 1
  expand = 3
  formula = Be
  name = G4_Be
  specific = 4
FEATURE [App::DocumentObjectGroupPython] B_element007  label="B_element : 007"  # scripted group (container) (typed FeaturePython)
  n = 1
  ref = B_element
FEATURE [App::DocumentObjectGroupPython] G4_B  # scripted group (container) (typed FeaturePython)
  Dunit = g/cm3
  Dvalue = 2.37
  Group = -> [B_element007]
  conduct = 2
  density = 1
  expand = 3
  formula = B
  name = G4_B
  specific = 4
FEATURE [App::DocumentObjectGroupPython] C_element124  label="C_element : 070"  # scripted group (container) (typed FeaturePython)
  n = 1
  ref = C_element
FEATURE [App::DocumentObjectGroupPython] G4_C  # scripted group (container) (typed FeaturePython)
  Dunit = g/cm3
  Dvalue = 2
  Group = -> [C_element124]
  conduct = 2
  density = 1
  expand = 3
  formula = C
  name = G4_C
  specific = 4
FEATURE [App::DocumentObjectGroupPython] N_element048  label="N_element : 021"  # scripted group (container) (typed FeaturePython)
  n = 1
  ref = N_element
FEATURE [App::DocumentObjectGroupPython] G4_N  # scripted group (container) (typed FeaturePython)
  Dunit = g/cm3
  Dvalue = 0.0011652
  Group = -> [N_element048]
  conduct = 2
  density = 1
  expand = 3
  formula = N
  name = G4_N
  specific = 4
FEATURE [App::DocumentObjectGroupPython] O_element105  label="O_element : 059"  # scripted group (container) (typed FeaturePython)
  n = 1
  ref = O_element
FEATURE [App::DocumentObjectGroupPython] G4_O  # scripted group (container) (typed FeaturePython)
  Dunit = g/cm3
  Dvalue = 0.00133151
  Group = -> [O_element105]
  conduct = 2
  density = 1
  expand = 3
  formula = O
  name = G4_O
  specific = 4
FEATURE [App::DocumentObjectGroupPython] F_element019  label="F_element : 008"  # scripted group (container) (typed FeaturePython)
  n = 1
  ref = F_element
FEATURE [App::DocumentObjectGroupPython] G4_F  # scripted group (container) (typed FeaturePython)
  Dunit = g/cm3
  Dvalue = 0.00158029
  Group = -> [F_element019]
  conduct = 2
  density = 1
  expand = 3
  formula = F
  name = G4_F
  specific = 4
FEATURE [App::DocumentObjectGroupPython] Ne_element001  label="Ne_element : 1"  # scripted group (container) (typed FeaturePython)
  n = 1
  ref = Ne_element
FEATURE [App::DocumentObjectGroupPython] G4_Ne  # scripted group (container) (typed FeaturePython)
  Dunit = g/cm3
  Dvalue = 0.000838505
  Group = -> [Ne_element001]
  conduct = 2
  density = 1
  expand = 3
  formula = Ne
  name = G4_Ne
  specific = 4
FEATURE [App::DocumentObjectGroupPython] Na_element020  label="Na_element : 005"  # scripted group (container) (typed FeaturePython)
  n = 1
  ref = Na_element
FEATURE [App::DocumentObjectGroupPython] G4_Na  # scripted group (container) (typed FeaturePython)
  Dunit = g/cm3
  Dvalue = 0.971
  Group = -> [Na_element020]
  conduct = 2
  density = 1
  expand = 3
  formula = Na
  name = G4_Na
  specific = 4
FEATURE [App::DocumentObjectGroupPython] Mg_element011  label="Mg_element : 005"  # scripted group (container) (typed FeaturePython)
  n = 1
  ref = Mg_element
FEATURE [App::DocumentObjectGroupPython] G4_Mg  # scripted group (container) (typed FeaturePython)
  Dunit = g/cm3
  Dvalue = 1.74
  Group = -> [Mg_element011]
  conduct = 2
  density = 1
  expand = 3
  formula = Mg
  name = G4_Mg
  specific = 4
FEATURE [App::DocumentObjectGroupPython] Al_element004  label="Al_element : 1"  # scripted group (container) (typed FeaturePython)
  n = 1
  ref = Al_element
FEATURE [App::DocumentObjectGroupPython] G4_Al  # scripted group (container) (typed FeaturePython)
  Dunit = g/cm3
  Dvalue = 2.699
  Group = -> [Al_element004]
  conduct = 2
  density = 1
  expand = 3
  formula = Al
  name = G4_Al
  specific = 4
FEATURE [App::DocumentObjectGroupPython] Si_element007  label="Si_element : 002"  # scripted group (container) (typed FeaturePython)
  n = 1
  ref = Si_element
FEATURE [App::DocumentObjectGroupPython] G4_Si  # scripted group (container) (typed FeaturePython)
  Dunit = g/cm3
  Dvalue = 2.33
  Group = -> [Si_element007]
  conduct = 2
  density = 1
  expand = 3
  formula = Si
  name = G4_Si
  specific = 4
FEATURE [App::DocumentObjectGroupPython] P_element013  label="P_element : 002"  # scripted group (container) (typed FeaturePython)
  n = 1
  ref = P_element
FEATURE [App::DocumentObjectGroupPython] G4_P  # scripted group (container) (typed FeaturePython)
  Dunit = g/cm3
  Dvalue = 2.2
  Group = -> [P_element013]
  conduct = 2
  density = 1
  expand = 3
  formula = P
  name = G4_P
  specific = 4
FEATURE [App::DocumentObjectGroupPython] S_element023  label="S_element : 007"  # scripted group (container) (typed FeaturePython)
  n = 1
  ref = S_element
FEATURE [App::DocumentObjectGroupPython] G4_S  # scripted group (container) (typed FeaturePython)
  Dunit = g/cm3
  Dvalue = 2
  Group = -> [S_element023]
  conduct = 2
  density = 1
  expand = 3
  formula = S
  name = G4_S
  specific = 4
FEATURE [App::DocumentObjectGroupPython] Cl_element029  label="Cl_element : 015"  # scripted group (container) (typed FeaturePython)
  n = 1
  ref = Cl_element
FEATURE [App::DocumentObjectGroupPython] G4_Cl  # scripted group (container) (typed FeaturePython)
  Dunit = g/cm3
  Dvalue = 0.00299473
  Group = -> [Cl_element029]
  conduct = 2
  density = 1
  expand = 3
  formula = Cl
  name = G4_Cl
  specific = 4
FEATURE [App::DocumentObjectGroupPython] Ar_element002  label="Ar_element : 1"  # scripted group (container) (typed FeaturePython)
  n = 1
  ref = Ar_element
FEATURE [App::DocumentObjectGroupPython] G4_Ar  # scripted group (container) (typed FeaturePython)
  Dunit = g/cm3
  Dvalue = 0.00166201
  Group = -> [Ar_element002]
  conduct = 2
  density = 1
  expand = 3
  formula = Ar
  name = G4_Ar
  specific = 4
FEATURE [App::DocumentObjectGroupPython] K_element013  label="K_element : 003"  # scripted group (container) (typed FeaturePython)
  n = 1
  ref = K_element
FEATURE [App::DocumentObjectGroupPython] G4_K  # scripted group (container) (typed FeaturePython)
  Dunit = g/cm3
  Dvalue = 0.862
  Group = -> [K_element013]
  conduct = 2
  density = 1
  expand = 3
  formula = K
  name = G4_K
  specific = 4
FEATURE [App::DocumentObjectGroupPython] Ca_element014  label="Ca_element : 007"  # scripted group (container) (typed FeaturePython)
  n = 1
  ref = Ca_element
FEATURE [App::DocumentObjectGroupPython] G4_Ca  # scripted group (container) (typed FeaturePython)
  Dunit = g/cm3
  Dvalue = 1.55
  Group = -> [Ca_element014]
  conduct = 2
  density = 1
  expand = 3
  formula = Ca
  name = G4_Ca
  specific = 4
FEATURE [App::DocumentObjectGroupPython] Sc_element001  label="Sc_element : 1"  # scripted group (container) (typed FeaturePython)
  n = 1
  ref = Sc_element
FEATURE [App::DocumentObjectGroupPython] G4_Sc  # scripted group (container) (typed FeaturePython)
  Dunit = g/cm3
  Dvalue = 2.989
  Group = -> [Sc_element001]
  conduct = 2
  density = 1
  expand = 3
  formula = Sc
  name = G4_Sc
  specific = 4
FEATURE [App::DocumentObjectGroupPython] Ti_element004  label="Ti_element : 002"  # scripted group (container) (typed FeaturePython)
  n = 1
  ref = Ti_element
FEATURE [App::DocumentObjectGroupPython] G4_Ti  # scripted group (container) (typed FeaturePython)
  Dunit = g/cm3
  Dvalue = 4.54
  Group = -> [Ti_element004]
  conduct = 2
  density = 1
  expand = 3
  formula = Ti
  name = G4_Ti
  specific = 4
FEATURE [App::DocumentObjectGroupPython] V_element001  label="V_element : 1"  # scripted group (container) (typed FeaturePython)
  n = 1
  ref = V_element
FEATURE [App::DocumentObjectGroupPython] G4_V  # scripted group (container) (typed FeaturePython)
  Dunit = g/cm3
  Dvalue = 6.11
  Group = -> [V_element001]
  conduct = 2
  density = 1
  expand = 3
  formula = V
  name = G4_V
  specific = 4
FEATURE [App::DocumentObjectGroupPython] Cr_element001  label="Cr_element : 1"  # scripted group (container) (typed FeaturePython)
  n = 1
  ref = Cr_element
FEATURE [App::DocumentObjectGroupPython] G4_Cr  # scripted group (container) (typed FeaturePython)
  Dunit = g/cm3
  Dvalue = 7.18
  Group = -> [Cr_element001]
  conduct = 2
  density = 1
  expand = 3
  formula = Cr
  name = G4_Cr
  specific = 4
FEATURE [App::DocumentObjectGroupPython] Mn_element001  label="Mn_element : 1"  # scripted group (container) (typed FeaturePython)
  n = 1
  ref = Mn_element
FEATURE [App::DocumentObjectGroupPython] G4_Mn  # scripted group (container) (typed FeaturePython)
  Dunit = g/cm3
  Dvalue = 7.44
  Group = -> [Mn_element001]
  conduct = 2
  density = 1
  expand = 3
  formula = Mn
  name = G4_Mn
  specific = 4
FEATURE [App::DocumentObjectGroupPython] Fe_element007  label="Fe_element : 004"  # scripted group (container) (typed FeaturePython)
  n = 1
  ref = Fe_element
FEATURE [App::DocumentObjectGroupPython] G4_Fe  # scripted group (container) (typed FeaturePython)
  Dunit = g/cm3
  Dvalue = 7.874
  Group = -> [Fe_element007]
  conduct = 2
  density = 1
  expand = 3
  formula = Fe
  name = G4_Fe
  specific = 4
FEATURE [App::DocumentObjectGroupPython] Co_element001  label="Co_element : 1"  # scripted group (container) (typed FeaturePython)
  n = 1
  ref = Co_element
FEATURE [App::DocumentObjectGroupPython] G4_Co  # scripted group (container) (typed FeaturePython)
  Dunit = g/cm3
  Dvalue = 8.9
  Group = -> [Co_element001]
  conduct = 2
  density = 1
  expand = 3
  formula = Co
  name = G4_Co
  specific = 4
FEATURE [App::DocumentObjectGroupPython] Ni_element001  label="Ni_element : 1"  # scripted group (container) (typed FeaturePython)
  n = 1
  ref = Ni_element
FEATURE [App::DocumentObjectGroupPython] G4_Ni  # scripted group (container) (typed FeaturePython)
  Dunit = g/cm3
  Dvalue = 8.902
  Group = -> [Ni_element001]
  conduct = 2
  density = 1
  expand = 3
  formula = Ni
  name = G4_Ni
  specific = 4
FEATURE [App::DocumentObjectGroupPython] Cu_element001  label="Cu_element : 1"  # scripted group (container) (typed FeaturePython)
  n = 1
  ref = Cu_element
FEATURE [App::DocumentObjectGroupPython] G4_Cu  # scripted group (container) (typed FeaturePython)
  Dunit = g/cm3
  Dvalue = 8.96
  Group = -> [Cu_element001]
  conduct = 2
  density = 1
  expand = 3
  formula = Cu
  name = G4_Cu
  specific = 4
FEATURE [App::DocumentObjectGroupPython] Zn_element001  label="Zn_element : 1"  # scripted group (container) (typed FeaturePython)
  n = 1
  ref = Zn_element
FEATURE [App::DocumentObjectGroupPython] G4_Zn  # scripted group (container) (typed FeaturePython)
  Dunit = g/cm3
  Dvalue = 7.133
  Group = -> [Zn_element001]
  conduct = 2
  density = 1
  expand = 3
  formula = Zn
  name = G4_Zn
  specific = 4
FEATURE [App::DocumentObjectGroupPython] Ga_element002  label="Ga_element : 002"  # scripted group (container) (typed FeaturePython)
  n = 1
  ref = Ga_element
FEATURE [App::DocumentObjectGroupPython] G4_Ga  # scripted group (container) (typed FeaturePython)
  Dunit = g/cm3
  Dvalue = 5.904
  Group = -> [Ga_element002]
  conduct = 2
  density = 1
  expand = 3
  formula = Ga
  name = G4_Ga
  specific = 4
FEATURE [App::DocumentObjectGroupPython] Ge_element002  label="Ge_element : 1"  # scripted group (container) (typed FeaturePython)
  n = 1
  ref = Ge_element
FEATURE [App::DocumentObjectGroupPython] G4_Ge  # scripted group (container) (typed FeaturePython)
  Dunit = g/cm3
  Dvalue = 5.323
  Group = -> [Ge_element002]
  conduct = 2
  density = 1
  expand = 3
  formula = Ge
  name = G4_Ge
  specific = 4
FEATURE [App::DocumentObjectGroupPython] As_element003  label="As_element : 002"  # scripted group (container) (typed FeaturePython)
  n = 1
  ref = As_element
FEATURE [App::DocumentObjectGroupPython] G4_As  # scripted group (container) (typed FeaturePython)
  Dunit = g/cm3
  Dvalue = 5.73
  Group = -> [As_element003]
  conduct = 2
  density = 1
  expand = 3
  formula = As
  name = G4_As
  specific = 4
FEATURE [App::DocumentObjectGroupPython] Se_element001  label="Se_element : 1"  # scripted group (container) (typed FeaturePython)
  n = 1
  ref = Se_element
FEATURE [App::DocumentObjectGroupPython] G4_Se  # scripted group (container) (typed FeaturePython)
  Dunit = g/cm3
  Dvalue = 4.5
  Group = -> [Se_element001]
  conduct = 2
  density = 1
  expand = 3
  formula = Se
  name = G4_Se
  specific = 4
FEATURE [App::DocumentObjectGroupPython] Br_element007  label="Br_element : 004"  # scripted group (container) (typed FeaturePython)
  n = 1
  ref = Br_element
FEATURE [App::DocumentObjectGroupPython] G4_Br  # scripted group (container) (typed FeaturePython)
  Dunit = g/cm3
  Dvalue = 0.0070721
  Group = -> [Br_element007]
  conduct = 2
  density = 1
  expand = 3
  formula = Br
  name = G4_Br
  specific = 4
FEATURE [App::DocumentObjectGroupPython] Kr_element001  label="Kr_element : 1"  # scripted group (container) (typed FeaturePython)
  n = 1
  ref = Kr_element
FEATURE [App::DocumentObjectGroupPython] G4_Kr  # scripted group (container) (typed FeaturePython)
  Dunit = g/cm3
  Dvalue = 0.00347832
  Group = -> [Kr_element001]
  conduct = 2
  density = 1
  expand = 3
  formula = Kr
  name = G4_Kr
  specific = 4
FEATURE [App::DocumentObjectGroupPython] Rb_element001  label="Rb_element : 1"  # scripted group (container) (typed FeaturePython)
  n = 1
  ref = Rb_element
FEATURE [App::DocumentObjectGroupPython] G4_Rb  # scripted group (container) (typed FeaturePython)
  Dunit = g/cm3
  Dvalue = 1.532
  Group = -> [Rb_element001]
  conduct = 2
  density = 1
  expand = 3
  formula = Rb
  name = G4_Rb
  specific = 4
FEATURE [App::DocumentObjectGroupPython] Sr_element001  label="Sr_element : 1"  # scripted group (container) (typed FeaturePython)
  n = 1
  ref = Sr_element
FEATURE [App::DocumentObjectGroupPython] G4_Sr  # scripted group (container) (typed FeaturePython)
  Dunit = g/cm3
  Dvalue = 2.54
  Group = -> [Sr_element001]
  conduct = 2
  density = 1
  expand = 3
  formula = Sr
  name = G4_Sr
  specific = 4
FEATURE [App::DocumentObjectGroupPython] Y_element001  label="Y_element : 1"  # scripted group (container) (typed FeaturePython)
  n = 1
  ref = Y_element
FEATURE [App::DocumentObjectGroupPython] G4_Y  # scripted group (container) (typed FeaturePython)
  Dunit = g/cm3
  Dvalue = 4.469
  Group = -> [Y_element001]
  conduct = 2
  density = 1
  expand = 3
  formula = Y
  name = G4_Y
  specific = 4
FEATURE [App::DocumentObjectGroupPython] Zr_element001  label="Zr_element : 1"  # scripted group (container) (typed FeaturePython)
  n = 1
  ref = Zr_element
FEATURE [App::DocumentObjectGroupPython] G4_Zr  # scripted group (container) (typed FeaturePython)
  Dunit = g/cm3
  Dvalue = 6.506
  Group = -> [Zr_element001]
  conduct = 2
  density = 1
  expand = 3
  formula = Zr
  name = G4_Zr
  specific = 4
FEATURE [App::DocumentObjectGroupPython] Nb_element001  label="Nb_element : 1"  # scripted group (container) (typed FeaturePython)
  n = 1
  ref = Nb_element
FEATURE [App::DocumentObjectGroupPython] G4_Nb  # scripted group (container) (typed FeaturePython)
  Dunit = g/cm3
  Dvalue = 8.57
  Group = -> [Nb_element001]
  conduct = 2
  density = 1
  expand = 3
  formula = Nb
  name = G4_Nb
  specific = 4
FEATURE [App::DocumentObjectGroupPython] Mo_element001  label="Mo_element : 1"  # scripted group (container) (typed FeaturePython)
  n = 1
  ref = Mo_element
FEATURE [App::DocumentObjectGroupPython] G4_Mo  # scripted group (container) (typed FeaturePython)
  Dunit = g/cm3
  Dvalue = 10.22
  Group = -> [Mo_element001]
  conduct = 2
  density = 1
  expand = 3
  formula = Mo
  name = G4_Mo
  specific = 4
FEATURE [App::DocumentObjectGroupPython] Tc_element001  label="Tc_element : 1"  # scripted group (container) (typed FeaturePython)
  n = 1
  ref = Tc_element
FEATURE [App::DocumentObjectGroupPython] G4_Tc  # scripted group (container) (typed FeaturePython)
  Dunit = g/cm3
  Dvalue = 11.5
  Group = -> [Tc_element001]
  conduct = 2
  density = 1
  expand = 3
  formula = Tc
  name = G4_Tc
  specific = 4
FEATURE [App::DocumentObjectGroupPython] Ru_element001  label="Ru_element : 1"  # scripted group (container) (typed FeaturePython)
  n = 1
  ref = Ru_element
FEATURE [App::DocumentObjectGroupPython] G4_Ru  # scripted group (container) (typed FeaturePython)
  Dunit = g/cm3
  Dvalue = 12.41
  Group = -> [Ru_element001]
  conduct = 2
  density = 1
  expand = 3
  formula = Ru
  name = G4_Ru
  specific = 4
FEATURE [App::DocumentObjectGroupPython] Rh_element001  label="Rh_element : 1"  # scripted group (container) (typed FeaturePython)
  n = 1
  ref = Rh_element
FEATURE [App::DocumentObjectGroupPython] G4_Rh  # scripted group (container) (typed FeaturePython)
  Dunit = g/cm3
  Dvalue = 12.41
  Group = -> [Rh_element001]
  conduct = 2
  density = 1
  expand = 3
  formula = Rh
  name = G4_Rh
  specific = 4
FEATURE [App::DocumentObjectGroupPython] Pd_element001  label="Pd_element : 1"  # scripted group (container) (typed FeaturePython)
  n = 1
  ref = Pd_element
FEATURE [App::DocumentObjectGroupPython] G4_Pd  # scripted group (container) (typed FeaturePython)
  Dunit = g/cm3
  Dvalue = 12.02
  Group = -> [Pd_element001]
  conduct = 2
  density = 1
  expand = 3
  formula = Pd
  name = G4_Pd
  specific = 4
FEATURE [App::DocumentObjectGroupPython] Ag_element006  label="Ag_element : 004"  # scripted group (container) (typed FeaturePython)
  n = 1
  ref = Ag_element
FEATURE [App::DocumentObjectGroupPython] G4_Ag  # scripted group (container) (typed FeaturePython)
  Dunit = g/cm3
  Dvalue = 10.5
  Group = -> [Ag_element006]
  conduct = 2
  density = 1
  expand = 3
  formula = Ag
  name = G4_Ag
  specific = 4
FEATURE [App::DocumentObjectGroupPython] Cd_element003  label="Cd_element : 003"  # scripted group (container) (typed FeaturePython)
  n = 1
  ref = Cd_element
FEATURE [App::DocumentObjectGroupPython] G4_Cd  # scripted group (container) (typed FeaturePython)
  Dunit = g/cm3
  Dvalue = 8.65
  Group = -> [Cd_element003]
  conduct = 2
  density = 1
  expand = 3
  formula = Cd
  name = G4_Cd
  specific = 4
FEATURE [App::DocumentObjectGroupPython] In_element001  label="In_element : 1"  # scripted group (container) (typed FeaturePython)
  n = 1
  ref = In_element
FEATURE [App::DocumentObjectGroupPython] G4_In  # scripted group (container) (typed FeaturePython)
  Dunit = g/cm3
  Dvalue = 7.31
  Group = -> [In_element001]
  conduct = 2
  density = 1
  expand = 3
  formula = In
  name = G4_In
  specific = 4
FEATURE [App::DocumentObjectGroupPython] Sn_element001  label="Sn_element : 1"  # scripted group (container) (typed FeaturePython)
  n = 1
  ref = Sn_element
FEATURE [App::DocumentObjectGroupPython] G4_Sn  # scripted group (container) (typed FeaturePython)
  Dunit = g/cm3
  Dvalue = 7.31
  Group = -> [Sn_element001]
  conduct = 2
  density = 1
  expand = 3
  formula = Sn
  name = G4_Sn
  specific = 4
FEATURE [App::DocumentObjectGroupPython] Sb_element001  label="Sb_element : 1"  # scripted group (container) (typed FeaturePython)
  n = 1
  ref = Sb_element
FEATURE [App::DocumentObjectGroupPython] G4_Sb  # scripted group (container) (typed FeaturePython)
  Dunit = g/cm3
  Dvalue = 6.691
  Group = -> [Sb_element001]
  conduct = 2
  density = 1
  expand = 3
  formula = Sb
  name = G4_Sb
  specific = 4
FEATURE [App::DocumentObjectGroupPython] Te_element002  label="Te_element : 002"  # scripted group (container) (typed FeaturePython)
  n = 1
  ref = Te_element
FEATURE [App::DocumentObjectGroupPython] G4_Te  # scripted group (container) (typed FeaturePython)
  Dunit = g/cm3
  Dvalue = 6.24
  Group = -> [Te_element002]
  conduct = 2
  density = 1
  expand = 3
  formula = Te
  name = G4_Te
  specific = 4
FEATURE [App::DocumentObjectGroupPython] I_element010  label="I_element : 006"  # scripted group (container) (typed FeaturePython)
  n = 1
  ref = I_element
FEATURE [App::DocumentObjectGroupPython] G4_I  # scripted group (container) (typed FeaturePython)
  Dunit = g/cm3
  Dvalue = 4.93
  Group = -> [I_element010]
  conduct = 2
  density = 1
  expand = 3
  formula = I
  name = G4_I
  specific = 4
FEATURE [App::DocumentObjectGroupPython] Xe_element001  label="Xe_element : 1"  # scripted group (container) (typed FeaturePython)
  n = 1
  ref = Xe_element
FEATURE [App::DocumentObjectGroupPython] G4_Xe  # scripted group (container) (typed FeaturePython)
  Dunit = g/cm3
  Dvalue = 0.00548536
  Group = -> [Xe_element001]
  conduct = 2
  density = 1
  expand = 3
  formula = Xe
  name = G4_Xe
  specific = 4
FEATURE [App::DocumentObjectGroupPython] Cs_element003  label="Cs_element : 003"  # scripted group (container) (typed FeaturePython)
  n = 1
  ref = Cs_element
FEATURE [App::DocumentObjectGroupPython] G4_Cs  # scripted group (container) (typed FeaturePython)
  Dunit = g/cm3
  Dvalue = 1.873
  Group = -> [Cs_element003]
  conduct = 2
  density = 1
  expand = 3
  formula = Cs
  name = G4_Cs
  specific = 4
FEATURE [App::DocumentObjectGroupPython] Ba_element003  label="Ba_element : 003"  # scripted group (container) (typed FeaturePython)
  n = 1
  ref = Ba_element
FEATURE [App::DocumentObjectGroupPython] G4_Ba  # scripted group (container) (typed FeaturePython)
  Dunit = g/cm3
  Dvalue = 3.5
  Group = -> [Ba_element003]
  conduct = 2
  density = 1
  expand = 3
  formula = Ba
  name = G4_Ba
  specific = 4
FEATURE [App::DocumentObjectGroupPython] La_element003  label="La_element : 003"  # scripted group (container) (typed FeaturePython)
  n = 1
  ref = La_element
FEATURE [App::DocumentObjectGroupPython] G4_La  # scripted group (container) (typed FeaturePython)
  Dunit = g/cm3
  Dvalue = 6.154
  Group = -> [La_element003]
  conduct = 2
  density = 1
  expand = 3
  formula = La
  name = G4_La
  specific = 4
FEATURE [App::DocumentObjectGroupPython] Ce_element002  label="Ce_element : 1"  # scripted group (container) (typed FeaturePython)
  n = 1
  ref = Ce_element
FEATURE [App::DocumentObjectGroupPython] G4_Ce  # scripted group (container) (typed FeaturePython)
  Dunit = g/cm3
  Dvalue = 6.657
  Group = -> [Ce_element002]
  conduct = 2
  density = 1
  expand = 3
  formula = Ce
  name = G4_Ce
  specific = 4
FEATURE [App::DocumentObjectGroupPython] Pr_element001  label="Pr_element : 1"  # scripted group (container) (typed FeaturePython)
  n = 1
  ref = Pr_element
FEATURE [App::DocumentObjectGroupPython] G4_Pr  # scripted group (container) (typed FeaturePython)
  Dunit = g/cm3
  Dvalue = 6.71
  Group = -> [Pr_element001]
  conduct = 2
  density = 1
  expand = 3
  formula = Pr
  name = G4_Pr
  specific = 4
FEATURE [App::DocumentObjectGroupPython] Nd_element001  label="Nd_element : 1"  # scripted group (container) (typed FeaturePython)
  n = 1
  ref = Nd_element
FEATURE [App::DocumentObjectGroupPython] G4_Nd  # scripted group (container) (typed FeaturePython)
  Dunit = g/cm3
  Dvalue = 6.9
  Group = -> [Nd_element001]
  conduct = 2
  density = 1
  expand = 3
  formula = Nd
  name = G4_Nd
  specific = 4
FEATURE [App::DocumentObjectGroupPython] Pm_element001  label="Pm_element : 1"  # scripted group (container) (typed FeaturePython)
  n = 1
  ref = Pm_element
FEATURE [App::DocumentObjectGroupPython] G4_Pm  # scripted group (container) (typed FeaturePython)
  Dunit = g/cm3
  Dvalue = 7.22
  Group = -> [Pm_element001]
  conduct = 2
  density = 1
  expand = 3
  formula = Pm
  name = G4_Pm
  specific = 4
FEATURE [App::DocumentObjectGroupPython] Sm_element001  label="Sm_element : 1"  # scripted group (container) (typed FeaturePython)
  n = 1
  ref = Sm_element
FEATURE [App::DocumentObjectGroupPython] G4_Sm  # scripted group (container) (typed FeaturePython)
  Dunit = g/cm3
  Dvalue = 7.46
  Group = -> [Sm_element001]
  conduct = 2
  density = 1
  expand = 3
  formula = Sm
  name = G4_Sm
  specific = 4
FEATURE [App::DocumentObjectGroupPython] Eu_element001  label="Eu_element : 1"  # scripted group (container) (typed FeaturePython)
  n = 1
  ref = Eu_element
FEATURE [App::DocumentObjectGroupPython] G4_Eu  # scripted group (container) (typed FeaturePython)
  Dunit = g/cm3
  Dvalue = 5.243
  Group = -> [Eu_element001]
  conduct = 2
  density = 1
  expand = 3
  formula = Eu
  name = G4_Eu
  specific = 4
FEATURE [App::DocumentObjectGroupPython] Gd_element002  label="Gd_element : 1"  # scripted group (container) (typed FeaturePython)
  n = 1
  ref = Gd_element
FEATURE [App::DocumentObjectGroupPython] G4_Gd  # scripted group (container) (typed FeaturePython)
  Dunit = g/cm3
  Dvalue = 7.9004
  Group = -> [Gd_element002]
  conduct = 2
  density = 1
  expand = 3
  formula = Gd
  name = G4_Gd
  specific = 4
FEATURE [App::DocumentObjectGroupPython] Tb_element001  label="Tb_element : 1"  # scripted group (container) (typed FeaturePython)
  n = 1
  ref = Tb_element
FEATURE [App::DocumentObjectGroupPython] G4_Tb  # scripted group (container) (typed FeaturePython)
  Dunit = g/cm3
  Dvalue = 8.229
  Group = -> [Tb_element001]
  conduct = 2
  density = 1
  expand = 3
  formula = Tb
  name = G4_Tb
  specific = 4
FEATURE [App::DocumentObjectGroupPython] Dy_element001  label="Dy_element : 1"  # scripted group (container) (typed FeaturePython)
  n = 1
  ref = Dy_element
FEATURE [App::DocumentObjectGroupPython] G4_Dy  # scripted group (container) (typed FeaturePython)
  Dunit = g/cm3
  Dvalue = 8.55
  Group = -> [Dy_element001]
  conduct = 2
  density = 1
  expand = 3
  formula = Dy
  name = G4_Dy
  specific = 4
FEATURE [App::DocumentObjectGroupPython] Ho_element001  label="Ho_element : 1"  # scripted group (container) (typed FeaturePython)
  n = 1
  ref = Ho_element
FEATURE [App::DocumentObjectGroupPython] G4_Ho  # scripted group (container) (typed FeaturePython)
  Dunit = g/cm3
  Dvalue = 8.795
  Group = -> [Ho_element001]
  conduct = 2
  density = 1
  expand = 3
  formula = Ho
  name = G4_Ho
  specific = 4
FEATURE [App::DocumentObjectGroupPython] Er_element001  label="Er_element : 1"  # scripted group (container) (typed FeaturePython)
  n = 1
  ref = Er_element
FEATURE [App::DocumentObjectGroupPython] G4_Er  # scripted group (container) (typed FeaturePython)
  Dunit = g/cm3
  Dvalue = 9.066
  Group = -> [Er_element001]
  conduct = 2
  density = 1
  expand = 3
  formula = Er
  name = G4_Er
  specific = 4
FEATURE [App::DocumentObjectGroupPython] Tm_element001  label="Tm_element : 1"  # scripted group (container) (typed FeaturePython)
  n = 1
  ref = Tm_element
FEATURE [App::DocumentObjectGroupPython] G4_Tm  # scripted group (container) (typed FeaturePython)
  Dunit = g/cm3
  Dvalue = 9.321
  Group = -> [Tm_element001]
  conduct = 2
  density = 1
  expand = 3
  formula = Tm
  name = G4_Tm
  specific = 4
FEATURE [App::DocumentObjectGroupPython] Yb_element001  label="Yb_element : 1"  # scripted group (container) (typed FeaturePython)
  n = 1
  ref = Yb_element
FEATURE [App::DocumentObjectGroupPython] G4_Yb  # scripted group (container) (typed FeaturePython)
  Dunit = g/cm3
  Dvalue = 6.73
  Group = -> [Yb_element001]
  conduct = 2
  density = 1
  expand = 3
  formula = Yb
  name = G4_Yb
  specific = 4
FEATURE [App::DocumentObjectGroupPython] Lu_element001  label="Lu_element : 1"  # scripted group (container) (typed FeaturePython)
  n = 1
  ref = Lu_element
FEATURE [App::DocumentObjectGroupPython] G4_Lu  # scripted group (container) (typed FeaturePython)
  Dunit = g/cm3
  Dvalue = 9.84
  Group = -> [Lu_element001]
  conduct = 2
  density = 1
  expand = 3
  formula = Lu
  name = G4_Lu
  specific = 4
FEATURE [App::DocumentObjectGroupPython] Hf_element001  label="Hf_element : 1"  # scripted group (container) (typed FeaturePython)
  n = 1
  ref = Hf_element
FEATURE [App::DocumentObjectGroupPython] G4_Hf  # scripted group (container) (typed FeaturePython)
  Dunit = g/cm3
  Dvalue = 13.31
  Group = -> [Hf_element001]
  conduct = 2
  density = 1
  expand = 3
  formula = Hf
  name = G4_Hf
  specific = 4
FEATURE [App::DocumentObjectGroupPython] Ta_element001  label="Ta_element : 1"  # scripted group (container) (typed FeaturePython)
  n = 1
  ref = Ta_element
FEATURE [App::DocumentObjectGroupPython] G4_Ta  # scripted group (container) (typed FeaturePython)
  Dunit = g/cm3
  Dvalue = 16.654
  Group = -> [Ta_element001]
  conduct = 2
  density = 1
  expand = 3
  formula = Ta
  name = G4_Ta
  specific = 4
FEATURE [App::DocumentObjectGroupPython] W_element004  label="W_element : 004"  # scripted group (container) (typed FeaturePython)
  n = 1
  ref = W_element
FEATURE [App::DocumentObjectGroupPython] G4_W  # scripted group (container) (typed FeaturePython)
  Dunit = g/cm3
  Dvalue = 19.3
  Group = -> [W_element004]
  conduct = 2
  density = 1
  expand = 3
  formula = W
  name = G4_W
  specific = 4
FEATURE [App::DocumentObjectGroupPython] Re_element001  label="Re_element : 1"  # scripted group (container) (typed FeaturePython)
  n = 1
  ref = Re_element
FEATURE [App::DocumentObjectGroupPython] G4_Re  # scripted group (container) (typed FeaturePython)
  Dunit = g/cm3
  Dvalue = 21.02
  Group = -> [Re_element001]
  conduct = 2
  density = 1
  expand = 3
  formula = Re
  name = G4_Re
  specific = 4
FEATURE [App::DocumentObjectGroupPython] Os_element001  label="Os_element : 1"  # scripted group (container) (typed FeaturePython)
  n = 1
  ref = Os_element
FEATURE [App::DocumentObjectGroupPython] G4_Os  # scripted group (container) (typed FeaturePython)
  Dunit = g/cm3
  Dvalue = 22.57
  Group = -> [Os_element001]
  conduct = 2
  density = 1
  expand = 3
  formula = Os
  name = G4_Os
  specific = 4
FEATURE [App::DocumentObjectGroupPython] Ir_element001  label="Ir_element : 1"  # scripted group (container) (typed FeaturePython)
  n = 1
  ref = Ir_element
FEATURE [App::DocumentObjectGroupPython] G4_Ir  # scripted group (container) (typed FeaturePython)
  Dunit = g/cm3
  Dvalue = 22.42
  Group = -> [Ir_element001]
  conduct = 2
  density = 1
  expand = 3
  formula = Ir
  name = G4_Ir
  specific = 4
FEATURE [App::DocumentObjectGroupPython] Pt_element001  label="Pt_element : 1"  # scripted group (container) (typed FeaturePython)
  n = 1
  ref = Pt_element
FEATURE [App::DocumentObjectGroupPython] G4_Pt  # scripted group (container) (typed FeaturePython)
  Dunit = g/cm3
  Dvalue = 21.45
  Group = -> [Pt_element001]
  conduct = 2
  density = 1
  expand = 3
  formula = Pt
  name = G4_Pt
  specific = 4
FEATURE [App::DocumentObjectGroupPython] Au_element001  label="Au_element : 1"  # scripted group (container) (typed FeaturePython)
  n = 1
  ref = Au_element
FEATURE [App::DocumentObjectGroupPython] G4_Au  # scripted group (container) (typed FeaturePython)
  Dunit = g/cm3
  Dvalue = 19.32
  Group = -> [Au_element001]
  conduct = 2
  density = 1
  expand = 3
  formula = Au
  name = G4_Au
  specific = 4
FEATURE [App::DocumentObjectGroupPython] Hg_element002  label="Hg_element : 002"  # scripted group (container) (typed FeaturePython)
  n = 1
  ref = Hg_element
FEATURE [App::DocumentObjectGroupPython] G4_Hg  # scripted group (container) (typed FeaturePython)
  Dunit = g/cm3
  Dvalue = 13.546
  Group = -> [Hg_element002]
  conduct = 2
  density = 1
  expand = 3
  formula = Hg
  name = G4_Hg
  specific = 4
FEATURE [App::DocumentObjectGroupPython] Tl_element002  label="Tl_element : 002"  # scripted group (container) (typed FeaturePython)
  n = 1
  ref = Tl_element
FEATURE [App::DocumentObjectGroupPython] G4_Tl  # scripted group (container) (typed FeaturePython)
  Dunit = g/cm3
  Dvalue = 11.72
  Group = -> [Tl_element002]
  conduct = 2
  density = 1
  expand = 3
  formula = Tl
  name = G4_Tl
  specific = 4
FEATURE [App::DocumentObjectGroupPython] Pb_element003  label="Pb_element : 1"  # scripted group (container) (typed FeaturePython)
  n = 1
  ref = Pb_element
FEATURE [App::DocumentObjectGroupPython] G4_Pb  # scripted group (container) (typed FeaturePython)
  Dunit = g/cm3
  Dvalue = 11.35
  Group = -> [Pb_element003]
  conduct = 2
  density = 1
  expand = 3
  formula = Pb
  name = G4_Pb
  specific = 4
FEATURE [App::DocumentObjectGroupPython] Bi_element002  label="Bi_element : 1"  # scripted group (container) (typed FeaturePython)
  n = 1
  ref = Bi_element
FEATURE [App::DocumentObjectGroupPython] G4_Bi  # scripted group (container) (typed FeaturePython)
  Dunit = g/cm3
  Dvalue = 9.747
  Group = -> [Bi_element002]
  conduct = 2
  density = 1
  expand = 3
  formula = Bi
  name = G4_Bi
  specific = 4
FEATURE [App::DocumentObjectGroupPython] Po_element001  label="Po_element : 1"  # scripted group (container) (typed FeaturePython)
  n = 1
  ref = Po_element
FEATURE [App::DocumentObjectGroupPython] G4_Po  # scripted group (container) (typed FeaturePython)
  Dunit = g/cm3
  Dvalue = 9.32
  Group = -> [Po_element001]
  conduct = 2
  density = 1
  expand = 3
  formula = Po
  name = G4_Po
  specific = 4
FEATURE [App::DocumentObjectGroupPython] At_element001  label="At_element : 1"  # scripted group (container) (typed FeaturePython)
  n = 1
  ref = At_element
FEATURE [App::DocumentObjectGroupPython] G4_At  # scripted group (container) (typed FeaturePython)
  Dunit = g/cm3
  Dvalue = 9.32
  Group = -> [At_element001]
  conduct = 2
  density = 1
  expand = 3
  formula = At
  name = G4_At
  specific = 4
FEATURE [App::DocumentObjectGroupPython] Rn_element001  label="Rn_element : 1"  # scripted group (container) (typed FeaturePython)
  n = 1
  ref = Rn_element
FEATURE [App::DocumentObjectGroupPython] G4_Rn  # scripted group (container) (typed FeaturePython)
  Dunit = g/cm3
  Dvalue = 0.00900662
  Group = -> [Rn_element001]
  conduct = 2
  density = 1
  expand = 3
  formula = Rn
  name = G4_Rn
  specific = 4
FEATURE [App::DocumentObjectGroupPython] Fr_element001  label="Fr_element : 1"  # scripted group (container) (typed FeaturePython)
  n = 1
  ref = Fr_element
FEATURE [App::DocumentObjectGroupPython] G4_Fr  # scripted group (container) (typed FeaturePython)
  Dunit = g/cm3
  Dvalue = 1
  Group = -> [Fr_element001]
  conduct = 2
  density = 1
  expand = 3
  formula = Fr
  name = G4_Fr
  specific = 4
FEATURE [App::DocumentObjectGroupPython] Ra_element001  label="Ra_element : 1"  # scripted group (container) (typed FeaturePython)
  n = 1
  ref = Ra_element
FEATURE [App::DocumentObjectGroupPython] G4_Ra  # scripted group (container) (typed FeaturePython)
  Dunit = g/cm3
  Dvalue = 5
  Group = -> [Ra_element001]
  conduct = 2
  density = 1
  expand = 3
  formula = Ra
  name = G4_Ra
  specific = 4
FEATURE [App::DocumentObjectGroupPython] Ac_element001  label="Ac_element : 1"  # scripted group (container) (typed FeaturePython)
  n = 1
  ref = Ac_element
FEATURE [App::DocumentObjectGroupPython] G4_Ac  # scripted group (container) (typed FeaturePython)
  Dunit = g/cm3
  Dvalue = 10.07
  Group = -> [Ac_element001]
  conduct = 2
  density = 1
  expand = 3
  formula = Ac
  name = G4_Ac
  specific = 4
FEATURE [App::DocumentObjectGroupPython] Th_element001  label="Th_element : 1"  # scripted group (container) (typed FeaturePython)
  n = 1
  ref = Th_element
FEATURE [App::DocumentObjectGroupPython] G4_Th  # scripted group (container) (typed FeaturePython)
  Dunit = g/cm3
  Dvalue = 11.72
  Group = -> [Th_element001]
  conduct = 2
  density = 1
  expand = 3
  formula = Th
  name = G4_Th
  specific = 4
FEATURE [App::DocumentObjectGroupPython] Pa_element001  label="Pa_element : 1"  # scripted group (container) (typed FeaturePython)
  n = 1
  ref = Pa_element
FEATURE [App::DocumentObjectGroupPython] G4_Pa  # scripted group (container) (typed FeaturePython)
  Dunit = g/cm3
  Dvalue = 15.37
  Group = -> [Pa_element001]
  conduct = 2
  density = 1
  expand = 3
  formula = Pa
  name = G4_Pa
  specific = 4
FEATURE [App::DocumentObjectGroupPython] U_element004  label="U_element : 004"  # scripted group (container) (typed FeaturePython)
  n = 1
  ref = U_element
FEATURE [App::DocumentObjectGroupPython] G4_U  # scripted group (container) (typed FeaturePython)
  Dunit = g/cm3
  Dvalue = 18.95
  Group = -> [U_element004]
  conduct = 2
  density = 1
  expand = 3
  formula = U
  name = G4_U
  specific = 4
FEATURE [App::DocumentObjectGroupPython] Np_element001  label="Np_element : 1"  # scripted group (container) (typed FeaturePython)
  n = 1
  ref = Np_element
FEATURE [App::DocumentObjectGroupPython] G4_Np  # scripted group (container) (typed FeaturePython)
  Dunit = g/cm3
  Dvalue = 20.25
  Group = -> [Np_element001]
  conduct = 2
  density = 1
  expand = 3
  formula = Np
  name = G4_Np
  specific = 4
FEATURE [App::DocumentObjectGroupPython] Pu_element002  label="Pu_element : 002"  # scripted group (container) (typed FeaturePython)
  n = 1
  ref = Pu_element
FEATURE [App::DocumentObjectGroupPython] G4_Pu  # scripted group (container) (typed FeaturePython)
  Dunit = g/cm3
  Dvalue = 19.84
  Group = -> [Pu_element002]
  conduct = 2
  density = 1
  expand = 3
  formula = Pu
  name = G4_Pu
  specific = 4
FEATURE [App::DocumentObjectGroupPython] Am_element001  label="Am_element : 1"  # scripted group (container) (typed FeaturePython)
  n = 1
  ref = Am_element
FEATURE [App::DocumentObjectGroupPython] G4_Am  # scripted group (container) (typed FeaturePython)
  Dunit = g/cm3
  Dvalue = 13.67
  Group = -> [Am_element001]
  conduct = 2
  density = 1
  expand = 3
  formula = Am
  name = G4_Am
  specific = 4
FEATURE [App::DocumentObjectGroupPython] Cm_element001  label="Cm_element : 1"  # scripted group (container) (typed FeaturePython)
  n = 1
  ref = Cm_element
FEATURE [App::DocumentObjectGroupPython] G4_Cm  # scripted group (container) (typed FeaturePython)
  Dunit = g/cm3
  Dvalue = 13.51
  Group = -> [Cm_element001]
  conduct = 2
  density = 1
  expand = 3
  formula = Cm
  name = G4_Cm
  specific = 4
FEATURE [App::DocumentObjectGroupPython] Bk_element001  label="Bk_element : 1"  # scripted group (container) (typed FeaturePython)
  n = 1
  ref = Bk_element
FEATURE [App::DocumentObjectGroupPython] G4_Bk  # scripted group (container) (typed FeaturePython)
  Dunit = g/cm3
  Dvalue = 14
  Group = -> [Bk_element001]
  conduct = 2
  density = 1
  expand = 3
  formula = Bk
  name = G4_Bk
  specific = 4
FEATURE [App::DocumentObjectGroupPython] Cf_element001  label="Cf_element : 1"  # scripted group (container) (typed FeaturePython)
  n = 1
  ref = Cf_element
FEATURE [App::DocumentObjectGroupPython] G4_Cf  # scripted group (container) (typed FeaturePython)
  Dunit = g/cm3
  Dvalue = 10
  Group = -> [Cf_element001]
  conduct = 2
  density = 1
  expand = 3
  formula = Cf
  name = G4_Cf
  specific = 4
FEATURE [App::DocumentObjectGroupPython] Element  # scripted group (container) (typed FeaturePython)
  Group = -> [G4_H,G4_He,G4_Li,G4_Be,G4_B,G4_C,G4_N,G4_O,G4_F,G4_Ne,G4_Na,G4_Mg,G4_Al,G4_Si,G4_P,G4_S,G4_Cl,G4_Ar,G4_K,G4_Ca,G4_Sc,G4_Ti,G4_V,G4_Cr,G4_Mn,G4_Fe,G4_Co,G4_Ni,G4_Cu,G4_Zn,G4_Ga,G4_Ge,G4_As,G4_Se,G4_Br,G4_Kr,G4_Rb,G4_Sr,G4_Y,G4_Zr,G4_Nb,G4_Mo,G4_Tc,G4_Ru,G4_Rh,G4_Pd,G4_Ag,G4_Cd,G4_In,G4_Sn,G4_Sb,G4_Te,G4_I,G4_Xe,G4_Cs,G4_Ba,G4_La,G4_Ce,G4_Pr,G4_Nd,G4_Pm,G4_Sm,G4_Eu,G4_Gd,G4_Tb,G4_Dy,G4_Ho,G4_Er,+30 more]
FEATURE [App::DocumentObjectGroupPython] H_element114  label="H_element : 063"  # scripted group (container) (typed FeaturePython)
  n = 2
  ref = H_element
FEATURE [App::DocumentObjectGroupPython] G4_lH2  # scripted group (container) (typed FeaturePython)
  Dunit = g/cm3
  Dvalue = 0.0708
  Group = -> [H_element114]
  conduct = 2
  density = 1
  expand = 3
  formula = G4_lH2
  name = G4_lH2
  specific = 4
FEATURE [App::DocumentObjectGroupPython] N_element049  label="N_element : 022"  # scripted group (container) (typed FeaturePython)
  n = 2
  ref = N_element
FEATURE [App::DocumentObjectGroupPython] G4_lN2  # scripted group (container) (typed FeaturePython)
  Dunit = g/cm3
  Dvalue = 0.807
  Group = -> [N_element049]
  conduct = 2
  density = 1
  expand = 3
  formula = G4_lN2
  name = G4_lN2
  specific = 4
FEATURE [App::DocumentObjectGroupPython] O_element106  label="O_element : 060"  # scripted group (container) (typed FeaturePython)
  n = 2
  ref = O_element
FEATURE [App::DocumentObjectGroupPython] G4_lO2  # scripted group (container) (typed FeaturePython)
  Dunit = g/cm3
  Dvalue = 1.141
  Group = -> [O_element106]
  conduct = 2
  density = 1
  expand = 3
  formula = G4_lO2
  name = G4_lO2
  specific = 4
FEATURE [App::DocumentObjectGroupPython] Ar  label="Ar : 1"  # scripted group (container) (typed FeaturePython)
  n = 1
  ref = Ar
FEATURE [App::DocumentObjectGroupPython] G4_lAr  # scripted group (container) (typed FeaturePython)
  Dunit = g/cm3
  Dvalue = 1.396
  Group = -> [Ar]
  conduct = 2
  density = 1
  expand = 3
  formula = G4_lAr
  name = G4_lAr
  specific = 4
FEATURE [App::DocumentObjectGroupPython] Br  label="Br : 1"  # scripted group (container) (typed FeaturePython)
  n = 1
  ref = Br
FEATURE [App::DocumentObjectGroupPython] G4_lBr  # scripted group (container) (typed FeaturePython)
  Dunit = g/cm3
  Dvalue = 3.1028
  Group = -> [Br]
  conduct = 2
  density = 1
  expand = 3
  formula = G4_lBr
  name = G4_lBr
  specific = 4
FEATURE [App::DocumentObjectGroupPython] Kr  label="Kr : 1"  # scripted group (container) (typed FeaturePython)
  n = 1
  ref = Kr
FEATURE [App::DocumentObjectGroupPython] G4_lKr  # scripted group (container) (typed FeaturePython)
  Dunit = g/cm3
  Dvalue = 2.418
  Group = -> [Kr]
  conduct = 2
  density = 1
  expand = 3
  formula = G4_lKr
  name = G4_lKr
  specific = 4
FEATURE [App::DocumentObjectGroupPython] Xe  label="Xe : 1"  # scripted group (container) (typed FeaturePython)
  n = 1
  ref = Xe
FEATURE [App::DocumentObjectGroupPython] G4_lXe  # scripted group (container) (typed FeaturePython)
  Dunit = g/cm3
  Dvalue = 2.953
  Group = -> [Xe]
  conduct = 2
  density = 1
  expand = 3
  formula = G4_lXe
  name = G4_lXe
  specific = 4
FEATURE [App::DocumentObjectGroupPython] O_element107  label="O_element : 061"  # scripted group (container) (typed FeaturePython)
  n = 4
  ref = O_element
FEATURE [App::DocumentObjectGroupPython] Pb_element004  label="Pb_element : 002"  # scripted group (container) (typed FeaturePython)
  n = 1
  ref = Pb_element
FEATURE [App::DocumentObjectGroupPython] W_element005  label="W_element : 005"  # scripted group (container) (typed FeaturePython)
  n = 1
  ref = W_element
FEATURE [App::DocumentObjectGroupPython] G4_PbWO4  # scripted group (container) (typed FeaturePython)
  Dunit = g/cm3
  Dvalue = 8.28
  Group = -> [O_element107,Pb_element004,W_element005]
  conduct = 2
  density = 1
  expand = 3
  formula = G4_PbWO4
  name = G4_PbWO4
  specific = 4
FEATURE [App::DocumentObjectGroupPython] alactic  label="alactic : 1"  # scripted group (container) (typed FeaturePython)
  n = 1
  ref = alactic
FEATURE [App::DocumentObjectGroupPython] G4_Galactic  # scripted group (container) (typed FeaturePython)
  Dunit = g/cm3
  Dvalue = 0
  Group = -> [alactic]
  conduct = 2
  density = 1
  expand = 3
  formula = G4_Galactic
  name = G4_Galactic
  specific = 4
FEATURE [App::DocumentObjectGroupPython] RAPHITE_POROUS  label="RAPHITE_POROUS : 1"  # scripted group (container) (typed FeaturePython)
  n = 1
  ref = RAPHITE_POROUS
FEATURE [App::DocumentObjectGroupPython] G4_GRAPHITE_POROUS  # scripted group (container) (typed FeaturePython)
  Dunit = g/cm3
  Dvalue = 1.7
  Group = -> [RAPHITE_POROUS]
  conduct = 2
  density = 1
  expand = 3
  formula = G4_GRAPHITE_POROUS
  name = G4_GRAPHITE_POROUS
  specific = 4
FEATURE [App::DocumentObjectGroupPython] H_element115  label="H_element : 0.150"  # scripted group (container) (typed FeaturePython)
  n = 0.080538
FEATURE [App::DocumentObjectGroupPython] C_element125  label="C_element : 0.600"  # scripted group (container) (typed FeaturePython)
  n = 0.599848
FEATURE [App::DocumentObjectGroupPython] O_element108  label="O_element : 0.320"  # scripted group (container) (typed FeaturePython)
  n = 0.319614
FEATURE [App::DocumentObjectGroupPython] G4_LUCITE  # scripted group (container) (typed FeaturePython)
  Dunit = g/cm3
  Dvalue = 1.19
  Group = -> [H_element115,C_element125,O_element108]
  conduct = 2
  density = 1
  expand = 3
  formula = G4_LUCITE
  name = G4_LUCITE
  specific = 4
FEATURE [App::DocumentObjectGroupPython] Cu_element002  label="Cu_element : 62"  # scripted group (container) (typed FeaturePython)
  n = 62
  ref = Cu_element
FEATURE [App::DocumentObjectGroupPython] Zn_element002  label="Zn_element : 35"  # scripted group (container) (typed FeaturePython)
  n = 35
  ref = Zn_element
FEATURE [App::DocumentObjectGroupPython] Pb_element005  label="Pb_element : 3"  # scripted group (container) (typed FeaturePython)
  n = 3
  ref = Pb_element
FEATURE [App::DocumentObjectGroupPython] G4_BRASS  # scripted group (container) (typed FeaturePython)
  Dunit = g/cm3
  Dvalue = 8.52
  Group = -> [Cu_element002,Zn_element002,Pb_element005]
  conduct = 2
  density = 1
  expand = 3
  formula = G4_BRASS
  name = G4_BRASS
  specific = 4
FEATURE [App::DocumentObjectGroupPython] Cu_element003  label="Cu_element : 89"  # scripted group (container) (typed FeaturePython)
  n = 89
  ref = Cu_element
FEATURE [App::DocumentObjectGroupPython] Zn_element003  label="Zn_element : 9"  # scripted group (container) (typed FeaturePython)
  n = 9
  ref = Zn_element
FEATURE [App::DocumentObjectGroupPython] Pb_element006  label="Pb_element : 2"  # scripted group (container) (typed FeaturePython)
  n = 2
  ref = Pb_element
FEATURE [App::DocumentObjectGroupPython] G4_BRONZE  # scripted group (container) (typed FeaturePython)
  Dunit = g/cm3
  Dvalue = 8.82
  Group = -> [Cu_element003,Zn_element003,Pb_element006]
  conduct = 2
  density = 1
  expand = 3
  formula = G4_BRONZE
  name = G4_BRONZE
  specific = 4
FEATURE [App::DocumentObjectGroupPython] Fe_element008  label="Fe_element : 74"  # scripted group (container) (typed FeaturePython)
  n = 74
  ref = Fe_element
FEATURE [App::DocumentObjectGroupPython] Cr_element002  label="Cr_element : 18"  # scripted group (container) (typed FeaturePython)
  n = 18
  ref = Cr_element
FEATURE [App::DocumentObjectGroupPython] Ni_element002  label="Ni_element : 8"  # scripted group (container) (typed FeaturePython)
  n = 8
  ref = Ni_element
FEATURE [App::DocumentObjectGroupPython] G4_STAINLESS_STEEL  label="G4_STAINLESS-STEEL"  # scripted group (container) (typed FeaturePython)
  Dunit = g/cm3
  Dvalue = 8
  Group = -> [Fe_element008,Cr_element002,Ni_element002]
  conduct = 2
  density = 1
  expand = 3
  formula = G4_STAINLESS-STEEL
  name = G4_STAINLESS-STEEL
  specific = 4
FEATURE [App::DocumentObjectGroupPython] H_element116  label="H_element : 064"  # scripted group (container) (typed FeaturePython)
  n = 18
  ref = H_element
FEATURE [App::DocumentObjectGroupPython] C_element126  label="C_element : 071"  # scripted group (container) (typed FeaturePython)
  n = 12
  ref = C_element
FEATURE [App::DocumentObjectGroupPython] O_element109  label="O_element : 062"  # scripted group (container) (typed FeaturePython)
  n = 7
  ref = O_element
FEATURE [App::DocumentObjectGroupPython] G4_CR39  # scripted group (container) (typed FeaturePython)
  Dunit = g/cm3
  Dvalue = 1.32
  Group = -> [H_element116,C_element126,O_element109]
  conduct = 2
  density = 1
  expand = 3
  formula = G4_CR39
  name = G4_CR39
  specific = 4
FEATURE [App::DocumentObjectGroupPython] H_element117  label="H_element : 38"  # scripted group (container) (typed FeaturePython)
  n = 38
  ref = H_element
FEATURE [App::DocumentObjectGroupPython] C_element127  label="C_element : 072"  # scripted group (container) (typed FeaturePython)
  n = 18
  ref = C_element
FEATURE [App::DocumentObjectGroupPython] O_element110  label="O_element : 063"  # scripted group (container) (typed FeaturePython)
  n = 1
  ref = O_element
FEATURE [App::DocumentObjectGroupPython] G4_OCTADECANOL  # scripted group (container) (typed FeaturePython)
  Dunit = g/cm3
  Dvalue = 0.812
  Group = -> [H_element117,C_element127,O_element110]
  conduct = 2
  density = 1
  expand = 3
  formula = G4_OCTADECANOL
  name = G4_OCTADECANOL
  specific = 4
FEATURE [App::DocumentObjectGroupPython] HEP  # scripted group (container) (typed FeaturePython)
  Group = -> [G4_lH2,G4_lN2,G4_lO2,G4_lAr,G4_lBr,G4_lKr,G4_lXe,G4_PbWO4,G4_Galactic,G4_GRAPHITE_POROUS,G4_LUCITE,G4_BRASS,G4_BRONZE,G4_STAINLESS_STEEL,G4_CR39,G4_OCTADECANOL]
FEATURE [App::DocumentObjectGroupPython] C_element128  label="C_element : 073"  # scripted group (container) (typed FeaturePython)
  n = 14
  ref = C_element
FEATURE [App::DocumentObjectGroupPython] H_element118  label="H_element : 065"  # scripted group (container) (typed FeaturePython)
  n = 10
  ref = H_element
FEATURE [App::DocumentObjectGroupPython] O_element111  label="O_element : 064"  # scripted group (container) (typed FeaturePython)
  n = 2
  ref = O_element
FEATURE [App::DocumentObjectGroupPython] N_element050  label="N_element : 023"  # scripted group (container) (typed FeaturePython)
  n = 2
  ref = N_element
FEATURE [App::DocumentObjectGroupPython] G4_KEVLAR  # scripted group (container) (typed FeaturePython)
  Dunit = g/cm3
  Dvalue = 1.44
  Group = -> [C_element128,H_element118,O_element111,N_element050]
  conduct = 2
  density = 1
  expand = 3
  formula = G4_KEVLAR
  name = G4_KEVLAR
  specific = 4
FEATURE [App::DocumentObjectGroupPython] C_element129  label="C_element : 074"  # scripted group (container) (typed FeaturePython)
  n = 10
  ref = C_element
FEATURE [App::DocumentObjectGroupPython] H_element119  label="H_element : 066"  # scripted group (container) (typed FeaturePython)
  n = 8
  ref = H_element
FEATURE [App::DocumentObjectGroupPython] O_element112  label="O_element : 065"  # scripted group (container) (typed FeaturePython)
  n = 4
  ref = O_element
FEATURE [App::DocumentObjectGroupPython] G4_DACRON  # scripted group (container) (typed FeaturePython)
  Dunit = g/cm3
  Dvalue = 1.4
  Group = -> [C_element129,H_element119,O_element112]
  conduct = 2
  density = 1
  expand = 3
  formula = G4_DACRON
  name = G4_DACRON
  specific = 4
FEATURE [App::DocumentObjectGroupPython] C_element130  label="C_element : 075"  # scripted group (container) (typed FeaturePython)
  n = 4
  ref = C_element
FEATURE [App::DocumentObjectGroupPython] H_element120  label="H_element : 067"  # scripted group (container) (typed FeaturePython)
  n = 5
  ref = H_element
FEATURE [App::DocumentObjectGroupPython] Cl_element030  label="Cl_element : 016"  # scripted group (container) (typed FeaturePython)
  n = 1
  ref = Cl_element
FEATURE [App::DocumentObjectGroupPython] G4_NEOPRENE  # scripted group (container) (typed FeaturePython)
  Dunit = g/cm3
  Dvalue = 1.23
  Group = -> [C_element130,H_element120,Cl_element030]
  conduct = 2
  density = 1
  expand = 3
  formula = G4_NEOPRENE
  name = G4_NEOPRENE
  specific = 4
FEATURE [App::DocumentObjectGroupPython] Space  # scripted group (container) (typed FeaturePython)
  Group = -> [G4_KEVLAR,G4_DACRON,G4_NEOPRENE]
FEATURE [App::DocumentObjectGroupPython] H_element121  label="H_element : 068"  # scripted group (container) (typed FeaturePython)
  n = 5
  ref = H_element
FEATURE [App::DocumentObjectGroupPython] C_element131  label="C_element : 076"  # scripted group (container) (typed FeaturePython)
  n = 4
  ref = C_element
FEATURE [App::DocumentObjectGroupPython] N_element051  label="N_element : 3"  # scripted group (container) (typed FeaturePython)
  n = 3
  ref = N_element
FEATURE [App::DocumentObjectGroupPython] O_element113  label="O_element : 066"  # scripted group (container) (typed FeaturePython)
  n = 1
  ref = O_element
FEATURE [App::DocumentObjectGroupPython] G4_CYTOSINE  # scripted group (container) (typed FeaturePython)
  Dunit = g/cm3
  Dvalue = 1.55
  Group = -> [H_element121,C_element131,N_element051,O_element113]
  conduct = 2
  density = 1
  expand = 3
  formula = G4_CYTOSINE
  name = G4_CYTOSINE
  specific = 4
FEATURE [App::DocumentObjectGroupPython] H_element122  label="H_element : 069"  # scripted group (container) (typed FeaturePython)
  n = 6
  ref = H_element
FEATURE [App::DocumentObjectGroupPython] C_element132  label="C_element : 077"  # scripted group (container) (typed FeaturePython)
  n = 5
  ref = C_element
FEATURE [App::DocumentObjectGroupPython] N_element052  label="N_element : 024"  # scripted group (container) (typed FeaturePython)
  n = 2
  ref = N_element
FEATURE [App::DocumentObjectGroupPython] O_element114  label="O_element : 067"  # scripted group (container) (typed FeaturePython)
  n = 2
  ref = O_element
FEATURE [App::DocumentObjectGroupPython] G4_THYMINE  # scripted group (container) (typed FeaturePython)
  Dunit = g/cm3
  Dvalue = 1.23
  Group = -> [H_element122,C_element132,N_element052,O_element114]
  conduct = 2
  density = 1
  expand = 3
  formula = G4_THYMINE
  name = G4_THYMINE
  specific = 4
FEATURE [App::DocumentObjectGroupPython] H_element123  label="H_element : 070"  # scripted group (container) (typed FeaturePython)
  n = 4
  ref = H_element
FEATURE [App::DocumentObjectGroupPython] C_element133  label="C_element : 078"  # scripted group (container) (typed FeaturePython)
  n = 4
  ref = C_element
FEATURE [App::DocumentObjectGroupPython] N_element053  label="N_element : 025"  # scripted group (container) (typed FeaturePython)
  n = 2
  ref = N_element
FEATURE [App::DocumentObjectGroupPython] O_element115  label="O_element : 068"  # scripted group (container) (typed FeaturePython)
  n = 2
  ref = O_element
FEATURE [App::DocumentObjectGroupPython] G4_URACIL  # scripted group (container) (typed FeaturePython)
  Dunit = g/cm3
  Dvalue = 1.32
  Group = -> [H_element123,C_element133,N_element053,O_element115]
  conduct = 2
  density = 1
  expand = 3
  formula = G4_URACIL
  name = G4_URACIL
  specific = 4
FEATURE [App::DocumentObjectGroupPython] H_element124  label="H_element : 071"  # scripted group (container) (typed FeaturePython)
  n = 4
  ref = H_element
FEATURE [App::DocumentObjectGroupPython] C_element134  label="C_element : 079"  # scripted group (container) (typed FeaturePython)
  n = 5
  ref = C_element
FEATURE [App::DocumentObjectGroupPython] N_element054  label="N_element : 026"  # scripted group (container) (typed FeaturePython)
  n = 5
  ref = N_element
FEATURE [App::DocumentObjectGroupPython] G4_DNA_ADENINE  # scripted group (container) (typed FeaturePython)
  Dunit = g/cm3
  Dvalue = 1
  Group = -> [H_element124,C_element134,N_element054]
  conduct = 2
  density = 1
  expand = 3
  formula = G4_DNA_ADENINE
  name = G4_DNA_ADENINE
  specific = 4
FEATURE [App::DocumentObjectGroupPython] H_element125  label="H_element : 072"  # scripted group (container) (typed FeaturePython)
  n = 4
  ref = H_element
FEATURE [App::DocumentObjectGroupPython] C_element135  label="C_element : 080"  # scripted group (container) (typed FeaturePython)
  n = 5
  ref = C_element
FEATURE [App::DocumentObjectGroupPython] N_element055  label="N_element : 027"  # scripted group (container) (typed FeaturePython)
  n = 5
  ref = N_element
FEATURE [App::DocumentObjectGroupPython] O_element116  label="O_element : 069"  # scripted group (container) (typed FeaturePython)
  n = 1
  ref = O_element
FEATURE [App::DocumentObjectGroupPython] G4_DNA_GUANINE  # scripted group (container) (typed FeaturePython)
  Dunit = g/cm3
  Dvalue = 1
  Group = -> [H_element125,C_element135,N_element055,O_element116]
  conduct = 2
  density = 1
  expand = 3
  formula = G4_DNA_GUANINE
  name = G4_DNA_GUANINE
  specific = 4
FEATURE [App::DocumentObjectGroupPython] H_element126  label="H_element : 073"  # scripted group (container) (typed FeaturePython)
  n = 4
  ref = H_element
FEATURE [App::DocumentObjectGroupPython] C_element136  label="C_element : 081"  # scripted group (container) (typed FeaturePython)
  n = 4
  ref = C_element
FEATURE [App::DocumentObjectGroupPython] N_element056  label="N_element : 028"  # scripted group (container) (typed FeaturePython)
  n = 3
  ref = N_element
FEATURE [App::DocumentObjectGroupPython] O_element117  label="O_element : 070"  # scripted group (container) (typed FeaturePython)
  n = 1
  ref = O_element
FEATURE [App::DocumentObjectGroupPython] G4_DNA_CYTOSINE  # scripted group (container) (typed FeaturePython)
  Dunit = g/cm3
  Dvalue = 1
  Group = -> [H_element126,C_element136,N_element056,O_element117]
  conduct = 2
  density = 1
  expand = 3
  formula = G4_DNA_CYTOSINE
  name = G4_DNA_CYTOSINE
  specific = 4
FEATURE [App::DocumentObjectGroupPython] H_element127  label="H_element : 074"  # scripted group (container) (typed FeaturePython)
  n = 5
  ref = H_element
FEATURE [App::DocumentObjectGroupPython] C_element137  label="C_element : 082"  # scripted group (container) (typed FeaturePython)
  n = 5
  ref = C_element
FEATURE [App::DocumentObjectGroupPython] N_element057  label="N_element : 029"  # scripted group (container) (typed FeaturePython)
  n = 2
  ref = N_element
FEATURE [App::DocumentObjectGroupPython] O_element118  label="O_element : 071"  # scripted group (container) (typed FeaturePython)
  n = 2
  ref = O_element
FEATURE [App::DocumentObjectGroupPython] G4_DNA_THYMINE  # scripted group (container) (typed FeaturePython)
  Dunit = g/cm3
  Dvalue = 1
  Group = -> [H_element127,C_element137,N_element057,O_element118]
  conduct = 2
  density = 1
  expand = 3
  formula = G4_DNA_THYMINE
  name = G4_DNA_THYMINE
  specific = 4
FEATURE [App::DocumentObjectGroupPython] H_element128  label="H_element : 075"  # scripted group (container) (typed FeaturePython)
  n = 3
  ref = H_element
FEATURE [App::DocumentObjectGroupPython] C_element138  label="C_element : 083"  # scripted group (container) (typed FeaturePython)
  n = 4
  ref = C_element
FEATURE [App::DocumentObjectGroupPython] N_element058  label="N_element : 030"  # scripted group (container) (typed FeaturePython)
  n = 2
  ref = N_element
FEATURE [App::DocumentObjectGroupPython] O_element119  label="O_element : 072"  # scripted group (container) (typed FeaturePython)
  n = 2
  ref = O_element
FEATURE [App::DocumentObjectGroupPython] G4_DNA_URACIL  # scripted group (container) (typed FeaturePython)
  Dunit = g/cm3
  Dvalue = 1
  Group = -> [H_element128,C_element138,N_element058,O_element119]
  conduct = 2
  density = 1
  expand = 3
  formula = G4_DNA_URACIL
  name = G4_DNA_URACIL
  specific = 4
FEATURE [App::DocumentObjectGroupPython] H_element129  label="H_element : 076"  # scripted group (container) (typed FeaturePython)
  n = 10
  ref = H_element
FEATURE [App::DocumentObjectGroupPython] C_element139  label="C_element : 084"  # scripted group (container) (typed FeaturePython)
  n = 10
  ref = C_element
FEATURE [App::DocumentObjectGroupPython] N_element059  label="N_element : 031"  # scripted group (container) (typed FeaturePython)
  n = 5
  ref = N_element
FEATURE [App::DocumentObjectGroupPython] O_element120  label="O_element : 073"  # scripted group (container) (typed FeaturePython)
  n = 4
  ref = O_element
FEATURE [App::DocumentObjectGroupPython] G4_DNA_ADENOSINE  # scripted group (container) (typed FeaturePython)
  Dunit = g/cm3
  Dvalue = 1
  Group = -> [H_element129,C_element139,N_element059,O_element120]
  conduct = 2
  density = 1
  expand = 3
  formula = G4_DNA_ADENOSINE
  name = G4_DNA_ADENOSINE
  specific = 4
FEATURE [App::DocumentObjectGroupPython] H_element130  label="H_element : 077"  # scripted group (container) (typed FeaturePython)
  n = 10
  ref = H_element
FEATURE [App::DocumentObjectGroupPython] C_element140  label="C_element : 085"  # scripted group (container) (typed FeaturePython)
  n = 10
  ref = C_element
FEATURE [App::DocumentObjectGroupPython] N_element060  label="N_element : 032"  # scripted group (container) (typed FeaturePython)
  n = 5
  ref = N_element
FEATURE [App::DocumentObjectGroupPython] O_element121  label="O_element : 074"  # scripted group (container) (typed FeaturePython)
  n = 5
  ref = O_element
FEATURE [App::DocumentObjectGroupPython] G4_DNA_GUANOSINE  # scripted group (container) (typed FeaturePython)
  Dunit = g/cm3
  Dvalue = 1
  Group = -> [H_element130,C_element140,N_element060,O_element121]
  conduct = 2
  density = 1
  expand = 3
  formula = G4_DNA_GUANOSINE
  name = G4_DNA_GUANOSINE
  specific = 4
FEATURE [App::DocumentObjectGroupPython] H_element131  label="H_element : 078"  # scripted group (container) (typed FeaturePython)
  n = 10
  ref = H_element
FEATURE [App::DocumentObjectGroupPython] C_element141  label="C_element : 086"  # scripted group (container) (typed FeaturePython)
  n = 9
  ref = C_element
FEATURE [App::DocumentObjectGroupPython] N_element061  label="N_element : 033"  # scripted group (container) (typed FeaturePython)
  n = 3
  ref = N_element
FEATURE [App::DocumentObjectGroupPython] O_element122  label="O_element : 075"  # scripted group (container) (typed FeaturePython)
  n = 5
  ref = O_element
FEATURE [App::DocumentObjectGroupPython] G4_DNA_CYTIDINE  # scripted group (container) (typed FeaturePython)
  Dunit = g/cm3
  Dvalue = 1
  Group = -> [H_element131,C_element141,N_element061,O_element122]
  conduct = 2
  density = 1
  expand = 3
  formula = G4_DNA_CYTIDINE
  name = G4_DNA_CYTIDINE
  specific = 4
FEATURE [App::DocumentObjectGroupPython] H_element132  label="H_element : 079"  # scripted group (container) (typed FeaturePython)
  n = 9
  ref = H_element
FEATURE [App::DocumentObjectGroupPython] C_element142  label="C_element : 087"  # scripted group (container) (typed FeaturePython)
  n = 9
  ref = C_element
FEATURE [App::DocumentObjectGroupPython] N_element062  label="N_element : 034"  # scripted group (container) (typed FeaturePython)
  n = 2
  ref = N_element
FEATURE [App::DocumentObjectGroupPython] O_element123  label="O_element : 076"  # scripted group (container) (typed FeaturePython)
  n = 6
  ref = O_element
FEATURE [App::DocumentObjectGroupPython] G4_DNA_URIDINE  # scripted group (container) (typed FeaturePython)
  Dunit = g/cm3
  Dvalue = 1
  Group = -> [H_element132,C_element142,N_element062,O_element123]
  conduct = 2
  density = 1
  expand = 3
  formula = G4_DNA_URIDINE
  name = G4_DNA_URIDINE
  specific = 4
FEATURE [App::DocumentObjectGroupPython] H_element133  label="H_element : 080"  # scripted group (container) (typed FeaturePython)
  n = 11
  ref = H_element
FEATURE [App::DocumentObjectGroupPython] C_element143  label="C_element : 088"  # scripted group (container) (typed FeaturePython)
  n = 10
  ref = C_element
FEATURE [App::DocumentObjectGroupPython] N_element063  label="N_element : 035"  # scripted group (container) (typed FeaturePython)
  n = 2
  ref = N_element
FEATURE [App::DocumentObjectGroupPython] O_element124  label="O_element : 077"  # scripted group (container) (typed FeaturePython)
  n = 6
  ref = O_element
FEATURE [App::DocumentObjectGroupPython] G4_DNA_METHYLURIDINE  # scripted group (container) (typed FeaturePython)
  Dunit = g/cm3
  Dvalue = 1
  Group = -> [H_element133,C_element143,N_element063,O_element124]
  conduct = 2
  density = 1
  expand = 3
  formula = G4_DNA_METHYLURIDINE
  name = G4_DNA_METHYLURIDINE
  specific = 4
FEATURE [App::DocumentObjectGroupPython] P_element014  label="P_element : 003"  # scripted group (container) (typed FeaturePython)
  n = 1
  ref = P_element
FEATURE [App::DocumentObjectGroupPython] O_element125  label="O_element : 078"  # scripted group (container) (typed FeaturePython)
  n = 3
  ref = O_element
FEATURE [App::DocumentObjectGroupPython] G4_DNA_MONOPHOSPHATE  # scripted group (container) (typed FeaturePython)
  Dunit = g/cm3
  Dvalue = 1
  Group = -> [P_element014,O_element125]
  conduct = 2
  density = 1
  expand = 3
  formula = G4_DNA_MONOPHOSPHATE
  name = G4_DNA_MONOPHOSPHATE
  specific = 4
FEATURE [App::DocumentObjectGroupPython] H_element134  label="H_element : 081"  # scripted group (container) (typed FeaturePython)
  n = 10
  ref = H_element
FEATURE [App::DocumentObjectGroupPython] C_element144  label="C_element : 089"  # scripted group (container) (typed FeaturePython)
  n = 10
  ref = C_element
FEATURE [App::DocumentObjectGroupPython] N_element064  label="N_element : 036"  # scripted group (container) (typed FeaturePython)
  n = 5
  ref = N_element
FEATURE [App::DocumentObjectGroupPython] O_element126  label="O_element : 079"  # scripted group (container) (typed FeaturePython)
  n = 7
  ref = O_element
FEATURE [App::DocumentObjectGroupPython] P_element015  label="P_element : 004"  # scripted group (container) (typed FeaturePython)
  n = 1
  ref = P_element
FEATURE [App::DocumentObjectGroupPython] G4_DNA_A  # scripted group (container) (typed FeaturePython)
  Dunit = g/cm3
  Dvalue = 1
  Group = -> [H_element134,C_element144,N_element064,O_element126,P_element015]
  conduct = 2
  density = 1
  expand = 3
  formula = G4_DNA_A
  name = G4_DNA_A
  specific = 4
FEATURE [App::DocumentObjectGroupPython] H_element135  label="H_element : 082"  # scripted group (container) (typed FeaturePython)
  n = 10
  ref = H_element
FEATURE [App::DocumentObjectGroupPython] C_element145  label="C_element : 090"  # scripted group (container) (typed FeaturePython)
  n = 10
  ref = C_element
FEATURE [App::DocumentObjectGroupPython] N_element065  label="N_element : 037"  # scripted group (container) (typed FeaturePython)
  n = 5
  ref = N_element
FEATURE [App::DocumentObjectGroupPython] O_element127  label="O_element : 8"  # scripted group (container) (typed FeaturePython)
  n = 8
  ref = O_element
FEATURE [App::DocumentObjectGroupPython] P_element016  label="P_element : 005"  # scripted group (container) (typed FeaturePython)
  n = 1
  ref = P_element
FEATURE [App::DocumentObjectGroupPython] G4_DNA_G  # scripted group (container) (typed FeaturePython)
  Dunit = g/cm3
  Dvalue = 1
  Group = -> [H_element135,C_element145,N_element065,O_element127,P_element016]
  conduct = 2
  density = 1
  expand = 3
  formula = G4_DNA_G
  name = G4_DNA_G
  specific = 4
FEATURE [App::DocumentObjectGroupPython] H_element136  label="H_element : 083"  # scripted group (container) (typed FeaturePython)
  n = 10
  ref = H_element
FEATURE [App::DocumentObjectGroupPython] C_element146  label="C_element : 091"  # scripted group (container) (typed FeaturePython)
  n = 9
  ref = C_element
FEATURE [App::DocumentObjectGroupPython] N_element066  label="N_element : 038"  # scripted group (container) (typed FeaturePython)
  n = 3
  ref = N_element
FEATURE [App::DocumentObjectGroupPython] O_element128  label="O_element : 080"  # scripted group (container) (typed FeaturePython)
  n = 8
  ref = O_element
FEATURE [App::DocumentObjectGroupPython] P_element017  label="P_element : 006"  # scripted group (container) (typed FeaturePython)
  n = 1
  ref = P_element
FEATURE [App::DocumentObjectGroupPython] G4_DNA_C  # scripted group (container) (typed FeaturePython)
  Dunit = g/cm3
  Dvalue = 1
  Group = -> [H_element136,C_element146,N_element066,O_element128,P_element017]
  conduct = 2
  density = 1
  expand = 3
  formula = G4_DNA_C
  name = G4_DNA_C
  specific = 4
FEATURE [App::DocumentObjectGroupPython] H_element137  label="H_element : 084"  # scripted group (container) (typed FeaturePython)
  n = 9
  ref = H_element
FEATURE [App::DocumentObjectGroupPython] C_element147  label="C_element : 092"  # scripted group (container) (typed FeaturePython)
  n = 9
  ref = C_element
FEATURE [App::DocumentObjectGroupPython] N_element067  label="N_element : 039"  # scripted group (container) (typed FeaturePython)
  n = 2
  ref = N_element
FEATURE [App::DocumentObjectGroupPython] O_element129  label="O_element : 9"  # scripted group (container) (typed FeaturePython)
  n = 9
  ref = O_element
FEATURE [App::DocumentObjectGroupPython] P_element018  label="P_element : 007"  # scripted group (container) (typed FeaturePython)
  n = 1
  ref = P_element
FEATURE [App::DocumentObjectGroupPython] G4_DNA_U  # scripted group (container) (typed FeaturePython)
  Dunit = g/cm3
  Dvalue = 1
  Group = -> [H_element137,C_element147,N_element067,O_element129,P_element018]
  conduct = 2
  density = 1
  expand = 3
  formula = G4_DNA_U
  name = G4_DNA_U
  specific = 4
FEATURE [App::DocumentObjectGroupPython] H_element138  label="H_element : 085"  # scripted group (container) (typed FeaturePython)
  n = 11
  ref = H_element
FEATURE [App::DocumentObjectGroupPython] C_element148  label="C_element : 093"  # scripted group (container) (typed FeaturePython)
  n = 10
  ref = C_element
FEATURE [App::DocumentObjectGroupPython] N_element068  label="N_element : 040"  # scripted group (container) (typed FeaturePython)
  n = 2
  ref = N_element
FEATURE [App::DocumentObjectGroupPython] O_element130  label="O_element : 081"  # scripted group (container) (typed FeaturePython)
  n = 9
  ref = O_element
FEATURE [App::DocumentObjectGroupPython] P_element019  label="P_element : 008"  # scripted group (container) (typed FeaturePython)
  n = 1
  ref = P_element
FEATURE [App::DocumentObjectGroupPython] G4_DNA_MU  # scripted group (container) (typed FeaturePython)
  Dunit = g/cm3
  Dvalue = 1
  Group = -> [H_element138,C_element148,N_element068,O_element130,P_element019]
  conduct = 2
  density = 1
  expand = 3
  formula = G4_DNA_MU
  name = G4_DNA_MU
  specific = 4
FEATURE [App::DocumentObjectGroupPython] BioChemical  # scripted group (container) (typed FeaturePython)
  Group = -> [G4_CYTOSINE,G4_THYMINE,G4_URACIL,G4_DNA_ADENINE,G4_DNA_GUANINE,G4_DNA_CYTOSINE,G4_DNA_THYMINE,G4_DNA_URACIL,G4_DNA_ADENOSINE,G4_DNA_GUANOSINE,G4_DNA_CYTIDINE,G4_DNA_URIDINE,G4_DNA_METHYLURIDINE,G4_DNA_MONOPHOSPHATE,G4_DNA_A,G4_DNA_G,G4_DNA_C,G4_DNA_U,G4_DNA_MU]
FEATURE [App::DocumentObjectGroupPython] G4Materials  # scripted group (container) (typed FeaturePython)
  Group = -> [NIST,Element,HEP,Space,BioChemical]
  version = 1
FEATURE [App::DocumentObjectGroupPython] Geant4  # scripted group (container) (typed FeaturePython)
  Group = -> [G4Isotopes,G4Elements,G4Materials]
FEATURE [App::DocumentObjectGroupPython] Materials  # scripted group (container) (typed FeaturePython)
  Group = -> [Geant4]
FEATURE [Part::FeaturePython] GDMLBox_WorldBox  # WARN: FeaturePython — macro-defined, semantics opaque (R4)
  lunit = 2
  material = 5
  x = 273
  y = 273
  z = 130
FEATURE [Part::FeaturePython] GDMLBox_Box  # WARN: FeaturePython — macro-defined, semantics opaque (R4)
  lunit = 2
  material = 0
  x = 10
  y = 10
  z = 10
FEATURE [App::Part] LV_Box
  Group = -> [GDMLBox_Box]
  Origin = -> Origin002
  Placement = pos=(20,0,0) rot=(0,0,1;0rad)
FEATURE [Part::FeaturePython] Array  # Draft array (typed FeaturePython)
  AlwaysSyncPlacement = false
  Angle = 360
  ArrayType = 1
  Axis = (0,0,1)
  Base = -> LV_Box
  Center = (0,0,0)
  Count = 5
  ExpandArray = false
  Fuse = false
  IntervalAxis = (0,0,0)
  IntervalX = (100,0,0)
  IntervalY = (0,100,0)
  IntervalZ = (0,0,100)
  NumberCircles = 3
  NumberPolar = 5
  NumberX = 2
  NumberY = 2
  NumberZ = 1
  PlacementList = 5 placements: [(20,0,0),(6.18034,19.0211,0),(-16.1803,11.7557,0),(-16.1803,-11.7557,0),(6.18034,-19.0211,0)]
  RadialDistance = 50
  ScaleList = (5) [(1,1,1),(1,1,1),(1,1,1),(1,1,1),(1,1,1)]
  Symmetry = 1
  TangentialDistance = 25
FEATURE [App::Part] Part  label="experiment"
  Group = -> [LV_Box,Array]
  Origin = -> Origin001
FEATURE [App::Part] worldVOL
  Group = -> [GDMLBox_WorldBox,Part]
  Origin = -> Origin
